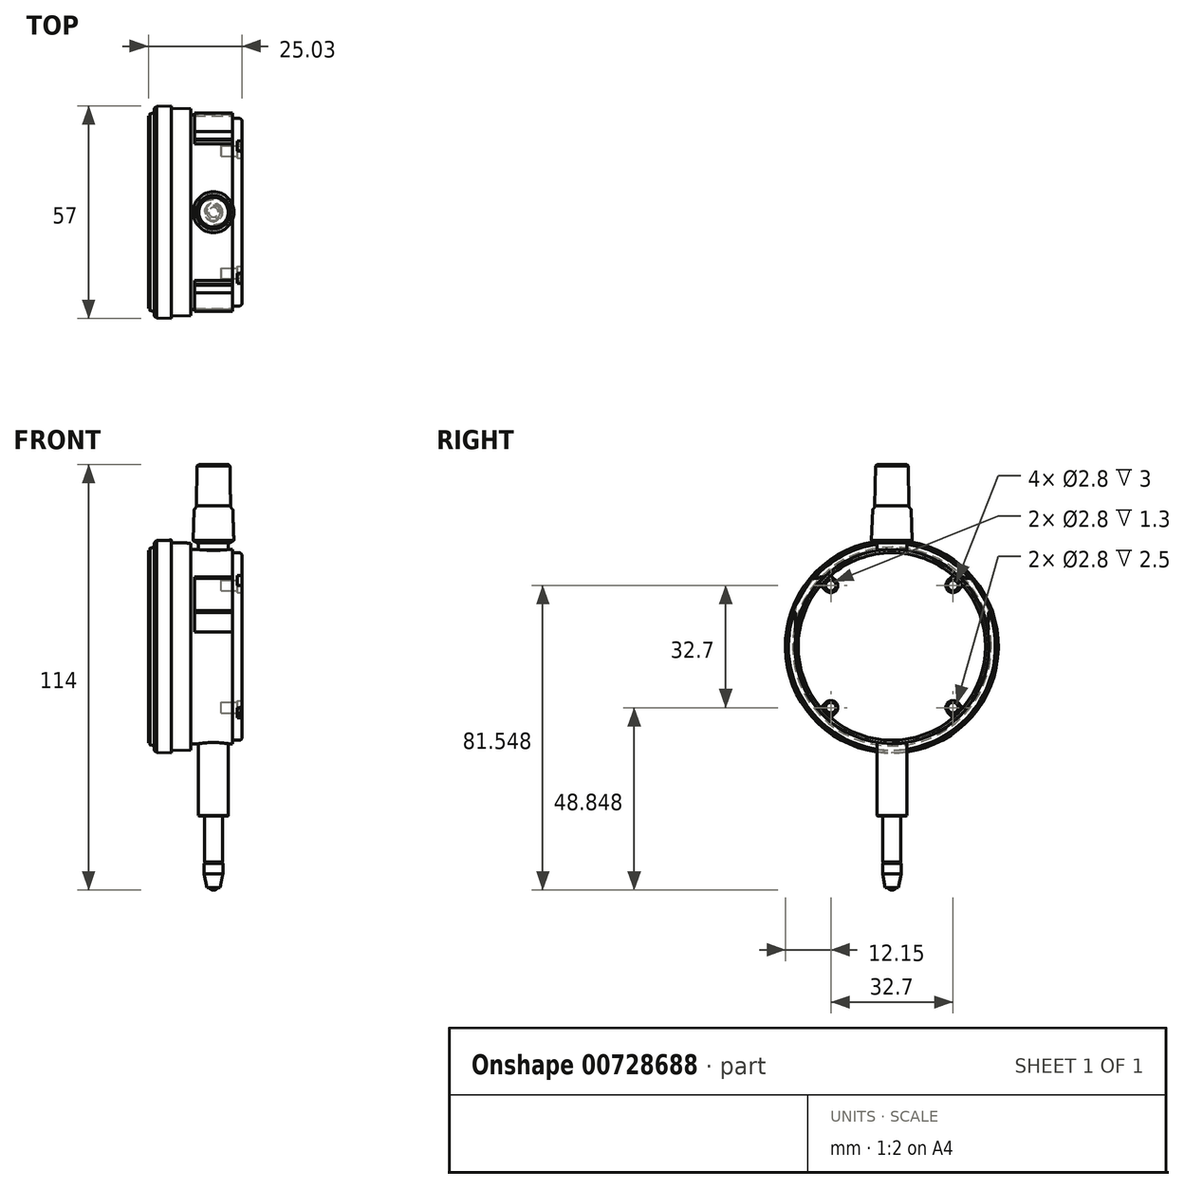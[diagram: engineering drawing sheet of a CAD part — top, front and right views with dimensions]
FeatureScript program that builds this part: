
annotation { "Feature Type Name" : "Feature", "Feature Type Description" : "" }
export const myFeature = defineFeature(function(context is Context, id is Id, definition is map)
    precondition{}
    {
        {
            var Q0;
            Q0=qCreatedBy(makeId("Front.planeOp"),FACE);
            var sketch = newSketch(context, id + "F0", { "sketchPlane" : qUnion([Q0])});
            skLineSegment(sketch, "E0", {"start": v(12.6, 32.51) * mm, "end": v(12.6, 34.58) * mm});
            skLineSegment(sketch, "E1", {"start": v(13, 34.58) * mm, "end": v(12.6, 34.58) * mm});
            skLineSegment(sketch, "E2", {"start": v(12.65, 38.95) * mm, "end": v(12.6, 38.5) * mm});
            skLineSegment(sketch, "E3", {"start": v(12.6, 38.5) * mm, "end": v(12.6, 37.7) * mm});
            skLineSegment(sketch, "E4", {"start": v(12.6, 35.36) * mm, "end": v(12.6, 35.33) * mm});
            skLineSegment(sketch, "E5", {"start": v(12.6, 35.38) * mm, "end": v(12.6, 35.36) * mm});
            skLineSegment(sketch, "E6", {"start": v(12.6, 35.33) * mm, "end": v(12.6, 34.58) * mm});
            skLineSegment(sketch, "E7", {"start": v(12.6, 37.2) * mm, "end": v(12.6, 35.4) * mm});
            skLineSegment(sketch, "E8", {"start": v(12.6, 37.7) * mm, "end": v(12.6, 37.2) * mm});
            skLineSegment(sketch, "E9", {"start": v(12.6, 35.4) * mm, "end": v(12.6, 35.38) * mm});
            skLineSegment(sketch, "E10", {"start": v(12.6, 32.43) * mm, "end": v(12.6, 32.49) * mm});
            skLineSegment(sketch, "E11", {"start": v(12.65, 38.95) * mm, "end": v(12.65, 35.83) * mm});
            skLineSegment(sketch, "E12", {"start": v(13.25, 34.58) * mm, "end": v(13, 34.58) * mm});
            skLineSegment(sketch, "E13", {"start": v(13.3, 32.31) * mm, "end": v(13.22, 32.31) * mm});
            skLineSegment(sketch, "E14", {"start": v(13.3, 34.58) * mm, "end": v(13.25, 34.58) * mm});
            skLineSegment(sketch, "E15", {"start": v(13.3, 33.25) * mm, "end": v(13.3, 34.58) * mm});
            skLineSegment(sketch, "E16", {"start": v(13.3, 34.58) * mm, "end": v(13.3, 34.91) * mm});
            skLineSegment(sketch, "E17", {"start": v(13.3, 33.25) * mm, "end": v(13.3, 32.83) * mm});
            skLineSegment(sketch, "E18", {"start": v(13.3, 32.49) * mm, "end": v(13.3, 32.43) * mm});
            skLineSegment(sketch, "E19", {"start": v(13.3, 32.31) * mm, "end": v(13.3, 32.43) * mm});
            skLineSegment(sketch, "E20", {"start": v(13.3, 32.83) * mm, "end": v(13.3, 32.49) * mm});
            skLineSegment(sketch, "E21", {"start": v(12.65, 35.83) * mm, "end": v(12.6, 35.38) * mm});
            skLineSegment(sketch, "E22", {"start": v(13.22, 32.31) * mm, "end": v(12.6, 32.31) * mm});
            skLineSegment(sketch, "E23", {"start": v(13.3, 32.43) * mm, "end": v(12.6, 32.43) * mm});
            skLineSegment(sketch, "E24", {"start": v(12.6, 32.49) * mm, "end": v(12.6, 32.51) * mm});
            skLineSegment(sketch, "E25", {"start": v(12.6, 32.31) * mm, "end": v(12.6, 32.43) * mm});
            skLineSegment(sketch, "E26", {"start": v(14.23, 36.45) * mm, "end": v(14.25, 36.61) * mm});
            skLineSegment(sketch, "E27", {"start": v(14.62, 36.19) * mm, "end": v(14.5, 36.2) * mm});
            skLineSegment(sketch, "E28", {"start": v(14.6, 35.25) * mm, "end": v(15, 35.22) * mm});
            skLineSegment(sketch, "E29", {"start": v(13.88, 35.3) * mm, "end": v(14.6, 35.25) * mm});
            skLineSegment(sketch, "E30", {"start": v(13.85, 35.3) * mm, "end": v(13.88, 35.3) * mm});
            skLineSegment(sketch, "E31", {"start": v(14.62, 36.97) * mm, "end": v(14.62, 36.19) * mm});
            skLineSegment(sketch, "E32", {"start": v(14.5, 36.92) * mm, "end": v(14.5, 36.2) * mm});
            skLineSegment(sketch, "E33", {"start": v(20.49, 35.87) * mm, "end": v(20.56, 36.52) * mm});
            skLineSegment(sketch, "E34", {"start": v(20.57, 39.75) * mm, "end": v(20.57, 36.63) * mm});
            skArc(sketch, "E35", {"start": v(13.35, 40.26) * mm, "mid": v(13.24, 40.15) * mm, "end": v(13.13, 40.03) * mm});
            skArc(sketch, "E36", {"start": v(13.13, 40.03) * mm, "mid": v(13.04, 39.9) * mm, "end": v(12.95, 39.78) * mm});
            skArc(sketch, "E37", {"start": v(12.95, 39.78) * mm, "mid": v(12.87, 39.65) * mm, "end": v(12.8, 39.51) * mm});
            skArc(sketch, "E38", {"start": v(12.8, 39.51) * mm, "mid": v(12.75, 39.37) * mm, "end": v(12.7, 39.23) * mm});
            skArc(sketch, "E39", {"start": v(12.7, 39.23) * mm, "mid": v(12.67, 39.1) * mm, "end": v(12.65, 38.95) * mm});
            skArc(sketch, "E40", {"start": v(13.3, 34.91) * mm, "mid": v(13.3, 34.94) * mm, "end": v(13.3, 34.96) * mm});
            skArc(sketch, "E41", {"start": v(13.3, 34.96) * mm, "mid": v(13.31, 34.99) * mm, "end": v(13.32, 35.01) * mm});
            skArc(sketch, "E42", {"start": v(13.32, 35.01) * mm, "mid": v(13.33, 35.03) * mm, "end": v(13.34, 35.06) * mm});
            skArc(sketch, "E43", {"start": v(13.34, 35.06) * mm, "mid": v(13.35, 35.08) * mm, "end": v(13.37, 35.1) * mm});
            skArc(sketch, "E44", {"start": v(13.37, 35.1) * mm, "mid": v(13.39, 35.13) * mm, "end": v(13.4, 35.15) * mm});
            skLineSegment(sketch, "E45", {"start": v(13.4, 35.15) * mm, "end": v(13.42, 35.17) * mm});
            skArc(sketch, "E46", {"start": v(13.42, 40.32) * mm, "mid": v(13.5, 40.38) * mm, "end": v(13.57, 40.44) * mm});
            skArc(sketch, "E47", {"start": v(13.57, 40.44) * mm, "mid": v(13.64, 40.5) * mm, "end": v(13.72, 40.54) * mm});
            skLineSegment(sketch, "E48", {"start": v(13.72, 40.54) * mm, "end": v(13.8, 40.6) * mm});
            skArc(sketch, "E49", {"start": v(13.8, 35.3) * mm, "mid": v(13.76, 35.3) * mm, "end": v(13.72, 35.3) * mm});
            skArc(sketch, "E50", {"start": v(13.72, 35.3) * mm, "mid": v(13.68, 35.29) * mm, "end": v(13.63, 35.28) * mm});
            skArc(sketch, "E51", {"start": v(13.63, 35.28) * mm, "mid": v(13.6, 35.27) * mm, "end": v(13.56, 35.25) * mm});
            skArc(sketch, "E52", {"start": v(13.56, 35.25) * mm, "mid": v(13.52, 35.23) * mm, "end": v(13.49, 35.21) * mm});
            skArc(sketch, "E53", {"start": v(13.49, 35.21) * mm, "mid": v(13.45, 35.2) * mm, "end": v(13.42, 35.17) * mm});
            skArc(sketch, "E54", {"start": v(12.65, 35.83) * mm, "mid": v(12.68, 36) * mm, "end": v(12.72, 36.17) * mm});
            skArc(sketch, "E55", {"start": v(12.72, 36.17) * mm, "mid": v(12.78, 36.33) * mm, "end": v(12.86, 36.5) * mm});
            skArc(sketch, "E56", {"start": v(12.86, 36.5) * mm, "mid": v(12.95, 36.65) * mm, "end": v(13.05, 36.8) * mm});
            skArc(sketch, "E57", {"start": v(13.05, 36.8) * mm, "mid": v(13.18, 36.96) * mm, "end": v(13.32, 37.11) * mm});
            skArc(sketch, "E58", {"start": v(13.32, 37.11) * mm, "mid": v(13.5, 37.26) * mm, "end": v(13.68, 37.4) * mm});
            skArc(sketch, "E59", {"start": v(13.68, 37.4) * mm, "mid": v(13.88, 37.52) * mm, "end": v(14.1, 37.63) * mm});
            skLineSegment(sketch, "E60", {"start": v(14.1, 37.63) * mm, "end": v(14.32, 37.73) * mm});
            skArc(sketch, "E61", {"start": v(14.25, 36.61) * mm, "mid": v(14.25, 36.64) * mm, "end": v(14.26, 36.67) * mm});
            skArc(sketch, "E62", {"start": v(14.26, 36.67) * mm, "mid": v(14.27, 36.7) * mm, "end": v(14.28, 36.72) * mm});
            skArc(sketch, "E63", {"start": v(14.28, 36.72) * mm, "mid": v(14.3, 36.74) * mm, "end": v(14.3, 36.77) * mm});
            skArc(sketch, "E64", {"start": v(14.3, 36.77) * mm, "mid": v(14.33, 36.8) * mm, "end": v(14.35, 36.82) * mm});
            skArc(sketch, "E65", {"start": v(14.35, 36.82) * mm, "mid": v(14.37, 36.84) * mm, "end": v(14.4, 36.86) * mm});
            skArc(sketch, "E66", {"start": v(14.4, 36.86) * mm, "mid": v(14.43, 36.88) * mm, "end": v(14.46, 36.9) * mm});
            skLineSegment(sketch, "E67", {"start": v(14.46, 36.9) * mm, "end": v(14.5, 36.92) * mm});
            skArc(sketch, "E68", {"start": v(15, 37.11) * mm, "mid": v(14.87, 37.07) * mm, "end": v(14.73, 37.02) * mm});
            skLineSegment(sketch, "E69", {"start": v(14.73, 37.02) * mm, "end": v(14.6, 36.96) * mm});
            skArc(sketch, "E70", {"start": v(14.6, 36.96) * mm, "mid": v(14.55, 36.94) * mm, "end": v(14.5, 36.92) * mm});
            skArc(sketch, "E71", {"start": v(15.15, 37.16) * mm, "mid": v(15.07, 37.14) * mm, "end": v(15, 37.11) * mm});
            skArc(sketch, "E72", {"start": v(15.03, 35.96) * mm, "mid": v(15, 36) * mm, "end": v(14.98, 36.02) * mm});
            skArc(sketch, "E73", {"start": v(14.98, 36.02) * mm, "mid": v(14.96, 36.05) * mm, "end": v(14.93, 36.08) * mm});
            skArc(sketch, "E74", {"start": v(14.93, 36.08) * mm, "mid": v(14.9, 36.1) * mm, "end": v(14.86, 36.12) * mm});
            skArc(sketch, "E75", {"start": v(14.86, 36.12) * mm, "mid": v(14.83, 36.14) * mm, "end": v(14.79, 36.15) * mm});
            skArc(sketch, "E76", {"start": v(14.79, 36.15) * mm, "mid": v(14.75, 36.17) * mm, "end": v(14.7, 36.18) * mm});
            skArc(sketch, "E77", {"start": v(14.7, 36.18) * mm, "mid": v(14.66, 36.18) * mm, "end": v(14.62, 36.19) * mm});
            skArc(sketch, "E78", {"start": v(14.5, 36.2) * mm, "mid": v(14.47, 36.2) * mm, "end": v(14.44, 36.2) * mm});
            skArc(sketch, "E79", {"start": v(14.44, 36.2) * mm, "mid": v(14.4, 36.21) * mm, "end": v(14.38, 36.23) * mm});
            skArc(sketch, "E80", {"start": v(14.38, 36.23) * mm, "mid": v(14.35, 36.24) * mm, "end": v(14.33, 36.25) * mm});
            skArc(sketch, "E81", {"start": v(14.33, 36.25) * mm, "mid": v(14.3, 36.27) * mm, "end": v(14.29, 36.29) * mm});
            skArc(sketch, "E82", {"start": v(14.29, 36.29) * mm, "mid": v(14.27, 36.3) * mm, "end": v(14.26, 36.33) * mm});
            skArc(sketch, "E83", {"start": v(14.26, 36.33) * mm, "mid": v(14.25, 36.34) * mm, "end": v(14.24, 36.37) * mm});
            skArc(sketch, "E84", {"start": v(14.24, 36.37) * mm, "mid": v(14.23, 36.39) * mm, "end": v(14.23, 36.4) * mm});
            skLineSegment(sketch, "E85", {"start": v(14.23, 36.4) * mm, "end": v(14.23, 36.43) * mm});
            skArc(sketch, "E86", {"start": v(14.32, 40.85) * mm, "mid": v(14.2, 40.8) * mm, "end": v(14.1, 40.75) * mm});
            skArc(sketch, "E87", {"start": v(14.1, 40.75) * mm, "mid": v(13.98, 40.7) * mm, "end": v(13.88, 40.64) * mm});
            skArc(sketch, "E88", {"start": v(15.15, 41.1) * mm, "mid": v(15.08, 41.09) * mm, "end": v(15, 41.07) * mm});
            skArc(sketch, "E89", {"start": v(15.4, 41.17) * mm, "mid": v(15.32, 41.15) * mm, "end": v(15.23, 41.13) * mm});
            skLineSegment(sketch, "E90", {"start": v(15.23, 41.13) * mm, "end": v(15.15, 41.1) * mm});
            skArc(sketch, "E91", {"start": v(15, 41.07) * mm, "mid": v(14.87, 41.03) * mm, "end": v(14.73, 41) * mm});
            skLineSegment(sketch, "E92", {"start": v(14.73, 41) * mm, "end": v(14.6, 40.95) * mm});
            skArc(sketch, "E93", {"start": v(14.6, 40.95) * mm, "mid": v(14.5, 40.92) * mm, "end": v(14.41, 40.88) * mm});
            skLineSegment(sketch, "E94", {"start": v(14.41, 40.88) * mm, "end": v(14.32, 40.85) * mm});
            skArc(sketch, "E95", {"start": v(17.17, 37.42) * mm, "mid": v(16.94, 37.43) * mm, "end": v(16.7, 37.42) * mm});
            skArc(sketch, "E96", {"start": v(16.7, 37.42) * mm, "mid": v(16.48, 37.4) * mm, "end": v(16.25, 37.39) * mm});
            skLineSegment(sketch, "E97", {"start": v(16.25, 37.39) * mm, "end": v(16.02, 37.36) * mm});
            skArc(sketch, "E98", {"start": v(16.02, 37.36) * mm, "mid": v(15.87, 37.33) * mm, "end": v(15.7, 37.3) * mm});
            skArc(sketch, "E99", {"start": v(15.7, 37.3) * mm, "mid": v(15.56, 37.27) * mm, "end": v(15.4, 37.23) * mm});
            skArc(sketch, "E100", {"start": v(16.02, 41.27) * mm, "mid": v(15.87, 41.25) * mm, "end": v(15.71, 41.22) * mm});
            skArc(sketch, "E101", {"start": v(15.71, 41.22) * mm, "mid": v(15.56, 41.2) * mm, "end": v(15.4, 41.17) * mm});
            skArc(sketch, "E102", {"start": v(17.17, 41.32) * mm, "mid": v(16.94, 41.33) * mm, "end": v(16.71, 41.32) * mm});
            skArc(sketch, "E103", {"start": v(16.71, 41.32) * mm, "mid": v(16.48, 41.31) * mm, "end": v(16.25, 41.3) * mm});
            skLineSegment(sketch, "E104", {"start": v(16.25, 41.3) * mm, "end": v(16.02, 41.27) * mm});
            skArc(sketch, "E105", {"start": v(15.36, 37.22) * mm, "mid": v(15.3, 37.2) * mm, "end": v(15.22, 37.18) * mm});
            skLineSegment(sketch, "E106", {"start": v(15.22, 37.18) * mm, "end": v(15.15, 37.16) * mm});
            skArc(sketch, "E107", {"start": v(19.77, 37.66) * mm, "mid": v(19.25, 37.85) * mm, "end": v(18.72, 38) * mm});
            skArc(sketch, "E108", {"start": v(18.72, 38) * mm, "mid": v(18.18, 38.1) * mm, "end": v(17.62, 38.18) * mm});
            skArc(sketch, "E109", {"start": v(17.62, 38.18) * mm, "mid": v(17.05, 38.2) * mm, "end": v(16.49, 38.2) * mm});
            skArc(sketch, "E110", {"start": v(16.49, 38.2) * mm, "mid": v(15.93, 38.14) * mm, "end": v(15.38, 38.04) * mm});
            skArc(sketch, "E111", {"start": v(15.38, 38.04) * mm, "mid": v(14.84, 37.9) * mm, "end": v(14.32, 37.73) * mm});
            skArc(sketch, "E112", {"start": v(20.56, 36.52) * mm, "mid": v(20.56, 36.55) * mm, "end": v(20.56, 36.58) * mm});
            skArc(sketch, "E113", {"start": v(20.56, 36.58) * mm, "mid": v(20.57, 36.6) * mm, "end": v(20.57, 36.63) * mm});
            skArc(sketch, "E114", {"start": v(19.77, 37.66) * mm, "mid": v(19.88, 37.6) * mm, "end": v(20, 37.55) * mm});
            skArc(sketch, "E115", {"start": v(20, 37.55) * mm, "mid": v(20.1, 37.48) * mm, "end": v(20.2, 37.4) * mm});
            skArc(sketch, "E116", {"start": v(20.2, 37.4) * mm, "mid": v(20.28, 37.32) * mm, "end": v(20.35, 37.23) * mm});
            skArc(sketch, "E117", {"start": v(20.35, 37.23) * mm, "mid": v(20.4, 37.15) * mm, "end": v(20.46, 37.07) * mm});
            skArc(sketch, "E118", {"start": v(20.46, 37.07) * mm, "mid": v(20.5, 36.98) * mm, "end": v(20.53, 36.9) * mm});
            skArc(sketch, "E119", {"start": v(20.53, 36.9) * mm, "mid": v(20.55, 36.8) * mm, "end": v(20.56, 36.72) * mm});
            skLineSegment(sketch, "E120", {"start": v(20.56, 36.72) * mm, "end": v(20.57, 36.63) * mm});
            skArc(sketch, "E121", {"start": v(19.77, 40.78) * mm, "mid": v(19.88, 40.73) * mm, "end": v(20, 40.67) * mm});
            skArc(sketch, "E122", {"start": v(20, 40.67) * mm, "mid": v(20.1, 40.6) * mm, "end": v(20.2, 40.52) * mm});
            skArc(sketch, "E123", {"start": v(20.2, 40.52) * mm, "mid": v(20.28, 40.44) * mm, "end": v(20.35, 40.35) * mm});
            skArc(sketch, "E124", {"start": v(20.35, 40.35) * mm, "mid": v(20.4, 40.27) * mm, "end": v(20.46, 40.19) * mm});
            skArc(sketch, "E125", {"start": v(20.46, 40.19) * mm, "mid": v(20.5, 40.1) * mm, "end": v(20.53, 40.02) * mm});
            skArc(sketch, "E126", {"start": v(20.53, 40.02) * mm, "mid": v(20.55, 39.93) * mm, "end": v(20.56, 39.84) * mm});
            skLineSegment(sketch, "E127", {"start": v(20.56, 39.84) * mm, "end": v(20.57, 39.75) * mm});
            skArc(sketch, "E128", {"start": v(19.77, 40.78) * mm, "mid": v(19.68, 40.82) * mm, "end": v(19.6, 40.85) * mm});
            skArc(sketch, "E129", {"start": v(19.17, 37.03) * mm, "mid": v(19.06, 37.07) * mm, "end": v(18.95, 37.1) * mm});
            skArc(sketch, "E130", {"start": v(18.95, 37.1) * mm, "mid": v(18.83, 37.14) * mm, "end": v(18.72, 37.18) * mm});
            skArc(sketch, "E131", {"start": v(18.72, 37.18) * mm, "mid": v(18.59, 37.21) * mm, "end": v(18.46, 37.25) * mm});
            skLineSegment(sketch, "E132", {"start": v(18.46, 37.25) * mm, "end": v(18.32, 37.28) * mm});
            skArc(sketch, "E133", {"start": v(18.32, 37.28) * mm, "mid": v(18.27, 37.29) * mm, "end": v(18.22, 37.3) * mm});
            skArc(sketch, "E134", {"start": v(17.4, 41.31) * mm, "mid": v(17.29, 41.32) * mm, "end": v(17.17, 41.32) * mm});
            skArc(sketch, "E135", {"start": v(17.4, 37.41) * mm, "mid": v(17.33, 37.41) * mm, "end": v(17.25, 37.42) * mm});
            skLineSegment(sketch, "E136", {"start": v(17.25, 37.42) * mm, "end": v(17.17, 37.42) * mm});
            skArc(sketch, "E137", {"start": v(17.5, 37.4) * mm, "mid": v(17.45, 37.4) * mm, "end": v(17.4, 37.41) * mm});
            skArc(sketch, "E138", {"start": v(17.5, 41.3) * mm, "mid": v(17.45, 41.31) * mm, "end": v(17.4, 41.31) * mm});
            skArc(sketch, "E139", {"start": v(18.22, 37.3) * mm, "mid": v(18.15, 37.31) * mm, "end": v(18.08, 37.33) * mm});
            skLineSegment(sketch, "E140", {"start": v(18.08, 37.33) * mm, "end": v(18, 37.34) * mm});
            skArc(sketch, "E141", {"start": v(18.22, 41.22) * mm, "mid": v(18.11, 41.24) * mm, "end": v(18, 41.26) * mm});
            skArc(sketch, "E142", {"start": v(18, 41.26) * mm, "mid": v(17.88, 41.27) * mm, "end": v(17.75, 41.29) * mm});
            skLineSegment(sketch, "E143", {"start": v(17.75, 41.29) * mm, "end": v(17.62, 41.3) * mm});
            skArc(sketch, "E144", {"start": v(17.62, 41.3) * mm, "mid": v(17.56, 41.3) * mm, "end": v(17.5, 41.3) * mm});
            skArc(sketch, "E145", {"start": v(17.62, 37.4) * mm, "mid": v(17.56, 37.4) * mm, "end": v(17.5, 37.4) * mm});
            skArc(sketch, "E146", {"start": v(18, 37.34) * mm, "mid": v(17.88, 37.36) * mm, "end": v(17.75, 37.38) * mm});
            skLineSegment(sketch, "E147", {"start": v(17.75, 37.38) * mm, "end": v(17.62, 37.4) * mm});
            skArc(sketch, "E148", {"start": v(18.98, 41.05) * mm, "mid": v(18.82, 41.1) * mm, "end": v(18.66, 41.14) * mm});
            skArc(sketch, "E149", {"start": v(18.66, 41.14) * mm, "mid": v(18.49, 41.17) * mm, "end": v(18.32, 41.2) * mm});
            skArc(sketch, "E150", {"start": v(19.27, 36.99) * mm, "mid": v(19.22, 37) * mm, "end": v(19.17, 37.03) * mm});
            skArc(sketch, "E151", {"start": v(19.3, 36.97) * mm, "mid": v(19.33, 36.96) * mm, "end": v(19.36, 36.94) * mm});
            skArc(sketch, "E152", {"start": v(19.36, 36.94) * mm, "mid": v(19.38, 36.93) * mm, "end": v(19.41, 36.9) * mm});
            skArc(sketch, "E153", {"start": v(19.41, 36.9) * mm, "mid": v(19.43, 36.9) * mm, "end": v(19.46, 36.87) * mm});
            skArc(sketch, "E154", {"start": v(19.46, 36.87) * mm, "mid": v(19.48, 36.85) * mm, "end": v(19.5, 36.83) * mm});
            skLineSegment(sketch, "E155", {"start": v(19.5, 36.83) * mm, "end": v(19.51, 36.8) * mm});
            skArc(sketch, "E156", {"start": v(19.51, 40.88) * mm, "mid": v(19.34, 40.94) * mm, "end": v(19.16, 41) * mm});
            skLineSegment(sketch, "E157", {"start": v(19.16, 41) * mm, "end": v(18.98, 41.05) * mm});
            skArc(sketch, "E158", {"start": v(19.51, 36.8) * mm, "mid": v(19.52, 36.79) * mm, "end": v(19.53, 36.77) * mm});
            skArc(sketch, "E159", {"start": v(19.53, 36.77) * mm, "mid": v(19.54, 36.76) * mm, "end": v(19.55, 36.74) * mm});
            skArc(sketch, "E160", {"start": v(19.55, 36.74) * mm, "mid": v(19.55, 36.72) * mm, "end": v(19.56, 36.7) * mm});
            skArc(sketch, "E161", {"start": v(19.56, 36.7) * mm, "mid": v(19.57, 36.68) * mm, "end": v(19.57, 36.66) * mm});
            skArc(sketch, "E162", {"start": v(19.57, 36.66) * mm, "mid": v(19.58, 36.64) * mm, "end": v(19.6, 36.62) * mm});
            skLineSegment(sketch, "E163", {"start": v(19.6, 36.62) * mm, "end": v(19.6, 36.6) * mm});
            skArc(sketch, "E164", {"start": v(20.49, 35.87) * mm, "mid": v(20.41, 35.77) * mm, "end": v(20.33, 35.67) * mm});
            skArc(sketch, "E165", {"start": v(20.33, 35.67) * mm, "mid": v(20.24, 35.59) * mm, "end": v(20.15, 35.51) * mm});
            skArc(sketch, "E166", {"start": v(20.15, 35.51) * mm, "mid": v(20.05, 35.45) * mm, "end": v(19.95, 35.39) * mm});
            skArc(sketch, "E167", {"start": v(19.95, 35.39) * mm, "mid": v(19.84, 35.34) * mm, "end": v(19.72, 35.3) * mm});
            skLineSegment(sketch, "E168", {"start": v(19.72, 35.3) * mm, "end": v(19.6, 35.26) * mm});
            skLineSegment(sketch, "E169", {"start": v(13.42, 43.49) * mm, "end": v(13.42, 40.32) * mm});
            skLineSegment(sketch, "E170", {"start": v(13.42, 43.49) * mm, "end": v(13.8, 43.49) * mm});
            skLineSegment(sketch, "E171", {"start": v(13.42, -8.11) * mm, "end": v(13.8, -8.11) * mm});
            skLineSegment(sketch, "E172", {"start": v(13.42, 17.69) * mm, "end": v(13.42, -8.11) * mm});
            skLineSegment(sketch, "E173", {"start": v(13.42, 35.17) * mm, "end": v(13.42, 17.69) * mm});
            skArc(sketch, "E174", {"start": v(13.42, 43.49) * mm, "mid": v(13.39, 41.87) * mm, "end": v(13.35, 40.26) * mm});
            skArc(sketch, "E175", {"start": v(13.22, 32.31) * mm, "mid": v(13.15, 25) * mm, "end": v(13.12, 17.69) * mm});
            skArc(sketch, "E176", {"start": v(13.12, 17.69) * mm, "mid": v(13.2, 4.79) * mm, "end": v(13.42, -8.11) * mm});
            skLineSegment(sketch, "E177", {"start": v(19.6, 35.26) * mm, "end": v(19.6, -10.71) * mm});
            skLineSegment(sketch, "E178", {"start": v(19.6, 35.26) * mm, "end": v(19.6, 36.6) * mm});
            skLineSegment(sketch, "E179", {"start": v(19.6, 46.09) * mm, "end": v(19.6, 40.85) * mm});
            skLineSegment(sketch, "E180", {"start": v(19.6, -10.71) * mm, "end": v(19.5, -10.81) * mm});
            skLineSegment(sketch, "E181", {"start": v(15.56, -10.67) * mm, "end": v(19.5, -10.81) * mm});
            skLineSegment(sketch, "E182", {"start": v(15.45, -10.56) * mm, "end": v(15.56, -10.67) * mm});
            skLineSegment(sketch, "E183", {"start": v(15.15, -10.26) * mm, "end": v(15.45, -10.56) * mm});
            skLineSegment(sketch, "E184", {"start": v(13.8, -8.11) * mm, "end": v(13.8, -8.54) * mm});
            skLineSegment(sketch, "E185", {"start": v(15.15, 45.63) * mm, "end": v(15.45, 45.94) * mm});
            skLineSegment(sketch, "E186", {"start": v(15.45, 45.94) * mm, "end": v(15.56, 46.05) * mm});
            skLineSegment(sketch, "E187", {"start": v(13.88, 44) * mm, "end": v(13.88, 40.64) * mm});
            skLineSegment(sketch, "E188", {"start": v(13.8, 17.69) * mm, "end": v(13.8, -8.11) * mm});
            skLineSegment(sketch, "E189", {"start": v(13.88, 44) * mm, "end": v(15, 44.3) * mm});
            skLineSegment(sketch, "E190", {"start": v(13.88, 35.3) * mm, "end": v(13.88, 17.69) * mm});
            skLineSegment(sketch, "E191", {"start": v(13.8, 43.49) * mm, "end": v(13.8, 40.6) * mm});
            skLineSegment(sketch, "E192", {"start": v(13.8, 35.3) * mm, "end": v(13.8, 17.69) * mm});
            skLineSegment(sketch, "E193", {"start": v(13.8, 43.9) * mm, "end": v(13.8, 43.49) * mm});
            skLineSegment(sketch, "E194", {"start": v(15, 45.19) * mm, "end": v(15, 41.07) * mm});
            skLineSegment(sketch, "E195", {"start": v(15, 37.11) * mm, "end": v(15, 17.69) * mm});
            skLineSegment(sketch, "E196", {"start": v(15, 45.28) * mm, "end": v(15, 45.19) * mm});
            skLineSegment(sketch, "E197", {"start": v(15.15, 45.63) * mm, "end": v(15.15, 41.1) * mm});
            skLineSegment(sketch, "E198", {"start": v(15.15, 37.16) * mm, "end": v(15.15, 17.69) * mm});
            skLineSegment(sketch, "E199", {"start": v(15.56, 46.05) * mm, "end": v(19.5, 46.19) * mm});
            skLineSegment(sketch, "E200", {"start": v(24.8, 45.39) * mm, "end": v(19.6, 45.48) * mm});
            skLineSegment(sketch, "E201", {"start": v(19.6, 46.09) * mm, "end": v(19.5, 46.19) * mm});
            skLineSegment(sketch, "E202", {"start": v(13.88, 17.69) * mm, "end": v(13.88, -8.63) * mm});
            skLineSegment(sketch, "E203", {"start": v(13.88, -8.63) * mm, "end": v(15, -8.93) * mm});
            skLineSegment(sketch, "E204", {"start": v(15, 17.69) * mm, "end": v(15, -9.81) * mm});
            skLineSegment(sketch, "E205", {"start": v(24.8, -10.02) * mm, "end": v(19.6, -10.1) * mm});
            skLineSegment(sketch, "E206", {"start": v(15, -9.81) * mm, "end": v(15, -9.9) * mm});
            skLineSegment(sketch, "E207", {"start": v(15.15, 17.69) * mm, "end": v(15.15, -10.26) * mm});
            skLineSegment(sketch, "E208", {"start": v(24.8, 44.33) * mm, "end": v(24.8, 37.43) * mm});
            skLineSegment(sketch, "E209", {"start": v(24.8, 45.39) * mm, "end": v(24.8, 44.33) * mm});
            skLineSegment(sketch, "E210", {"start": v(24.8, 27.7) * mm, "end": v(24.8, 17.69) * mm});
            skLineSegment(sketch, "E211", {"start": v(24.8, 17.69) * mm, "end": v(24.8, -8.96) * mm});
            skLineSegment(sketch, "E212", {"start": v(24.8, -8.96) * mm, "end": v(24.8, -10.02) * mm});
            skArc(sketch, "E213", {"start": v(13.8, -8.54) * mm, "mid": v(13.82, -8.6) * mm, "end": v(13.88, -8.63) * mm});
            skArc(sketch, "E214", {"start": v(13.88, 44) * mm, "mid": v(13.82, 43.97) * mm, "end": v(13.8, 43.9) * mm});
            skArc(sketch, "E215", {"start": v(15.15, 45.63) * mm, "mid": v(15.04, 45.47) * mm, "end": v(15, 45.28) * mm});
            skArc(sketch, "E216", {"start": v(15, -9.9) * mm, "mid": v(15.04, -10.1) * mm, "end": v(15.15, -10.26) * mm});
            skLineSegment(sketch, "E217", {"start": v(-16.72, 15.9) * mm, "end": v(-16.62, 15.9) * mm});
            skLineSegment(sketch, "E218", {"start": v(-16.79, 15.02) * mm, "end": v(-16.7, 15) * mm});
            skLineSegment(sketch, "E219", {"start": v(-16.89, 14.13) * mm, "end": v(-16.8, 14.12) * mm});
            skLineSegment(sketch, "E220", {"start": v(-17.01, 13.25) * mm, "end": v(-16.92, 13.23) * mm});
            skLineSegment(sketch, "E221", {"start": v(-73.11, 13.25) * mm, "end": v(-73.2, 13.23) * mm});
            skLineSegment(sketch, "E222", {"start": v(-73.45, 18.58) * mm, "end": v(-73.55, 18.58) * mm});
            skLineSegment(sketch, "E223", {"start": v(-73.4, 19.47) * mm, "end": v(-73.5, 19.48) * mm});
            skLineSegment(sketch, "E224", {"start": v(-16.68, 18.58) * mm, "end": v(-16.58, 18.58) * mm});
            skLineSegment(sketch, "E225", {"start": v(-16.68, 16.8) * mm, "end": v(-16.58, 16.8) * mm});
            skLineSegment(sketch, "E226", {"start": v(-16.72, 19.47) * mm, "end": v(-16.62, 19.48) * mm});
            skLineSegment(sketch, "E227", {"start": v(-16.66, 17.69) * mm, "end": v(-16.57, 17.69) * mm});
            skLineSegment(sketch, "E228", {"start": v(-73.45, 16.8) * mm, "end": v(-73.55, 16.8) * mm});
            skLineSegment(sketch, "E229", {"start": v(-62.47, 40.13) * mm, "end": v(-62.53, 40.2) * mm});
            skLineSegment(sketch, "E230", {"start": v(-61.76, 40.66) * mm, "end": v(-61.81, 40.74) * mm});
            skLineSegment(sketch, "E231", {"start": v(-61.03, 41.18) * mm, "end": v(-61.08, 41.26) * mm});
            skLineSegment(sketch, "E232", {"start": v(-60.28, 41.67) * mm, "end": v(-60.33, 41.75) * mm});
            skLineSegment(sketch, "E233", {"start": v(-59.52, 42.13) * mm, "end": v(-59.57, 42.22) * mm});
            skLineSegment(sketch, "E234", {"start": v(-58.75, 42.58) * mm, "end": v(-58.8, 42.66) * mm});
            skLineSegment(sketch, "E235", {"start": v(-57.96, 43) * mm, "end": v(-58, 43.08) * mm});
            skLineSegment(sketch, "E236", {"start": v(-57.16, 43.39) * mm, "end": v(-57.2, 43.47) * mm});
            skLineSegment(sketch, "E237", {"start": v(-56.34, 43.75) * mm, "end": v(-56.38, 43.84) * mm});
            skLineSegment(sketch, "E238", {"start": v(-55.52, 44.1) * mm, "end": v(-55.55, 44.18) * mm});
            skLineSegment(sketch, "E239", {"start": v(-54.68, 44.4) * mm, "end": v(-54.72, 44.5) * mm});
            skLineSegment(sketch, "E240", {"start": v(-53.84, 44.7) * mm, "end": v(-53.87, 44.8) * mm});
            skLineSegment(sketch, "E241", {"start": v(-61.76, -5.29) * mm, "end": v(-61.81, -5.37) * mm});
            skLineSegment(sketch, "E242", {"start": v(-60.28, -6.3) * mm, "end": v(-60.33, -6.37) * mm});
            skLineSegment(sketch, "E243", {"start": v(-59.52, -6.76) * mm, "end": v(-59.57, -6.84) * mm});
            skLineSegment(sketch, "E244", {"start": v(-52.99, 44.96) * mm, "end": v(-53.01, 45.05) * mm});
            skLineSegment(sketch, "E245", {"start": v(-61.03, -5.8) * mm, "end": v(-61.08, -5.88) * mm});
            skLineSegment(sketch, "E246", {"start": v(-55.52, -8.72) * mm, "end": v(-55.55, -8.8) * mm});
            skLineSegment(sketch, "E247", {"start": v(-54.68, -9.03) * mm, "end": v(-54.72, -9.12) * mm});
            skLineSegment(sketch, "E248", {"start": v(-52.99, -9.58) * mm, "end": v(-53.01, -9.68) * mm});
            skLineSegment(sketch, "E249", {"start": v(-53.84, -9.32) * mm, "end": v(-53.87, -9.41) * mm});
            skLineSegment(sketch, "E250", {"start": v(-50.39, -10.2) * mm, "end": v(-50.4, -10.3) * mm});
            skLineSegment(sketch, "E251", {"start": v(-57.96, -7.62) * mm, "end": v(-58, -7.7) * mm});
            skLineSegment(sketch, "E252", {"start": v(-58.75, -7.2) * mm, "end": v(-58.8, -7.28) * mm});
            skLineSegment(sketch, "E253", {"start": v(-41.5, -10.49) * mm, "end": v(-41.5, -10.58) * mm});
            skLineSegment(sketch, "E254", {"start": v(-41.52, -10.34) * mm, "end": v(-41.5, -10.45) * mm});
            skLineSegment(sketch, "E255", {"start": v(-42.4, -10.59) * mm, "end": v(-42.38, -10.68) * mm});
            skLineSegment(sketch, "E256", {"start": v(-42.4, -10.54) * mm, "end": v(-42.4, -10.59) * mm});
            skLineSegment(sketch, "E257", {"start": v(-42.4, -10.44) * mm, "end": v(-42.4, -10.54) * mm});
            skLineSegment(sketch, "E258", {"start": v(-47.74, -10.59) * mm, "end": v(-47.75, -10.68) * mm});
            skLineSegment(sketch, "E259", {"start": v(-45.95, -10.66) * mm, "end": v(-45.96, -10.7) * mm});
            skLineSegment(sketch, "E260", {"start": v(-45.06, -10.67) * mm, "end": v(-45.06, -10.71) * mm});
            skLineSegment(sketch, "E261", {"start": v(-45.06, -10.71) * mm, "end": v(-45.06, -10.8) * mm});
            skLineSegment(sketch, "E262", {"start": v(-45.96, -10.7) * mm, "end": v(-45.96, -10.8) * mm});
            skLineSegment(sketch, "E263", {"start": v(-44.17, -10.7) * mm, "end": v(-44.17, -10.8) * mm});
            skLineSegment(sketch, "E264", {"start": v(-44.17, -10.66) * mm, "end": v(-44.17, -10.7) * mm});
            skLineSegment(sketch, "E265", {"start": v(-46.85, -10.66) * mm, "end": v(-46.85, -10.75) * mm});
            skLineSegment(sketch, "E266", {"start": v(-43.28, -10.66) * mm, "end": v(-43.27, -10.75) * mm});
            skLineSegment(sketch, "E267", {"start": v(-46.84, -10.61) * mm, "end": v(-46.85, -10.66) * mm});
            skLineSegment(sketch, "E268", {"start": v(-43.28, -10.61) * mm, "end": v(-43.28, -10.66) * mm});
            skLineSegment(sketch, "E269", {"start": v(-45.95, -10.55) * mm, "end": v(-45.95, -10.66) * mm});
            skLineSegment(sketch, "E270", {"start": v(-47.73, -10.54) * mm, "end": v(-47.74, -10.59) * mm});
            skLineSegment(sketch, "E271", {"start": v(-44.18, -10.55) * mm, "end": v(-44.17, -10.66) * mm});
            skLineSegment(sketch, "E272", {"start": v(-45.06, -10.56) * mm, "end": v(-45.06, -10.67) * mm});
            skLineSegment(sketch, "E273", {"start": v(-46.84, -10.5) * mm, "end": v(-46.84, -10.61) * mm});
            skLineSegment(sketch, "E274", {"start": v(-43.29, -10.5) * mm, "end": v(-43.28, -10.61) * mm});
            skLineSegment(sketch, "E275", {"start": v(-47.72, -10.44) * mm, "end": v(-47.73, -10.54) * mm});
            skLineSegment(sketch, "E276", {"start": v(-48.6, -10.34) * mm, "end": v(-48.62, -10.45) * mm});
            skLineSegment(sketch, "E277", {"start": v(-48.62, -10.45) * mm, "end": v(-48.62, -10.49) * mm});
            skLineSegment(sketch, "E278", {"start": v(-41.5, -10.45) * mm, "end": v(-41.5, -10.49) * mm});
            skLineSegment(sketch, "E279", {"start": v(-48.62, -10.49) * mm, "end": v(-48.64, -10.58) * mm});
            skLineSegment(sketch, "E280", {"start": v(-48.62, 45.86) * mm, "end": v(-48.64, 45.96) * mm});
            skLineSegment(sketch, "E281", {"start": v(-41.5, 45.82) * mm, "end": v(-41.5, 45.86) * mm});
            skLineSegment(sketch, "E282", {"start": v(-47.72, 45.81) * mm, "end": v(-47.73, 45.92) * mm});
            skLineSegment(sketch, "E283", {"start": v(-42.4, 45.96) * mm, "end": v(-42.38, 46.06) * mm});
            skLineSegment(sketch, "E284", {"start": v(-42.4, 45.92) * mm, "end": v(-42.4, 45.96) * mm});
            skLineSegment(sketch, "E285", {"start": v(-45.06, 46.09) * mm, "end": v(-45.06, 46.18) * mm});
            skLineSegment(sketch, "E286", {"start": v(-45.96, 46.07) * mm, "end": v(-45.96, 46.17) * mm});
            skLineSegment(sketch, "E287", {"start": v(-44.17, 46.07) * mm, "end": v(-44.17, 46.17) * mm});
            skLineSegment(sketch, "E288", {"start": v(-45.06, 46.05) * mm, "end": v(-45.06, 46.09) * mm});
            skLineSegment(sketch, "E289", {"start": v(-44.17, 46.03) * mm, "end": v(-44.17, 46.07) * mm});
            skLineSegment(sketch, "E290", {"start": v(-45.95, 46.03) * mm, "end": v(-45.96, 46.07) * mm});
            skLineSegment(sketch, "E291", {"start": v(-43.28, 46.03) * mm, "end": v(-43.27, 46.13) * mm});
            skLineSegment(sketch, "E292", {"start": v(-46.85, 46.03) * mm, "end": v(-46.85, 46.13) * mm});
            skLineSegment(sketch, "E293", {"start": v(-43.28, 46) * mm, "end": v(-43.28, 46.03) * mm});
            skLineSegment(sketch, "E294", {"start": v(-46.84, 46) * mm, "end": v(-46.85, 46.03) * mm});
            skLineSegment(sketch, "E295", {"start": v(-44.18, 45.92) * mm, "end": v(-44.17, 46.03) * mm});
            skLineSegment(sketch, "E296", {"start": v(-45.95, 45.92) * mm, "end": v(-45.95, 46.03) * mm});
            skLineSegment(sketch, "E297", {"start": v(-45.06, 45.94) * mm, "end": v(-45.06, 46.05) * mm});
            skLineSegment(sketch, "E298", {"start": v(-43.29, 45.88) * mm, "end": v(-43.28, 46) * mm});
            skLineSegment(sketch, "E299", {"start": v(-46.84, 45.88) * mm, "end": v(-46.84, 46) * mm});
            skLineSegment(sketch, "E300", {"start": v(-42.4, 45.81) * mm, "end": v(-42.4, 45.92) * mm});
            skLineSegment(sketch, "E301", {"start": v(-41.52, 45.72) * mm, "end": v(-41.5, 45.82) * mm});
            skLineSegment(sketch, "E302", {"start": v(-47.74, 45.96) * mm, "end": v(-47.75, 46.06) * mm});
            skLineSegment(sketch, "E303", {"start": v(-41.5, 45.86) * mm, "end": v(-41.5, 45.96) * mm});
            skLineSegment(sketch, "E304", {"start": v(-48.62, 45.82) * mm, "end": v(-48.62, 45.86) * mm});
            skLineSegment(sketch, "E305", {"start": v(-48.6, 45.72) * mm, "end": v(-48.62, 45.82) * mm});
            skLineSegment(sketch, "E306", {"start": v(-47.73, 45.92) * mm, "end": v(-47.74, 45.96) * mm});
            skLineSegment(sketch, "E307", {"start": v(-49.5, 45.74) * mm, "end": v(-49.52, 45.83) * mm});
            skLineSegment(sketch, "E308", {"start": v(-49.48, 45.6) * mm, "end": v(-49.5, 45.7) * mm});
            skLineSegment(sketch, "E309", {"start": v(-49.5, -10.36) * mm, "end": v(-49.52, -10.46) * mm});
            skLineSegment(sketch, "E310", {"start": v(-49.5, -10.32) * mm, "end": v(-49.5, -10.36) * mm});
            skLineSegment(sketch, "E311", {"start": v(-49.48, -10.21) * mm, "end": v(-49.5, -10.32) * mm});
            skLineSegment(sketch, "E312", {"start": v(-49.5, 45.7) * mm, "end": v(-49.5, 45.74) * mm});
            skLineSegment(sketch, "E313", {"start": v(-40.62, 45.74) * mm, "end": v(-40.6, 45.83) * mm});
            skLineSegment(sketch, "E314", {"start": v(-40.63, 45.7) * mm, "end": v(-40.62, 45.74) * mm});
            skLineSegment(sketch, "E315", {"start": v(-40.64, 45.6) * mm, "end": v(-40.63, 45.7) * mm});
            skLineSegment(sketch, "E316", {"start": v(-40.63, -10.32) * mm, "end": v(-40.62, -10.36) * mm});
            skLineSegment(sketch, "E317", {"start": v(-40.64, -10.21) * mm, "end": v(-40.63, -10.32) * mm});
            skLineSegment(sketch, "E318", {"start": v(-40.62, -10.36) * mm, "end": v(-40.6, -10.46) * mm});
            skLineSegment(sketch, "E319", {"start": v(-73.46, 17.69) * mm, "end": v(-73.56, 17.69) * mm});
            skLineSegment(sketch, "E320", {"start": v(-73.4, 15.9) * mm, "end": v(-73.5, 15.9) * mm});
            skLineSegment(sketch, "E321", {"start": v(-73.4, 18.58) * mm, "end": v(-73.45, 18.58) * mm});
            skLineSegment(sketch, "E322", {"start": v(-73.42, 17.69) * mm, "end": v(-73.46, 17.69) * mm});
            skLineSegment(sketch, "E323", {"start": v(-73.4, 16.8) * mm, "end": v(-73.45, 16.8) * mm});
            skLineSegment(sketch, "E324", {"start": v(-73.11, 22.13) * mm, "end": v(-73.2, 22.15) * mm});
            skLineSegment(sketch, "E325", {"start": v(-17.05, 13.25) * mm, "end": v(-17.01, 13.25) * mm});
            skLineSegment(sketch, "E326", {"start": v(-73.24, 21.25) * mm, "end": v(-73.34, 21.26) * mm});
            skLineSegment(sketch, "E327", {"start": v(-73.07, 22.12) * mm, "end": v(-73.11, 22.13) * mm});
            skLineSegment(sketch, "E328", {"start": v(-16.76, 19.47) * mm, "end": v(-16.72, 19.47) * mm});
            skLineSegment(sketch, "E329", {"start": v(-17.01, 22.13) * mm, "end": v(-16.92, 22.15) * mm});
            skLineSegment(sketch, "E330", {"start": v(-16.89, 21.25) * mm, "end": v(-16.8, 21.26) * mm});
            skLineSegment(sketch, "E331", {"start": v(-17.05, 22.12) * mm, "end": v(-17.01, 22.13) * mm});
            skLineSegment(sketch, "E332", {"start": v(-16.93, 21.24) * mm, "end": v(-16.89, 21.25) * mm});
            skLineSegment(sketch, "E333", {"start": v(-16.83, 20.36) * mm, "end": v(-16.79, 20.36) * mm});
            skLineSegment(sketch, "E334", {"start": v(-17.04, 21.23) * mm, "end": v(-16.93, 21.24) * mm});
            skLineSegment(sketch, "E335", {"start": v(-16.87, 19.46) * mm, "end": v(-16.76, 19.47) * mm});
            skLineSegment(sketch, "E336", {"start": v(-16.94, 20.35) * mm, "end": v(-16.83, 20.36) * mm});
            skLineSegment(sketch, "E337", {"start": v(-16.83, 18.58) * mm, "end": v(-16.72, 18.58) * mm});
            skLineSegment(sketch, "E338", {"start": v(-16.76, 15.9) * mm, "end": v(-16.72, 15.9) * mm});
            skLineSegment(sketch, "E339", {"start": v(-16.83, 16.8) * mm, "end": v(-16.72, 16.8) * mm});
            skLineSegment(sketch, "E340", {"start": v(-16.81, 17.69) * mm, "end": v(-16.7, 17.69) * mm});
            skLineSegment(sketch, "E341", {"start": v(-17.04, 14.15) * mm, "end": v(-16.93, 14.13) * mm});
            skLineSegment(sketch, "E342", {"start": v(-16.83, 15.02) * mm, "end": v(-16.79, 15.02) * mm});
            skLineSegment(sketch, "E343", {"start": v(-16.94, 15.03) * mm, "end": v(-16.83, 15.02) * mm});
            skLineSegment(sketch, "E344", {"start": v(-16.87, 15.91) * mm, "end": v(-16.76, 15.9) * mm});
            skLineSegment(sketch, "E345", {"start": v(-72.97, 22.1) * mm, "end": v(-73.07, 22.12) * mm});
            skLineSegment(sketch, "E346", {"start": v(-16.93, 14.13) * mm, "end": v(-16.89, 14.13) * mm});
            skLineSegment(sketch, "E347", {"start": v(-73.07, 13.25) * mm, "end": v(-73.11, 13.25) * mm});
            skLineSegment(sketch, "E348", {"start": v(-73.2, 21.24) * mm, "end": v(-73.24, 21.25) * mm});
            skLineSegment(sketch, "E349", {"start": v(-73.2, 14.13) * mm, "end": v(-73.24, 14.13) * mm});
            skLineSegment(sketch, "E350", {"start": v(-73.1, 14.15) * mm, "end": v(-73.2, 14.13) * mm});
            skLineSegment(sketch, "E351", {"start": v(-73.24, 14.13) * mm, "end": v(-73.34, 14.12) * mm});
            skLineSegment(sketch, "E352", {"start": v(-73.26, 15.91) * mm, "end": v(-73.37, 15.9) * mm});
            skLineSegment(sketch, "E353", {"start": v(-73.3, 15.02) * mm, "end": v(-73.34, 15.02) * mm});
            skLineSegment(sketch, "E354", {"start": v(-73.19, 15.03) * mm, "end": v(-73.3, 15.02) * mm});
            skLineSegment(sketch, "E355", {"start": v(-73.37, 15.9) * mm, "end": v(-73.4, 15.9) * mm});
            skLineSegment(sketch, "E356", {"start": v(-73.3, 16.8) * mm, "end": v(-73.4, 16.8) * mm});
            skLineSegment(sketch, "E357", {"start": v(-73.37, 19.47) * mm, "end": v(-73.4, 19.47) * mm});
            skLineSegment(sketch, "E358", {"start": v(-73.3, 18.58) * mm, "end": v(-73.4, 18.58) * mm});
            skLineSegment(sketch, "E359", {"start": v(-73.31, 17.69) * mm, "end": v(-73.42, 17.69) * mm});
            skLineSegment(sketch, "E360", {"start": v(-73.1, 21.23) * mm, "end": v(-73.2, 21.24) * mm});
            skLineSegment(sketch, "E361", {"start": v(-73.3, 20.36) * mm, "end": v(-73.34, 20.36) * mm});
            skLineSegment(sketch, "E362", {"start": v(-73.19, 20.35) * mm, "end": v(-73.3, 20.36) * mm});
            skLineSegment(sketch, "E363", {"start": v(-73.26, 19.46) * mm, "end": v(-73.37, 19.47) * mm});
            skLineSegment(sketch, "E364", {"start": v(-72.97, 13.27) * mm, "end": v(-73.07, 13.25) * mm});
            skLineSegment(sketch, "E365", {"start": v(-73.34, 20.36) * mm, "end": v(-73.43, 20.37) * mm});
            skLineSegment(sketch, "E366", {"start": v(-73.34, 15.02) * mm, "end": v(-73.43, 15) * mm});
            skLineSegment(sketch, "E367", {"start": v(-72.96, 23) * mm, "end": v(-73.06, 23.03) * mm});
            skLineSegment(sketch, "E368", {"start": v(-50.39, 45.59) * mm, "end": v(-50.4, 45.68) * mm});
            skLineSegment(sketch, "E369", {"start": v(-39.74, 45.59) * mm, "end": v(-39.72, 45.68) * mm});
            skLineSegment(sketch, "E370", {"start": v(-17.17, 23) * mm, "end": v(-17.07, 23.03) * mm});
            skLineSegment(sketch, "E371", {"start": v(-17.16, 22.1) * mm, "end": v(-17.05, 22.12) * mm});
            skLineSegment(sketch, "E372", {"start": v(-17.16, 13.27) * mm, "end": v(-17.05, 13.25) * mm});
            skLineSegment(sketch, "E373", {"start": v(-16.7, 17.69) * mm, "end": v(-16.66, 17.69) * mm});
            skLineSegment(sketch, "E374", {"start": v(-16.72, 16.8) * mm, "end": v(-16.68, 16.8) * mm});
            skLineSegment(sketch, "E375", {"start": v(-16.72, 18.58) * mm, "end": v(-16.68, 18.58) * mm});
            skLineSegment(sketch, "E376", {"start": v(-16.79, 20.36) * mm, "end": v(-16.7, 20.37) * mm});
            skLineSegment(sketch, "E377", {"start": v(-17.17, 12.37) * mm, "end": v(-17.07, 12.35) * mm});
            skLineSegment(sketch, "E378", {"start": v(-72.96, 12.37) * mm, "end": v(-73.06, 12.35) * mm});
            skLineSegment(sketch, "E379", {"start": v(-50.36, -10.06) * mm, "end": v(-50.38, -10.17) * mm});
            skLineSegment(sketch, "E380", {"start": v(-39.77, -10.06) * mm, "end": v(-39.75, -10.17) * mm});
            skLineSegment(sketch, "E381", {"start": v(-39.75, -10.17) * mm, "end": v(-39.74, -10.2) * mm});
            skLineSegment(sketch, "E382", {"start": v(-50.38, -10.17) * mm, "end": v(-50.39, -10.2) * mm});
            skLineSegment(sketch, "E383", {"start": v(-38.9, 45.26) * mm, "end": v(-38.88, 45.36) * mm});
            skLineSegment(sketch, "E384", {"start": v(-38.87, 45.4) * mm, "end": v(-38.85, 45.5) * mm});
            skLineSegment(sketch, "E385", {"start": v(-38.88, 45.36) * mm, "end": v(-38.87, 45.4) * mm});
            skLineSegment(sketch, "E386", {"start": v(-17.2, 12.37) * mm, "end": v(-17.17, 12.37) * mm});
            skLineSegment(sketch, "E387", {"start": v(-17.35, 23.88) * mm, "end": v(-17.25, 23.9) * mm});
            skLineSegment(sketch, "E388", {"start": v(-17.56, 24.75) * mm, "end": v(-17.46, 24.78) * mm});
            skLineSegment(sketch, "E389", {"start": v(-17.39, 23.87) * mm, "end": v(-17.35, 23.88) * mm});
            skLineSegment(sketch, "E390", {"start": v(-17.2, 23) * mm, "end": v(-17.17, 23) * mm});
            skLineSegment(sketch, "E391", {"start": v(-17.31, 22.98) * mm, "end": v(-17.2, 23) * mm});
            skLineSegment(sketch, "E392", {"start": v(-17.5, 23.85) * mm, "end": v(-17.39, 23.87) * mm});
            skLineSegment(sketch, "E393", {"start": v(-17.39, 11.5) * mm, "end": v(-17.35, 11.5) * mm});
            skLineSegment(sketch, "E394", {"start": v(-17.5, 11.53) * mm, "end": v(-17.39, 11.5) * mm});
            skLineSegment(sketch, "E395", {"start": v(-17.35, 11.5) * mm, "end": v(-17.25, 11.47) * mm});
            skLineSegment(sketch, "E396", {"start": v(-17.31, 12.4) * mm, "end": v(-17.2, 12.37) * mm});
            skLineSegment(sketch, "E397", {"start": v(-17.8, 25.61) * mm, "end": v(-17.7, 25.64) * mm});
            skLineSegment(sketch, "E398", {"start": v(-18.05, 26.46) * mm, "end": v(-17.96, 26.5) * mm});
            skLineSegment(sketch, "E399", {"start": v(-18.34, 27.3) * mm, "end": v(-18.25, 27.34) * mm});
            skLineSegment(sketch, "E400", {"start": v(-23.18, 35.8) * mm, "end": v(-23.1, 35.85) * mm});
            skLineSegment(sketch, "E401", {"start": v(-31.38, 42.58) * mm, "end": v(-31.34, 42.66) * mm});
            skLineSegment(sketch, "E402", {"start": v(-32.17, 43) * mm, "end": v(-32.13, 43.08) * mm});
            skLineSegment(sketch, "E403", {"start": v(-38, 45.2) * mm, "end": v(-37.98, 45.29) * mm});
            skLineSegment(sketch, "E404", {"start": v(-39.77, 45.44) * mm, "end": v(-39.75, 45.54) * mm});
            skLineSegment(sketch, "E405", {"start": v(-72.92, 23) * mm, "end": v(-72.96, 23) * mm});
            skLineSegment(sketch, "E406", {"start": v(-72.78, 11.5) * mm, "end": v(-72.87, 11.47) * mm});
            skLineSegment(sketch, "E407", {"start": v(-72.57, 10.63) * mm, "end": v(-72.66, 10.6) * mm});
            skLineSegment(sketch, "E408", {"start": v(-72.74, 11.5) * mm, "end": v(-72.78, 11.5) * mm});
            skLineSegment(sketch, "E409", {"start": v(-72.92, 12.37) * mm, "end": v(-72.96, 12.37) * mm});
            skLineSegment(sketch, "E410", {"start": v(-72.81, 12.4) * mm, "end": v(-72.92, 12.37) * mm});
            skLineSegment(sketch, "E411", {"start": v(-72.63, 11.53) * mm, "end": v(-72.74, 11.5) * mm});
            skLineSegment(sketch, "E412", {"start": v(-69.95, 4) * mm, "end": v(-70.04, 3.96) * mm});
            skLineSegment(sketch, "E413", {"start": v(-69.5, 3.23) * mm, "end": v(-69.6, 3.18) * mm});
            skLineSegment(sketch, "E414", {"start": v(-66.95, -0.41) * mm, "end": v(-67.02, -0.48) * mm});
            skLineSegment(sketch, "E415", {"start": v(-66.37, -1.1) * mm, "end": v(-66.44, -1.16) * mm});
            skLineSegment(sketch, "E416", {"start": v(-65.77, -1.75) * mm, "end": v(-65.84, -1.82) * mm});
            skLineSegment(sketch, "E417", {"start": v(-65.15, -2.4) * mm, "end": v(-65.21, -2.46) * mm});
            skLineSegment(sketch, "E418", {"start": v(-63.17, -4.2) * mm, "end": v(-63.23, -4.27) * mm});
            skLineSegment(sketch, "E419", {"start": v(-62.47, -4.75) * mm, "end": v(-62.53, -4.83) * mm});
            skLineSegment(sketch, "E420", {"start": v(-52.13, -9.82) * mm, "end": v(-52.15, -9.91) * mm});
            skLineSegment(sketch, "E421", {"start": v(-38.9, -9.88) * mm, "end": v(-38.88, -9.99) * mm});
            skLineSegment(sketch, "E422", {"start": v(-36.3, -9.28) * mm, "end": v(-36.29, -9.32) * mm});
            skLineSegment(sketch, "E423", {"start": v(-37.14, -9.58) * mm, "end": v(-37.11, -9.68) * mm});
            skLineSegment(sketch, "E424", {"start": v(-37.15, -9.54) * mm, "end": v(-37.14, -9.58) * mm});
            skLineSegment(sketch, "E425", {"start": v(-38.04, -9.67) * mm, "end": v(-38.01, -9.78) * mm});
            skLineSegment(sketch, "E426", {"start": v(-37.18, -9.44) * mm, "end": v(-37.15, -9.54) * mm});
            skLineSegment(sketch, "E427", {"start": v(-36.33, -9.18) * mm, "end": v(-36.3, -9.28) * mm});
            skLineSegment(sketch, "E428", {"start": v(-52.98, -9.54) * mm, "end": v(-52.99, -9.58) * mm});
            skLineSegment(sketch, "E429", {"start": v(-53.8, -9.18) * mm, "end": v(-53.83, -9.28) * mm});
            skLineSegment(sketch, "E430", {"start": v(-52.94, -9.44) * mm, "end": v(-52.98, -9.54) * mm});
            skLineSegment(sketch, "E431", {"start": v(-52.09, -9.67) * mm, "end": v(-52.12, -9.78) * mm});
            skLineSegment(sketch, "E432", {"start": v(-53.83, -9.28) * mm, "end": v(-53.84, -9.32) * mm});
            skLineSegment(sketch, "E433", {"start": v(-36.29, -9.32) * mm, "end": v(-36.26, -9.41) * mm});
            skLineSegment(sketch, "E434", {"start": v(-72.07, 8.91) * mm, "end": v(-72.17, 8.88) * mm});
            skLineSegment(sketch, "E435", {"start": v(-71.93, 26.42) * mm, "end": v(-72.03, 26.45) * mm});
            skLineSegment(sketch, "E436", {"start": v(-72.2, 25.57) * mm, "end": v(-72.3, 25.6) * mm});
            skLineSegment(sketch, "E437", {"start": v(-72.43, 24.71) * mm, "end": v(-72.53, 24.74) * mm});
            skLineSegment(sketch, "E438", {"start": v(-72.34, 9.76) * mm, "end": v(-72.43, 9.74) * mm});
            skLineSegment(sketch, "E439", {"start": v(-72.3, 9.78) * mm, "end": v(-72.34, 9.76) * mm});
            skLineSegment(sketch, "E440", {"start": v(-72.43, 10.66) * mm, "end": v(-72.53, 10.64) * mm});
            skLineSegment(sketch, "E441", {"start": v(-72.2, 9.8) * mm, "end": v(-72.3, 9.78) * mm});
            skLineSegment(sketch, "E442", {"start": v(-71.93, 8.96) * mm, "end": v(-72.03, 8.92) * mm});
            skLineSegment(sketch, "E443", {"start": v(-72.03, 8.92) * mm, "end": v(-72.07, 8.91) * mm});
            skLineSegment(sketch, "E444", {"start": v(-52.09, 45.05) * mm, "end": v(-52.12, 45.16) * mm});
            skLineSegment(sketch, "E445", {"start": v(-52.94, 44.82) * mm, "end": v(-52.98, 44.92) * mm});
            skLineSegment(sketch, "E446", {"start": v(-53.8, 44.56) * mm, "end": v(-53.83, 44.66) * mm});
            skLineSegment(sketch, "E447", {"start": v(-36.33, 44.56) * mm, "end": v(-36.3, 44.66) * mm});
            skLineSegment(sketch, "E448", {"start": v(-37.18, 44.82) * mm, "end": v(-37.15, 44.92) * mm});
            skLineSegment(sketch, "E449", {"start": v(-38.04, 45.05) * mm, "end": v(-38.01, 45.16) * mm});
            skLineSegment(sketch, "E450", {"start": v(-17.7, 24.71) * mm, "end": v(-17.6, 24.74) * mm});
            skLineSegment(sketch, "E451", {"start": v(-17.94, 25.57) * mm, "end": v(-17.83, 25.6) * mm});
            skLineSegment(sketch, "E452", {"start": v(-18.2, 26.42) * mm, "end": v(-18.1, 26.45) * mm});
            skLineSegment(sketch, "E453", {"start": v(-17.8, 9.76) * mm, "end": v(-17.7, 9.74) * mm});
            skLineSegment(sketch, "E454", {"start": v(-17.83, 9.78) * mm, "end": v(-17.8, 9.76) * mm});
            skLineSegment(sketch, "E455", {"start": v(-18.2, 8.96) * mm, "end": v(-18.1, 8.92) * mm});
            skLineSegment(sketch, "E456", {"start": v(-17.94, 9.8) * mm, "end": v(-17.83, 9.78) * mm});
            skLineSegment(sketch, "E457", {"start": v(-17.7, 10.66) * mm, "end": v(-17.6, 10.64) * mm});
            skLineSegment(sketch, "E458", {"start": v(-18.1, 8.92) * mm, "end": v(-18.05, 8.91) * mm});
            skLineSegment(sketch, "E459", {"start": v(-18.05, 8.91) * mm, "end": v(-17.96, 8.88) * mm});
            skLineSegment(sketch, "E460", {"start": v(-18.66, 7.23) * mm, "end": v(-18.57, 7.2) * mm});
            skLineSegment(sketch, "E461", {"start": v(-18.7, 7.25) * mm, "end": v(-18.66, 7.23) * mm});
            skLineSegment(sketch, "E462", {"start": v(-33.78, -8.38) * mm, "end": v(-33.75, -8.46) * mm});
            skLineSegment(sketch, "E463", {"start": v(-33.8, -8.34) * mm, "end": v(-33.78, -8.38) * mm});
            skLineSegment(sketch, "E464", {"start": v(-19.04, 6.43) * mm, "end": v(-19, 6.4) * mm});
            skLineSegment(sketch, "E465", {"start": v(-19.37, 5.6) * mm, "end": v(-19.28, 5.56) * mm});
            skLineSegment(sketch, "E466", {"start": v(-33.04, -7.87) * mm, "end": v(-32.99, -7.97) * mm});
            skLineSegment(sketch, "E467", {"start": v(-19.4, 5.61) * mm, "end": v(-19.37, 5.6) * mm});
            skLineSegment(sketch, "E468", {"start": v(-23.3, 35.7) * mm, "end": v(-23.21, 35.76) * mm});
            skLineSegment(sketch, "E469", {"start": v(-19.5, 29.72) * mm, "end": v(-19.4, 29.76) * mm});
            skLineSegment(sketch, "E470", {"start": v(-19.9, 30.51) * mm, "end": v(-19.8, 30.56) * mm});
            skLineSegment(sketch, "E471", {"start": v(-20.3, 31.3) * mm, "end": v(-20.21, 31.35) * mm});
            skLineSegment(sketch, "E472", {"start": v(-20.75, 32.07) * mm, "end": v(-20.65, 32.12) * mm});
            skLineSegment(sketch, "E473", {"start": v(-21.21, 32.83) * mm, "end": v(-21.12, 32.88) * mm});
            skLineSegment(sketch, "E474", {"start": v(-21.7, 33.57) * mm, "end": v(-21.6, 33.63) * mm});
            skLineSegment(sketch, "E475", {"start": v(-22.2, 34.3) * mm, "end": v(-22.12, 34.36) * mm});
            skLineSegment(sketch, "E476", {"start": v(-22.74, 35) * mm, "end": v(-22.66, 35.07) * mm});
            skLineSegment(sketch, "E477", {"start": v(-27.75, 40.01) * mm, "end": v(-27.68, 40.1) * mm});
            skLineSegment(sketch, "E478", {"start": v(-28.46, 40.54) * mm, "end": v(-28.4, 40.63) * mm});
            skLineSegment(sketch, "E479", {"start": v(-29.18, 41.05) * mm, "end": v(-29.12, 41.14) * mm});
            skLineSegment(sketch, "E480", {"start": v(-29.93, 41.54) * mm, "end": v(-29.87, 41.63) * mm});
            skLineSegment(sketch, "E481", {"start": v(-30.68, 42) * mm, "end": v(-30.63, 42.1) * mm});
            skLineSegment(sketch, "E482", {"start": v(-31.45, 42.44) * mm, "end": v(-31.4, 42.54) * mm});
            skLineSegment(sketch, "E483", {"start": v(-32.24, 42.86) * mm, "end": v(-32.19, 42.96) * mm});
            skLineSegment(sketch, "E484", {"start": v(-57.1, -7.87) * mm, "end": v(-57.14, -7.97) * mm});
            skLineSegment(sketch, "E485", {"start": v(-57.89, -7.48) * mm, "end": v(-57.94, -7.58) * mm});
            skLineSegment(sketch, "E486", {"start": v(-70.23, 4.86) * mm, "end": v(-70.33, 4.81) * mm});
            skLineSegment(sketch, "E487", {"start": v(-70.23, 30.51) * mm, "end": v(-70.33, 30.56) * mm});
            skLineSegment(sketch, "E488", {"start": v(-57.89, 42.86) * mm, "end": v(-57.94, 42.96) * mm});
            skLineSegment(sketch, "E489", {"start": v(-32.17, -7.62) * mm, "end": v(-32.13, -7.7) * mm});
            skLineSegment(sketch, "E490", {"start": v(-32.19, -7.58) * mm, "end": v(-32.17, -7.62) * mm});
            skLineSegment(sketch, "E491", {"start": v(-31.38, -7.2) * mm, "end": v(-31.34, -7.28) * mm});
            skLineSegment(sketch, "E492", {"start": v(-32.24, -7.48) * mm, "end": v(-32.19, -7.58) * mm});
            skLineSegment(sketch, "E493", {"start": v(-19.9, 4.86) * mm, "end": v(-19.8, 4.81) * mm});
            skLineSegment(sketch, "E494", {"start": v(-69.82, 31.3) * mm, "end": v(-69.91, 31.35) * mm});
            skLineSegment(sketch, "E495", {"start": v(-69.82, 4.08) * mm, "end": v(-69.91, 4.03) * mm});
            skLineSegment(sketch, "E496", {"start": v(-58.67, -7.07) * mm, "end": v(-58.73, -7.16) * mm});
            skLineSegment(sketch, "E497", {"start": v(-27.75, -4.63) * mm, "end": v(-27.68, -4.72) * mm});
            skLineSegment(sketch, "E498", {"start": v(-69.38, 3.3) * mm, "end": v(-69.47, 3.25) * mm});
            skLineSegment(sketch, "E499", {"start": v(-68.92, 2.55) * mm, "end": v(-69, 2.5) * mm});
            skLineSegment(sketch, "E500", {"start": v(-68.92, 32.83) * mm, "end": v(-69, 32.88) * mm});
            skLineSegment(sketch, "E501", {"start": v(-69.38, 32.07) * mm, "end": v(-69.47, 32.12) * mm});
            skLineSegment(sketch, "E502", {"start": v(-62.38, -4.63) * mm, "end": v(-62.44, -4.72) * mm});
            skLineSegment(sketch, "E503", {"start": v(-67.92, 1.08) * mm, "end": v(-68, 1.02) * mm});
            skLineSegment(sketch, "E504", {"start": v(-67.92, 34.3) * mm, "end": v(-68, 34.36) * mm});
            skLineSegment(sketch, "E505", {"start": v(-63.07, -4.08) * mm, "end": v(-63.14, -4.16) * mm});
            skLineSegment(sketch, "E506", {"start": v(-60.2, 41.54) * mm, "end": v(-60.26, 41.63) * mm});
            skLineSegment(sketch, "E507", {"start": v(-59.44, 42) * mm, "end": v(-59.5, 42.1) * mm});
            skLineSegment(sketch, "E508", {"start": v(-30.63, -6.72) * mm, "end": v(-30.6, -6.76) * mm});
            skLineSegment(sketch, "E509", {"start": v(-20.62, 3.23) * mm, "end": v(-20.54, 3.18) * mm});
            skLineSegment(sketch, "E510", {"start": v(-20.75, 3.3) * mm, "end": v(-20.65, 3.25) * mm});
            skLineSegment(sketch, "E511", {"start": v(-68.43, 1.8) * mm, "end": v(-68.52, 1.75) * mm});
            skLineSegment(sketch, "E512", {"start": v(-27.06, -4.08) * mm, "end": v(-26.99, -4.16) * mm});
            skLineSegment(sketch, "E513", {"start": v(-21.08, 2.47) * mm, "end": v(-21, 2.42) * mm});
            skLineSegment(sketch, "E514", {"start": v(-68.43, 33.57) * mm, "end": v(-68.52, 33.63) * mm});
            skLineSegment(sketch, "E515", {"start": v(-26.96, -4.2) * mm, "end": v(-26.9, -4.27) * mm});
            skLineSegment(sketch, "E516", {"start": v(-27.66, -4.75) * mm, "end": v(-27.6, -4.83) * mm});
            skLineSegment(sketch, "E517", {"start": v(-28.37, -5.29) * mm, "end": v(-28.31, -5.37) * mm});
            skLineSegment(sketch, "E518", {"start": v(-28.4, -5.25) * mm, "end": v(-28.37, -5.29) * mm});
            skLineSegment(sketch, "E519", {"start": v(-29.1, -5.8) * mm, "end": v(-29.05, -5.88) * mm});
            skLineSegment(sketch, "E520", {"start": v(-29.85, -6.3) * mm, "end": v(-29.8, -6.37) * mm});
            skLineSegment(sketch, "E521", {"start": v(-29.87, -6.26) * mm, "end": v(-29.85, -6.3) * mm});
            skLineSegment(sketch, "E522", {"start": v(-30.68, -6.63) * mm, "end": v(-30.63, -6.72) * mm});
            skLineSegment(sketch, "E523", {"start": v(-29.93, -6.16) * mm, "end": v(-29.87, -6.26) * mm});
            skLineSegment(sketch, "E524", {"start": v(-29.18, -5.68) * mm, "end": v(-29.12, -5.77) * mm});
            skLineSegment(sketch, "E525", {"start": v(-29.12, -5.77) * mm, "end": v(-29.1, -5.8) * mm});
            skLineSegment(sketch, "E526", {"start": v(-28.46, -5.17) * mm, "end": v(-28.4, -5.25) * mm});
            skLineSegment(sketch, "E527", {"start": v(-27.68, -4.72) * mm, "end": v(-27.66, -4.75) * mm});
            skLineSegment(sketch, "E528", {"start": v(-61.67, -5.17) * mm, "end": v(-61.73, -5.25) * mm});
            skLineSegment(sketch, "E529", {"start": v(-60.94, -5.68) * mm, "end": v(-61, -5.77) * mm});
            skLineSegment(sketch, "E530", {"start": v(-60.2, -6.16) * mm, "end": v(-60.26, -6.26) * mm});
            skLineSegment(sketch, "E531", {"start": v(-59.44, -6.63) * mm, "end": v(-59.5, -6.72) * mm});
            skLineSegment(sketch, "E532", {"start": v(-26.99, -4.16) * mm, "end": v(-26.96, -4.2) * mm});
            skLineSegment(sketch, "E533", {"start": v(-20.65, 3.25) * mm, "end": v(-20.62, 3.23) * mm});
            skLineSegment(sketch, "E534", {"start": v(-26.3, -3.58) * mm, "end": v(-26.28, -3.61) * mm});
            skLineSegment(sketch, "E535", {"start": v(-26.38, -3.5) * mm, "end": v(-26.3, -3.58) * mm});
            skLineSegment(sketch, "E536", {"start": v(-63.75, -3.5) * mm, "end": v(-63.82, -3.58) * mm});
            skLineSegment(sketch, "E537", {"start": v(-26.28, -3.61) * mm, "end": v(-26.22, -3.69) * mm});
            skLineSegment(sketch, "E538", {"start": v(-66.83, -0.32) * mm, "end": v(-66.91, -0.39) * mm});
            skLineSegment(sketch, "E539", {"start": v(-66.25, -1) * mm, "end": v(-66.34, -1.07) * mm});
            skLineSegment(sketch, "E540", {"start": v(-65.66, -1.65) * mm, "end": v(-65.74, -1.72) * mm});
            skLineSegment(sketch, "E541", {"start": v(-65.04, -2.29) * mm, "end": v(-65.12, -2.36) * mm});
            skLineSegment(sketch, "E542", {"start": v(-64.4, -2.9) * mm, "end": v(-64.48, -2.98) * mm});
            skLineSegment(sketch, "E543", {"start": v(-21.12, 2.5) * mm, "end": v(-21.08, 2.47) * mm});
            skLineSegment(sketch, "E544", {"start": v(-21.6, 1.75) * mm, "end": v(-21.57, 1.73) * mm});
            skLineSegment(sketch, "E545", {"start": v(-21.7, 1.8) * mm, "end": v(-21.6, 1.75) * mm});
            skLineSegment(sketch, "E546", {"start": v(-21.57, 1.73) * mm, "end": v(-21.5, 1.67) * mm});
            skLineSegment(sketch, "E547", {"start": v(-21.21, 2.55) * mm, "end": v(-21.12, 2.5) * mm});
            skLineSegment(sketch, "E548", {"start": v(-22.12, 1.02) * mm, "end": v(-22.09, 1) * mm});
            skLineSegment(sketch, "E549", {"start": v(-22.09, 1) * mm, "end": v(-22, 0.94) * mm});
            skLineSegment(sketch, "E550", {"start": v(-67.39, 0.37) * mm, "end": v(-67.47, 0.3) * mm});
            skLineSegment(sketch, "E551", {"start": v(-25.73, -2.9) * mm, "end": v(-25.65, -2.98) * mm});
            skLineSegment(sketch, "E552", {"start": v(-25.62, -3.01) * mm, "end": v(-25.56, -3.08) * mm});
            skLineSegment(sketch, "E553", {"start": v(-22.62, 0.28) * mm, "end": v(-22.55, 0.22) * mm});
            skLineSegment(sketch, "E554", {"start": v(-23.18, -0.41) * mm, "end": v(-23.1, -0.48) * mm});
            skLineSegment(sketch, "E555", {"start": v(-23.21, -0.39) * mm, "end": v(-23.18, -0.41) * mm});
            skLineSegment(sketch, "E556", {"start": v(-23.76, -1.1) * mm, "end": v(-23.69, -1.16) * mm});
            skLineSegment(sketch, "E557", {"start": v(-24.36, -1.75) * mm, "end": v(-24.3, -1.82) * mm});
            skLineSegment(sketch, "E558", {"start": v(-24.4, -1.72) * mm, "end": v(-24.36, -1.75) * mm});
            skLineSegment(sketch, "E559", {"start": v(-25.01, -2.36) * mm, "end": v(-24.98, -2.4) * mm});
            skLineSegment(sketch, "E560", {"start": v(-25.09, -2.29) * mm, "end": v(-25.01, -2.36) * mm});
            skLineSegment(sketch, "E561", {"start": v(-24.98, -2.4) * mm, "end": v(-24.91, -2.46) * mm});
            skLineSegment(sketch, "E562", {"start": v(-24.47, -1.65) * mm, "end": v(-24.4, -1.72) * mm});
            skLineSegment(sketch, "E563", {"start": v(-23.87, -1) * mm, "end": v(-23.8, -1.07) * mm});
            skLineSegment(sketch, "E564", {"start": v(-23.8, -1.07) * mm, "end": v(-23.76, -1.1) * mm});
            skLineSegment(sketch, "E565", {"start": v(-23.3, -0.32) * mm, "end": v(-23.21, -0.39) * mm});
            skLineSegment(sketch, "E566", {"start": v(-22.74, 0.37) * mm, "end": v(-22.66, 0.3) * mm});
            skLineSegment(sketch, "E567", {"start": v(-22.66, 0.3) * mm, "end": v(-22.62, 0.28) * mm});
            skLineSegment(sketch, "E568", {"start": v(-25.65, -2.98) * mm, "end": v(-25.62, -3.01) * mm});
            skLineSegment(sketch, "E569", {"start": v(-22.2, 1.08) * mm, "end": v(-22.12, 1.02) * mm});
            skLineSegment(sketch, "E570", {"start": v(-66.83, 35.7) * mm, "end": v(-66.91, 35.76) * mm});
            skLineSegment(sketch, "E571", {"start": v(-67.39, 35) * mm, "end": v(-67.47, 35.07) * mm});
            skLineSegment(sketch, "E572", {"start": v(-60.94, 41.05) * mm, "end": v(-61, 41.14) * mm});
            skLineSegment(sketch, "E573", {"start": v(-61.67, 40.54) * mm, "end": v(-61.73, 40.63) * mm});
            skLineSegment(sketch, "E574", {"start": v(-62.38, 40.01) * mm, "end": v(-62.44, 40.1) * mm});
            skLineSegment(sketch, "E575", {"start": v(-30.6, -6.76) * mm, "end": v(-30.56, -6.84) * mm});
            skLineSegment(sketch, "E576", {"start": v(-31.45, -7.07) * mm, "end": v(-31.4, -7.16) * mm});
            skLineSegment(sketch, "E577", {"start": v(-31.4, -7.16) * mm, "end": v(-31.38, -7.2) * mm});
            skLineSegment(sketch, "E578", {"start": v(-20.3, 4.08) * mm, "end": v(-20.21, 4.03) * mm});
            skLineSegment(sketch, "E579", {"start": v(-58.67, 42.44) * mm, "end": v(-58.73, 42.54) * mm});
            skLineSegment(sketch, "E580", {"start": v(-32.99, -7.97) * mm, "end": v(-32.97, -8) * mm});
            skLineSegment(sketch, "E581", {"start": v(-20.21, 4.03) * mm, "end": v(-20.18, 4) * mm});
            skLineSegment(sketch, "E582", {"start": v(-20.18, 4) * mm, "end": v(-20.1, 3.96) * mm});
            skLineSegment(sketch, "E583", {"start": v(-19.8, 4.81) * mm, "end": v(-19.76, 4.8) * mm});
            skLineSegment(sketch, "E584", {"start": v(-19.76, 4.8) * mm, "end": v(-19.67, 4.75) * mm});
            skLineSegment(sketch, "E585", {"start": v(-19.5, 5.66) * mm, "end": v(-19.4, 5.61) * mm});
            skLineSegment(sketch, "E586", {"start": v(-57.1, 43.25) * mm, "end": v(-57.14, 43.35) * mm});
            skLineSegment(sketch, "E587", {"start": v(-70.62, 29.72) * mm, "end": v(-70.72, 29.76) * mm});
            skLineSegment(sketch, "E588", {"start": v(-33.04, 43.25) * mm, "end": v(-32.99, 43.35) * mm});
            skLineSegment(sketch, "E589", {"start": v(-32.97, -8) * mm, "end": v(-32.93, -8.1) * mm});
            skLineSegment(sketch, "E590", {"start": v(-19.14, 28.9) * mm, "end": v(-19.04, 28.95) * mm});
            skLineSegment(sketch, "E591", {"start": v(-19.14, 6.47) * mm, "end": v(-19.04, 6.43) * mm});
            skLineSegment(sketch, "E592", {"start": v(-56.28, 43.61) * mm, "end": v(-56.33, 43.71) * mm});
            skLineSegment(sketch, "E593", {"start": v(-33.84, 43.61) * mm, "end": v(-33.8, 43.71) * mm});
            skLineSegment(sketch, "E594", {"start": v(-71, 6.47) * mm, "end": v(-71.1, 6.43) * mm});
            skLineSegment(sketch, "E595", {"start": v(-71, 28.9) * mm, "end": v(-71.1, 28.95) * mm});
            skLineSegment(sketch, "E596", {"start": v(-33.84, -8.24) * mm, "end": v(-33.8, -8.34) * mm});
            skLineSegment(sketch, "E597", {"start": v(-56.28, -8.24) * mm, "end": v(-56.33, -8.34) * mm});
            skLineSegment(sketch, "E598", {"start": v(-19, 6.4) * mm, "end": v(-18.91, 6.37) * mm});
            skLineSegment(sketch, "E599", {"start": v(-71.43, 7.25) * mm, "end": v(-71.47, 7.23) * mm});
            skLineSegment(sketch, "E600", {"start": v(-71.64, 8.12) * mm, "end": v(-71.75, 8.08) * mm});
            skLineSegment(sketch, "E601", {"start": v(-71.33, 7.29) * mm, "end": v(-71.43, 7.25) * mm});
            skLineSegment(sketch, "E602", {"start": v(-71.1, 6.43) * mm, "end": v(-71.13, 6.4) * mm});
            skLineSegment(sketch, "E603", {"start": v(-70.33, 4.81) * mm, "end": v(-70.37, 4.8) * mm});
            skLineSegment(sketch, "E604", {"start": v(-69.91, 4.03) * mm, "end": v(-69.95, 4) * mm});
            skLineSegment(sketch, "E605", {"start": v(-69.47, 3.25) * mm, "end": v(-69.5, 3.23) * mm});
            skLineSegment(sketch, "E606", {"start": v(-69, 2.5) * mm, "end": v(-69.04, 2.47) * mm});
            skLineSegment(sketch, "E607", {"start": v(-68.52, 1.75) * mm, "end": v(-68.55, 1.73) * mm});
            skLineSegment(sketch, "E608", {"start": v(-68, 1.02) * mm, "end": v(-68.04, 1) * mm});
            skLineSegment(sketch, "E609", {"start": v(-67.47, 0.3) * mm, "end": v(-67.5, 0.28) * mm});
            skLineSegment(sketch, "E610", {"start": v(-66.91, -0.39) * mm, "end": v(-66.95, -0.41) * mm});
            skLineSegment(sketch, "E611", {"start": v(-66.34, -1.07) * mm, "end": v(-66.37, -1.1) * mm});
            skLineSegment(sketch, "E612", {"start": v(-65.74, -1.72) * mm, "end": v(-65.77, -1.75) * mm});
            skLineSegment(sketch, "E613", {"start": v(-65.12, -2.36) * mm, "end": v(-65.15, -2.4) * mm});
            skLineSegment(sketch, "E614", {"start": v(-64.48, -2.98) * mm, "end": v(-64.5, -3.01) * mm});
            skLineSegment(sketch, "E615", {"start": v(-63.82, -3.58) * mm, "end": v(-63.84, -3.61) * mm});
            skLineSegment(sketch, "E616", {"start": v(-63.14, -4.16) * mm, "end": v(-63.17, -4.2) * mm});
            skLineSegment(sketch, "E617", {"start": v(-62.44, -4.72) * mm, "end": v(-62.47, -4.75) * mm});
            skLineSegment(sketch, "E618", {"start": v(-61.73, -5.25) * mm, "end": v(-61.76, -5.29) * mm});
            skLineSegment(sketch, "E619", {"start": v(-61, -5.77) * mm, "end": v(-61.03, -5.8) * mm});
            skLineSegment(sketch, "E620", {"start": v(-60.26, -6.26) * mm, "end": v(-60.28, -6.3) * mm});
            skLineSegment(sketch, "E621", {"start": v(-59.5, -6.72) * mm, "end": v(-59.52, -6.76) * mm});
            skLineSegment(sketch, "E622", {"start": v(-58.73, -7.16) * mm, "end": v(-58.75, -7.2) * mm});
            skLineSegment(sketch, "E623", {"start": v(-57.94, -7.58) * mm, "end": v(-57.96, -7.62) * mm});
            skLineSegment(sketch, "E624", {"start": v(-57.14, -7.97) * mm, "end": v(-57.16, -8) * mm});
            skLineSegment(sketch, "E625", {"start": v(-57.16, -8) * mm, "end": v(-57.2, -8.1) * mm});
            skLineSegment(sketch, "E626", {"start": v(-56.33, -8.34) * mm, "end": v(-56.34, -8.38) * mm});
            skLineSegment(sketch, "E627", {"start": v(-56.34, -8.38) * mm, "end": v(-56.38, -8.46) * mm});
            skLineSegment(sketch, "E628", {"start": v(-34.66, -8.58) * mm, "end": v(-34.62, -8.68) * mm});
            skLineSegment(sketch, "E629", {"start": v(-18.48, 27.26) * mm, "end": v(-18.38, 27.3) * mm});
            skLineSegment(sketch, "E630", {"start": v(-18.8, 28.09) * mm, "end": v(-18.7, 28.13) * mm});
            skLineSegment(sketch, "E631", {"start": v(-18.8, 7.29) * mm, "end": v(-18.7, 7.25) * mm});
            skLineSegment(sketch, "E632", {"start": v(-18.48, 8.12) * mm, "end": v(-18.38, 8.08) * mm});
            skLineSegment(sketch, "E633", {"start": v(-34.66, 43.95) * mm, "end": v(-34.62, 44.06) * mm});
            skLineSegment(sketch, "E634", {"start": v(-35.5, 44.27) * mm, "end": v(-35.46, 44.37) * mm});
            skLineSegment(sketch, "E635", {"start": v(-55.46, -8.58) * mm, "end": v(-55.5, -8.68) * mm});
            skLineSegment(sketch, "E636", {"start": v(-55.5, -8.68) * mm, "end": v(-55.52, -8.72) * mm});
            skLineSegment(sketch, "E637", {"start": v(-34.62, -8.68) * mm, "end": v(-34.6, -8.72) * mm});
            skLineSegment(sketch, "E638", {"start": v(-34.6, -8.72) * mm, "end": v(-34.57, -8.8) * mm});
            skLineSegment(sketch, "E639", {"start": v(-35.46, -9) * mm, "end": v(-35.44, -9.03) * mm});
            skLineSegment(sketch, "E640", {"start": v(-54.67, -9) * mm, "end": v(-54.68, -9.03) * mm});
            skLineSegment(sketch, "E641", {"start": v(-35.5, -8.9) * mm, "end": v(-35.46, -9) * mm});
            skLineSegment(sketch, "E642", {"start": v(-54.63, -8.9) * mm, "end": v(-54.67, -9) * mm});
            skLineSegment(sketch, "E643", {"start": v(-63.84, -3.61) * mm, "end": v(-63.9, -3.69) * mm});
            skLineSegment(sketch, "E644", {"start": v(-64.5, -3.01) * mm, "end": v(-64.57, -3.08) * mm});
            skLineSegment(sketch, "E645", {"start": v(-67.5, 0.28) * mm, "end": v(-67.58, 0.22) * mm});
            skLineSegment(sketch, "E646", {"start": v(-68.04, 1) * mm, "end": v(-68.12, 0.94) * mm});
            skLineSegment(sketch, "E647", {"start": v(-68.55, 1.73) * mm, "end": v(-68.63, 1.67) * mm});
            skLineSegment(sketch, "E648", {"start": v(-69.04, 2.47) * mm, "end": v(-69.12, 2.42) * mm});
            skLineSegment(sketch, "E649", {"start": v(-70.37, 4.8) * mm, "end": v(-70.45, 4.75) * mm});
            skLineSegment(sketch, "E650", {"start": v(-70.76, 5.6) * mm, "end": v(-70.85, 5.56) * mm});
            skLineSegment(sketch, "E651", {"start": v(-71.13, 6.4) * mm, "end": v(-71.22, 6.37) * mm});
            skLineSegment(sketch, "E652", {"start": v(-71.47, 7.23) * mm, "end": v(-71.56, 7.2) * mm});
            skLineSegment(sketch, "E653", {"start": v(-71.75, 8.08) * mm, "end": v(-71.78, 8.07) * mm});
            skLineSegment(sketch, "E654", {"start": v(-54.63, 44.27) * mm, "end": v(-54.67, 44.37) * mm});
            skLineSegment(sketch, "E655", {"start": v(-55.46, 43.95) * mm, "end": v(-55.5, 44.06) * mm});
            skLineSegment(sketch, "E656", {"start": v(-71.33, 28.09) * mm, "end": v(-71.43, 28.13) * mm});
            skLineSegment(sketch, "E657", {"start": v(-71.64, 27.26) * mm, "end": v(-71.75, 27.3) * mm});
            skLineSegment(sketch, "E658", {"start": v(-18.38, 8.08) * mm, "end": v(-18.34, 8.07) * mm});
            skLineSegment(sketch, "E659", {"start": v(-18.34, 8.07) * mm, "end": v(-18.25, 8.04) * mm});
            skLineSegment(sketch, "E660", {"start": v(-71.78, 8.07) * mm, "end": v(-71.88, 8.04) * mm});
            skLineSegment(sketch, "E661", {"start": v(-35.44, -9.03) * mm, "end": v(-35.41, -9.12) * mm});
            skLineSegment(sketch, "E662", {"start": v(-38.01, -9.78) * mm, "end": v(-38, -9.82) * mm});
            skLineSegment(sketch, "E663", {"start": v(-52.12, -9.78) * mm, "end": v(-52.13, -9.82) * mm});
            skLineSegment(sketch, "E664", {"start": v(-72.53, 10.64) * mm, "end": v(-72.57, 10.63) * mm});
            skLineSegment(sketch, "E665", {"start": v(-17.6, 10.64) * mm, "end": v(-17.56, 10.63) * mm});
            skLineSegment(sketch, "E666", {"start": v(-37.14, 44.96) * mm, "end": v(-37.11, 45.05) * mm});
            skLineSegment(sketch, "E667", {"start": v(-36.29, 44.7) * mm, "end": v(-36.26, 44.8) * mm});
            skLineSegment(sketch, "E668", {"start": v(-35.44, 44.4) * mm, "end": v(-35.41, 44.5) * mm});
            skLineSegment(sketch, "E669", {"start": v(-34.6, 44.1) * mm, "end": v(-34.57, 44.18) * mm});
            skLineSegment(sketch, "E670", {"start": v(-32.97, 43.39) * mm, "end": v(-32.93, 43.47) * mm});
            skLineSegment(sketch, "E671", {"start": v(-22.62, 35.1) * mm, "end": v(-22.55, 35.15) * mm});
            skLineSegment(sketch, "E672", {"start": v(-21.57, 33.65) * mm, "end": v(-21.5, 33.7) * mm});
            skLineSegment(sketch, "E673", {"start": v(-20.18, 31.37) * mm, "end": v(-20.1, 31.42) * mm});
            skLineSegment(sketch, "E674", {"start": v(-19.76, 30.58) * mm, "end": v(-19.67, 30.63) * mm});
            skLineSegment(sketch, "E675", {"start": v(-19.37, 29.78) * mm, "end": v(-19.28, 29.82) * mm});
            skLineSegment(sketch, "E676", {"start": v(-17.6, 24.74) * mm, "end": v(-17.56, 24.75) * mm});
            skLineSegment(sketch, "E677", {"start": v(-17.83, 25.6) * mm, "end": v(-17.8, 25.61) * mm});
            skLineSegment(sketch, "E678", {"start": v(-18.1, 26.45) * mm, "end": v(-18.05, 26.46) * mm});
            skLineSegment(sketch, "E679", {"start": v(-18.38, 27.3) * mm, "end": v(-18.34, 27.3) * mm});
            skLineSegment(sketch, "E680", {"start": v(-18.7, 28.13) * mm, "end": v(-18.66, 28.14) * mm});
            skLineSegment(sketch, "E681", {"start": v(-18.66, 28.14) * mm, "end": v(-18.57, 28.18) * mm});
            skLineSegment(sketch, "E682", {"start": v(-19.04, 28.95) * mm, "end": v(-19, 28.97) * mm});
            skLineSegment(sketch, "E683", {"start": v(-19, 28.97) * mm, "end": v(-18.91, 29) * mm});
            skLineSegment(sketch, "E684", {"start": v(-19.4, 29.76) * mm, "end": v(-19.37, 29.78) * mm});
            skLineSegment(sketch, "E685", {"start": v(-19.8, 30.56) * mm, "end": v(-19.76, 30.58) * mm});
            skLineSegment(sketch, "E686", {"start": v(-20.21, 31.35) * mm, "end": v(-20.18, 31.37) * mm});
            skLineSegment(sketch, "E687", {"start": v(-20.65, 32.12) * mm, "end": v(-20.62, 32.15) * mm});
            skLineSegment(sketch, "E688", {"start": v(-20.62, 32.15) * mm, "end": v(-20.54, 32.2) * mm});
            skLineSegment(sketch, "E689", {"start": v(-21.12, 32.88) * mm, "end": v(-21.08, 32.9) * mm});
            skLineSegment(sketch, "E690", {"start": v(-21.08, 32.9) * mm, "end": v(-21, 32.96) * mm});
            skLineSegment(sketch, "E691", {"start": v(-21.6, 33.63) * mm, "end": v(-21.57, 33.65) * mm});
            skLineSegment(sketch, "E692", {"start": v(-22.12, 34.36) * mm, "end": v(-22.09, 34.38) * mm});
            skLineSegment(sketch, "E693", {"start": v(-22.09, 34.38) * mm, "end": v(-22, 34.44) * mm});
            skLineSegment(sketch, "E694", {"start": v(-22.66, 35.07) * mm, "end": v(-22.62, 35.1) * mm});
            skLineSegment(sketch, "E695", {"start": v(-23.21, 35.76) * mm, "end": v(-23.18, 35.8) * mm});
            skLineSegment(sketch, "E696", {"start": v(-27.68, 40.1) * mm, "end": v(-27.66, 40.13) * mm});
            skLineSegment(sketch, "E697", {"start": v(-27.66, 40.13) * mm, "end": v(-27.6, 40.2) * mm});
            skLineSegment(sketch, "E698", {"start": v(-28.4, 40.63) * mm, "end": v(-28.37, 40.66) * mm});
            skLineSegment(sketch, "E699", {"start": v(-28.37, 40.66) * mm, "end": v(-28.31, 40.74) * mm});
            skLineSegment(sketch, "E700", {"start": v(-29.12, 41.14) * mm, "end": v(-29.1, 41.18) * mm});
            skLineSegment(sketch, "E701", {"start": v(-29.1, 41.18) * mm, "end": v(-29.05, 41.26) * mm});
            skLineSegment(sketch, "E702", {"start": v(-29.87, 41.63) * mm, "end": v(-29.85, 41.67) * mm});
            skLineSegment(sketch, "E703", {"start": v(-29.85, 41.67) * mm, "end": v(-29.8, 41.75) * mm});
            skLineSegment(sketch, "E704", {"start": v(-30.63, 42.1) * mm, "end": v(-30.6, 42.13) * mm});
            skLineSegment(sketch, "E705", {"start": v(-30.6, 42.13) * mm, "end": v(-30.56, 42.22) * mm});
            skLineSegment(sketch, "E706", {"start": v(-31.4, 42.54) * mm, "end": v(-31.38, 42.58) * mm});
            skLineSegment(sketch, "E707", {"start": v(-32.19, 42.96) * mm, "end": v(-32.17, 43) * mm});
            skLineSegment(sketch, "E708", {"start": v(-32.99, 43.35) * mm, "end": v(-32.97, 43.39) * mm});
            skLineSegment(sketch, "E709", {"start": v(-33.8, 43.71) * mm, "end": v(-33.78, 43.75) * mm});
            skLineSegment(sketch, "E710", {"start": v(-33.78, 43.75) * mm, "end": v(-33.75, 43.84) * mm});
            skLineSegment(sketch, "E711", {"start": v(-34.62, 44.06) * mm, "end": v(-34.6, 44.1) * mm});
            skLineSegment(sketch, "E712", {"start": v(-35.46, 44.37) * mm, "end": v(-35.44, 44.4) * mm});
            skLineSegment(sketch, "E713", {"start": v(-36.3, 44.66) * mm, "end": v(-36.29, 44.7) * mm});
            skLineSegment(sketch, "E714", {"start": v(-37.15, 44.92) * mm, "end": v(-37.14, 44.96) * mm});
            skLineSegment(sketch, "E715", {"start": v(-38.01, 45.16) * mm, "end": v(-38, 45.2) * mm});
            skLineSegment(sketch, "E716", {"start": v(-38, -9.82) * mm, "end": v(-37.98, -9.91) * mm});
            skLineSegment(sketch, "E717", {"start": v(-17.56, 10.63) * mm, "end": v(-17.46, 10.6) * mm});
            skLineSegment(sketch, "E718", {"start": v(-51.23, -9.88) * mm, "end": v(-51.25, -9.99) * mm});
            skLineSegment(sketch, "E719", {"start": v(-51.25, -9.99) * mm, "end": v(-51.26, -10.03) * mm});
            skLineSegment(sketch, "E720", {"start": v(-38.88, -9.99) * mm, "end": v(-38.87, -10.03) * mm});
            skLineSegment(sketch, "E721", {"start": v(-38.87, -10.03) * mm, "end": v(-38.85, -10.12) * mm});
            skLineSegment(sketch, "E722", {"start": v(-51.26, -10.03) * mm, "end": v(-51.28, -10.12) * mm});
            skLineSegment(sketch, "E723", {"start": v(-72.63, 23.85) * mm, "end": v(-72.74, 23.87) * mm});
            skLineSegment(sketch, "E724", {"start": v(-72.74, 23.87) * mm, "end": v(-72.78, 23.88) * mm});
            skLineSegment(sketch, "E725", {"start": v(-72.78, 23.88) * mm, "end": v(-72.87, 23.9) * mm});
            skLineSegment(sketch, "E726", {"start": v(-72.34, 25.61) * mm, "end": v(-72.43, 25.64) * mm});
            skLineSegment(sketch, "E727", {"start": v(-70.76, 29.78) * mm, "end": v(-70.85, 29.82) * mm});
            skLineSegment(sketch, "E728", {"start": v(-70.37, 30.58) * mm, "end": v(-70.45, 30.63) * mm});
            skLineSegment(sketch, "E729", {"start": v(-69.5, 32.15) * mm, "end": v(-69.6, 32.2) * mm});
            skLineSegment(sketch, "E730", {"start": v(-68.55, 33.65) * mm, "end": v(-68.63, 33.7) * mm});
            skLineSegment(sketch, "E731", {"start": v(-67.5, 35.1) * mm, "end": v(-67.58, 35.15) * mm});
            skLineSegment(sketch, "E732", {"start": v(-52.13, 45.2) * mm, "end": v(-52.15, 45.29) * mm});
            skLineSegment(sketch, "E733", {"start": v(-51.26, 45.4) * mm, "end": v(-51.28, 45.5) * mm});
            skLineSegment(sketch, "E734", {"start": v(-51.25, 45.36) * mm, "end": v(-51.26, 45.4) * mm});
            skLineSegment(sketch, "E735", {"start": v(-39.75, 45.54) * mm, "end": v(-39.74, 45.59) * mm});
            skLineSegment(sketch, "E736", {"start": v(-50.38, 45.54) * mm, "end": v(-50.39, 45.59) * mm});
            skLineSegment(sketch, "E737", {"start": v(-50.36, 45.44) * mm, "end": v(-50.38, 45.54) * mm});
            skLineSegment(sketch, "E738", {"start": v(-51.23, 45.26) * mm, "end": v(-51.25, 45.36) * mm});
            skLineSegment(sketch, "E739", {"start": v(-52.12, 45.16) * mm, "end": v(-52.13, 45.2) * mm});
            skLineSegment(sketch, "E740", {"start": v(-52.98, 44.92) * mm, "end": v(-52.99, 44.96) * mm});
            skLineSegment(sketch, "E741", {"start": v(-53.83, 44.66) * mm, "end": v(-53.84, 44.7) * mm});
            skLineSegment(sketch, "E742", {"start": v(-54.67, 44.37) * mm, "end": v(-54.68, 44.4) * mm});
            skLineSegment(sketch, "E743", {"start": v(-55.5, 44.06) * mm, "end": v(-55.52, 44.1) * mm});
            skLineSegment(sketch, "E744", {"start": v(-56.33, 43.71) * mm, "end": v(-56.34, 43.75) * mm});
            skLineSegment(sketch, "E745", {"start": v(-57.14, 43.35) * mm, "end": v(-57.16, 43.39) * mm});
            skLineSegment(sketch, "E746", {"start": v(-57.94, 42.96) * mm, "end": v(-57.96, 43) * mm});
            skLineSegment(sketch, "E747", {"start": v(-58.73, 42.54) * mm, "end": v(-58.75, 42.58) * mm});
            skLineSegment(sketch, "E748", {"start": v(-59.5, 42.1) * mm, "end": v(-59.52, 42.13) * mm});
            skLineSegment(sketch, "E749", {"start": v(-60.26, 41.63) * mm, "end": v(-60.28, 41.67) * mm});
            skLineSegment(sketch, "E750", {"start": v(-61, 41.14) * mm, "end": v(-61.03, 41.18) * mm});
            skLineSegment(sketch, "E751", {"start": v(-61.73, 40.63) * mm, "end": v(-61.76, 40.66) * mm});
            skLineSegment(sketch, "E752", {"start": v(-62.44, 40.1) * mm, "end": v(-62.47, 40.13) * mm});
            skLineSegment(sketch, "E753", {"start": v(-66.91, 35.76) * mm, "end": v(-66.95, 35.8) * mm});
            skLineSegment(sketch, "E754", {"start": v(-66.95, 35.8) * mm, "end": v(-67.02, 35.85) * mm});
            skLineSegment(sketch, "E755", {"start": v(-67.47, 35.07) * mm, "end": v(-67.5, 35.1) * mm});
            skLineSegment(sketch, "E756", {"start": v(-68, 34.36) * mm, "end": v(-68.04, 34.38) * mm});
            skLineSegment(sketch, "E757", {"start": v(-68.04, 34.38) * mm, "end": v(-68.12, 34.44) * mm});
            skLineSegment(sketch, "E758", {"start": v(-68.52, 33.63) * mm, "end": v(-68.55, 33.65) * mm});
            skLineSegment(sketch, "E759", {"start": v(-69, 32.88) * mm, "end": v(-69.04, 32.9) * mm});
            skLineSegment(sketch, "E760", {"start": v(-69.04, 32.9) * mm, "end": v(-69.12, 32.96) * mm});
            skLineSegment(sketch, "E761", {"start": v(-69.47, 32.12) * mm, "end": v(-69.5, 32.15) * mm});
            skLineSegment(sketch, "E762", {"start": v(-69.91, 31.35) * mm, "end": v(-69.95, 31.37) * mm});
            skLineSegment(sketch, "E763", {"start": v(-69.95, 31.37) * mm, "end": v(-70.04, 31.42) * mm});
            skLineSegment(sketch, "E764", {"start": v(-70.33, 30.56) * mm, "end": v(-70.37, 30.58) * mm});
            skLineSegment(sketch, "E765", {"start": v(-70.72, 29.76) * mm, "end": v(-70.76, 29.78) * mm});
            skLineSegment(sketch, "E766", {"start": v(-71.1, 28.95) * mm, "end": v(-71.13, 28.97) * mm});
            skLineSegment(sketch, "E767", {"start": v(-71.13, 28.97) * mm, "end": v(-71.22, 29) * mm});
            skLineSegment(sketch, "E768", {"start": v(-71.43, 28.13) * mm, "end": v(-71.47, 28.14) * mm});
            skLineSegment(sketch, "E769", {"start": v(-71.47, 28.14) * mm, "end": v(-71.56, 28.18) * mm});
            skLineSegment(sketch, "E770", {"start": v(-71.75, 27.3) * mm, "end": v(-71.78, 27.3) * mm});
            skLineSegment(sketch, "E771", {"start": v(-71.78, 27.3) * mm, "end": v(-71.88, 27.34) * mm});
            skLineSegment(sketch, "E772", {"start": v(-72.03, 26.45) * mm, "end": v(-72.07, 26.46) * mm});
            skLineSegment(sketch, "E773", {"start": v(-72.07, 26.46) * mm, "end": v(-72.17, 26.5) * mm});
            skLineSegment(sketch, "E774", {"start": v(-72.3, 25.6) * mm, "end": v(-72.34, 25.61) * mm});
            skLineSegment(sketch, "E775", {"start": v(-72.53, 24.74) * mm, "end": v(-72.57, 24.75) * mm});
            skLineSegment(sketch, "E776", {"start": v(-72.57, 24.75) * mm, "end": v(-72.66, 24.78) * mm});
            skLineSegment(sketch, "E777", {"start": v(-72.81, 22.98) * mm, "end": v(-72.92, 23) * mm});
            skLineSegment(sketch, "E778", {"start": v(-39.74, -10.2) * mm, "end": v(-39.72, -10.3) * mm});
            skArc(sketch, "E779", {"start": v(-16.62, 15.9) * mm, "mid": v(-16.6, 16.35) * mm, "end": v(-16.58, 16.8) * mm});
            skArc(sketch, "E780", {"start": v(-16.8, 14.12) * mm, "mid": v(-16.74, 14.56) * mm, "end": v(-16.7, 15) * mm});
            skArc(sketch, "E781", {"start": v(-16.57, 17.69) * mm, "mid": v(-16.57, 18.14) * mm, "end": v(-16.58, 18.58) * mm});
            skArc(sketch, "E782", {"start": v(-73.5, 19.48) * mm, "mid": v(-73.53, 19.03) * mm, "end": v(-73.55, 18.58) * mm});
            skArc(sketch, "E783", {"start": v(-55.55, 44.18) * mm, "mid": v(-55.97, 44.02) * mm, "end": v(-56.38, 43.84) * mm});
            skArc(sketch, "E784", {"start": v(-61.81, 40.74) * mm, "mid": v(-62.17, 40.48) * mm, "end": v(-62.53, 40.2) * mm});
            skArc(sketch, "E785", {"start": v(-60.33, 41.75) * mm, "mid": v(-60.7, 41.5) * mm, "end": v(-61.08, 41.26) * mm});
            skArc(sketch, "E786", {"start": v(-58.8, 42.66) * mm, "mid": v(-59.18, 42.44) * mm, "end": v(-59.57, 42.22) * mm});
            skArc(sketch, "E787", {"start": v(-57.2, 43.47) * mm, "mid": v(-57.6, 43.28) * mm, "end": v(-58, 43.08) * mm});
            skArc(sketch, "E788", {"start": v(-53.87, 44.8) * mm, "mid": v(-54.3, 44.65) * mm, "end": v(-54.72, 44.5) * mm});
            skArc(sketch, "E789", {"start": v(-61.81, -5.37) * mm, "mid": v(-61.45, -5.63) * mm, "end": v(-61.08, -5.88) * mm});
            skArc(sketch, "E790", {"start": v(-60.33, -6.37) * mm, "mid": v(-59.95, -6.6) * mm, "end": v(-59.57, -6.84) * mm});
            skArc(sketch, "E791", {"start": v(-55.55, -8.8) * mm, "mid": v(-55.14, -8.97) * mm, "end": v(-54.72, -9.12) * mm});
            skArc(sketch, "E792", {"start": v(-53.87, -9.41) * mm, "mid": v(-53.44, -9.55) * mm, "end": v(-53.01, -9.68) * mm});
            skArc(sketch, "E793", {"start": v(-50.4, -10.3) * mm, "mid": v(-49.96, -10.38) * mm, "end": v(-49.52, -10.46) * mm});
            skArc(sketch, "E794", {"start": v(-58.8, -7.28) * mm, "mid": v(-58.4, -7.5) * mm, "end": v(-58, -7.7) * mm});
            skArc(sketch, "E795", {"start": v(-45.95, -10.55) * mm, "mid": v(-45.5, -10.56) * mm, "end": v(-45.06, -10.56) * mm});
            skArc(sketch, "E796", {"start": v(-46.85, -10.75) * mm, "mid": v(-46.4, -10.78) * mm, "end": v(-45.96, -10.8) * mm});
            skArc(sketch, "E797", {"start": v(-45.06, -10.8) * mm, "mid": v(-44.62, -10.8) * mm, "end": v(-44.17, -10.8) * mm});
            skArc(sketch, "E798", {"start": v(-44.18, -10.55) * mm, "mid": v(-43.73, -10.53) * mm, "end": v(-43.29, -10.5) * mm});
            skArc(sketch, "E799", {"start": v(-47.72, -10.44) * mm, "mid": v(-47.28, -10.47) * mm, "end": v(-46.84, -10.5) * mm});
            skArc(sketch, "E800", {"start": v(-43.27, -10.75) * mm, "mid": v(-42.83, -10.72) * mm, "end": v(-42.38, -10.68) * mm});
            skArc(sketch, "E801", {"start": v(-42.4, -10.44) * mm, "mid": v(-41.96, -10.4) * mm, "end": v(-41.52, -10.34) * mm});
            skArc(sketch, "E802", {"start": v(-48.64, -10.58) * mm, "mid": v(-48.2, -10.64) * mm, "end": v(-47.75, -10.68) * mm});
            skArc(sketch, "E803", {"start": v(-44.18, 45.92) * mm, "mid": v(-44.62, 45.93) * mm, "end": v(-45.06, 45.94) * mm});
            skArc(sketch, "E804", {"start": v(-45.06, 46.18) * mm, "mid": v(-45.51, 46.18) * mm, "end": v(-45.96, 46.17) * mm});
            skArc(sketch, "E805", {"start": v(-43.27, 46.13) * mm, "mid": v(-43.72, 46.15) * mm, "end": v(-44.17, 46.17) * mm});
            skArc(sketch, "E806", {"start": v(-45.95, 45.92) * mm, "mid": v(-46.4, 45.9) * mm, "end": v(-46.84, 45.88) * mm});
            skArc(sketch, "E807", {"start": v(-42.4, 45.81) * mm, "mid": v(-42.85, 45.85) * mm, "end": v(-43.29, 45.88) * mm});
            skArc(sketch, "E808", {"start": v(-46.85, 46.13) * mm, "mid": v(-47.3, 46.1) * mm, "end": v(-47.75, 46.06) * mm});
            skArc(sketch, "E809", {"start": v(-47.72, 45.81) * mm, "mid": v(-48.16, 45.77) * mm, "end": v(-48.6, 45.72) * mm});
            skArc(sketch, "E810", {"start": v(-41.5, 45.96) * mm, "mid": v(-41.94, 46.01) * mm, "end": v(-42.38, 46.06) * mm});
            skArc(sketch, "E811", {"start": v(-48.64, 45.96) * mm, "mid": v(-49.08, 45.9) * mm, "end": v(-49.52, 45.83) * mm});
            skArc(sketch, "E812", {"start": v(-49.48, -10.21) * mm, "mid": v(-49.04, -10.28) * mm, "end": v(-48.6, -10.34) * mm});
            skArc(sketch, "E813", {"start": v(-40.64, 45.6) * mm, "mid": v(-41.08, 45.66) * mm, "end": v(-41.52, 45.72) * mm});
            skArc(sketch, "E814", {"start": v(-41.5, -10.58) * mm, "mid": v(-41.05, -10.52) * mm, "end": v(-40.6, -10.46) * mm});
            skArc(sketch, "E815", {"start": v(-73.5, 15.9) * mm, "mid": v(-73.47, 15.45) * mm, "end": v(-73.43, 15) * mm});
            skArc(sketch, "E816", {"start": v(-73.56, 17.69) * mm, "mid": v(-73.56, 17.24) * mm, "end": v(-73.55, 16.8) * mm});
            skArc(sketch, "E817", {"start": v(-16.8, 21.26) * mm, "mid": v(-16.85, 21.7) * mm, "end": v(-16.92, 22.15) * mm});
            skArc(sketch, "E818", {"start": v(-16.83, 18.58) * mm, "mid": v(-16.84, 19.02) * mm, "end": v(-16.87, 19.46) * mm});
            skArc(sketch, "E819", {"start": v(-16.94, 20.35) * mm, "mid": v(-16.98, 20.79) * mm, "end": v(-17.04, 21.23) * mm});
            skArc(sketch, "E820", {"start": v(-16.94, 15.03) * mm, "mid": v(-16.9, 15.47) * mm, "end": v(-16.87, 15.91) * mm});
            skArc(sketch, "E821", {"start": v(-16.83, 16.8) * mm, "mid": v(-16.82, 17.24) * mm, "end": v(-16.81, 17.69) * mm});
            skArc(sketch, "E822", {"start": v(-72.97, 22.1) * mm, "mid": v(-73.03, 21.67) * mm, "end": v(-73.1, 21.23) * mm});
            skArc(sketch, "E823", {"start": v(-73.3, 16.8) * mm, "mid": v(-73.28, 16.36) * mm, "end": v(-73.26, 15.91) * mm});
            skArc(sketch, "E824", {"start": v(-73.19, 15.03) * mm, "mid": v(-73.14, 14.59) * mm, "end": v(-73.1, 14.15) * mm});
            skArc(sketch, "E825", {"start": v(-73.19, 20.35) * mm, "mid": v(-73.23, 19.9) * mm, "end": v(-73.26, 19.46) * mm});
            skArc(sketch, "E826", {"start": v(-73.3, 18.58) * mm, "mid": v(-73.31, 18.13) * mm, "end": v(-73.31, 17.69) * mm});
            skArc(sketch, "E827", {"start": v(-73.34, 21.26) * mm, "mid": v(-73.39, 20.82) * mm, "end": v(-73.43, 20.37) * mm});
            skArc(sketch, "E828", {"start": v(-73.34, 14.12) * mm, "mid": v(-73.28, 13.67) * mm, "end": v(-73.2, 13.23) * mm});
            skArc(sketch, "E829", {"start": v(-73.06, 23.03) * mm, "mid": v(-73.14, 22.59) * mm, "end": v(-73.2, 22.15) * mm});
            skArc(sketch, "E830", {"start": v(-50.4, 45.68) * mm, "mid": v(-50.84, 45.6) * mm, "end": v(-51.28, 45.5) * mm});
            skArc(sketch, "E831", {"start": v(-39.72, 45.68) * mm, "mid": v(-40.16, 45.76) * mm, "end": v(-40.6, 45.83) * mm});
            skArc(sketch, "E832", {"start": v(-17.07, 23.03) * mm, "mid": v(-17.16, 23.47) * mm, "end": v(-17.25, 23.9) * mm});
            skArc(sketch, "E833", {"start": v(-17.16, 13.27) * mm, "mid": v(-17.1, 13.7) * mm, "end": v(-17.04, 14.15) * mm});
            skArc(sketch, "E834", {"start": v(-16.62, 19.48) * mm, "mid": v(-16.65, 19.92) * mm, "end": v(-16.7, 20.37) * mm});
            skArc(sketch, "E835", {"start": v(-17.07, 12.35) * mm, "mid": v(-17, 12.79) * mm, "end": v(-16.92, 13.23) * mm});
            skArc(sketch, "E836", {"start": v(-40.64, -10.21) * mm, "mid": v(-40.2, -10.14) * mm, "end": v(-39.77, -10.06) * mm});
            skArc(sketch, "E837", {"start": v(-37.98, 45.29) * mm, "mid": v(-38.41, 45.4) * mm, "end": v(-38.85, 45.5) * mm});
            skArc(sketch, "E838", {"start": v(-31.34, 42.66) * mm, "mid": v(-31.73, 42.87) * mm, "end": v(-32.13, 43.08) * mm});
            skArc(sketch, "E839", {"start": v(-17.16, 22.1) * mm, "mid": v(-17.23, 22.55) * mm, "end": v(-17.31, 22.98) * mm});
            skArc(sketch, "E840", {"start": v(-17.5, 11.53) * mm, "mid": v(-17.4, 11.96) * mm, "end": v(-17.31, 12.4) * mm});
            skArc(sketch, "E841", {"start": v(-17.46, 24.78) * mm, "mid": v(-17.58, 25.2) * mm, "end": v(-17.7, 25.64) * mm});
            skArc(sketch, "E842", {"start": v(-17.96, 26.5) * mm, "mid": v(-18.1, 26.92) * mm, "end": v(-18.25, 27.34) * mm});
            skArc(sketch, "E843", {"start": v(-17.46, 10.6) * mm, "mid": v(-17.35, 11.04) * mm, "end": v(-17.25, 11.47) * mm});
            skArc(sketch, "E844", {"start": v(-65.84, -1.82) * mm, "mid": v(-65.53, -2.14) * mm, "end": v(-65.21, -2.46) * mm});
            skArc(sketch, "E845", {"start": v(-72.66, 10.6) * mm, "mid": v(-72.55, 10.17) * mm, "end": v(-72.43, 9.74) * mm});
            skArc(sketch, "E846", {"start": v(-72.97, 13.27) * mm, "mid": v(-72.9, 12.83) * mm, "end": v(-72.81, 12.4) * mm});
            skArc(sketch, "E847", {"start": v(-72.63, 23.85) * mm, "mid": v(-72.73, 23.42) * mm, "end": v(-72.81, 22.98) * mm});
            skArc(sketch, "E848", {"start": v(-70.04, 3.96) * mm, "mid": v(-69.82, 3.57) * mm, "end": v(-69.6, 3.18) * mm});
            skArc(sketch, "E849", {"start": v(-67.02, -0.48) * mm, "mid": v(-66.73, -0.82) * mm, "end": v(-66.44, -1.16) * mm});
            skArc(sketch, "E850", {"start": v(-63.23, -4.27) * mm, "mid": v(-62.88, -4.55) * mm, "end": v(-62.53, -4.83) * mm});
            skArc(sketch, "E851", {"start": v(-37.18, -9.44) * mm, "mid": v(-36.76, -9.31) * mm, "end": v(-36.33, -9.18) * mm});
            skArc(sketch, "E852", {"start": v(-52.94, -9.44) * mm, "mid": v(-52.52, -9.56) * mm, "end": v(-52.09, -9.67) * mm});
            skArc(sketch, "E853", {"start": v(-36.26, -9.41) * mm, "mid": v(-35.83, -9.27) * mm, "end": v(-35.41, -9.12) * mm});
            skArc(sketch, "E854", {"start": v(-72.17, 8.88) * mm, "mid": v(-72.02, 8.46) * mm, "end": v(-71.88, 8.04) * mm});
            skArc(sketch, "E855", {"start": v(-72.2, 9.8) * mm, "mid": v(-72.06, 9.38) * mm, "end": v(-71.93, 8.96) * mm});
            skArc(sketch, "E856", {"start": v(-72.2, 25.57) * mm, "mid": v(-72.31, 25.14) * mm, "end": v(-72.43, 24.71) * mm});
            skArc(sketch, "E857", {"start": v(-52.94, 44.82) * mm, "mid": v(-53.37, 44.69) * mm, "end": v(-53.8, 44.56) * mm});
            skArc(sketch, "E858", {"start": v(-37.18, 44.82) * mm, "mid": v(-37.6, 44.94) * mm, "end": v(-38.04, 45.05) * mm});
            skArc(sketch, "E859", {"start": v(-17.94, 25.57) * mm, "mid": v(-18.06, 26) * mm, "end": v(-18.2, 26.42) * mm});
            skArc(sketch, "E860", {"start": v(-17.94, 9.8) * mm, "mid": v(-17.81, 10.23) * mm, "end": v(-17.7, 10.66) * mm});
            skArc(sketch, "E861", {"start": v(-17.96, 8.88) * mm, "mid": v(-17.83, 9.3) * mm, "end": v(-17.7, 9.74) * mm});
            skArc(sketch, "E862", {"start": v(-71, 6.47) * mm, "mid": v(-70.81, 6.06) * mm, "end": v(-70.62, 5.66) * mm});
            skArc(sketch, "E863", {"start": v(-19.14, 28.9) * mm, "mid": v(-19.32, 29.31) * mm, "end": v(-19.5, 29.72) * mm});
            skArc(sketch, "E864", {"start": v(-56.28, 43.61) * mm, "mid": v(-56.69, 43.44) * mm, "end": v(-57.1, 43.25) * mm});
            skArc(sketch, "E865", {"start": v(-19.9, 30.51) * mm, "mid": v(-20.1, 30.9) * mm, "end": v(-20.3, 31.3) * mm});
            skArc(sketch, "E866", {"start": v(-20.75, 32.07) * mm, "mid": v(-20.98, 32.45) * mm, "end": v(-21.21, 32.83) * mm});
            skArc(sketch, "E867", {"start": v(-21.7, 33.57) * mm, "mid": v(-21.95, 33.93) * mm, "end": v(-22.2, 34.3) * mm});
            skArc(sketch, "E868", {"start": v(-22.74, 35) * mm, "mid": v(-23.02, 35.35) * mm, "end": v(-23.3, 35.7) * mm});
            skArc(sketch, "E869", {"start": v(-27.75, 40.01) * mm, "mid": v(-28.1, 40.28) * mm, "end": v(-28.46, 40.54) * mm});
            skArc(sketch, "E870", {"start": v(-29.18, 41.05) * mm, "mid": v(-29.55, 41.3) * mm, "end": v(-29.93, 41.54) * mm});
            skArc(sketch, "E871", {"start": v(-30.68, 42) * mm, "mid": v(-31.07, 42.23) * mm, "end": v(-31.45, 42.44) * mm});
            skArc(sketch, "E872", {"start": v(-57.89, -7.48) * mm, "mid": v(-57.5, -7.68) * mm, "end": v(-57.1, -7.87) * mm});
            skArc(sketch, "E873", {"start": v(-70.23, 30.51) * mm, "mid": v(-70.43, 30.12) * mm, "end": v(-70.62, 29.72) * mm});
            skArc(sketch, "E874", {"start": v(-70.23, 4.86) * mm, "mid": v(-70.03, 4.47) * mm, "end": v(-69.82, 4.08) * mm});
            skArc(sketch, "E875", {"start": v(-57.89, 42.86) * mm, "mid": v(-58.28, 42.65) * mm, "end": v(-58.67, 42.44) * mm});
            skArc(sketch, "E876", {"start": v(-19.9, 4.86) * mm, "mid": v(-19.7, 5.26) * mm, "end": v(-19.5, 5.66) * mm});
            skArc(sketch, "E877", {"start": v(-31.34, -7.28) * mm, "mid": v(-30.94, -7.06) * mm, "end": v(-30.56, -6.84) * mm});
            skArc(sketch, "E878", {"start": v(-32.24, -7.48) * mm, "mid": v(-31.84, -7.28) * mm, "end": v(-31.45, -7.07) * mm});
            skArc(sketch, "E879", {"start": v(-32.24, 42.86) * mm, "mid": v(-32.64, 43.06) * mm, "end": v(-33.04, 43.25) * mm});
            skArc(sketch, "E880", {"start": v(-69.38, 3.3) * mm, "mid": v(-69.15, 2.93) * mm, "end": v(-68.92, 2.55) * mm});
            skArc(sketch, "E881", {"start": v(-68.43, 33.57) * mm, "mid": v(-68.68, 33.2) * mm, "end": v(-68.92, 32.83) * mm});
            skArc(sketch, "E882", {"start": v(-63.75, -3.5) * mm, "mid": v(-63.41, -3.8) * mm, "end": v(-63.07, -4.08) * mm});
            skArc(sketch, "E883", {"start": v(-59.44, 42) * mm, "mid": v(-59.82, 41.78) * mm, "end": v(-60.2, 41.54) * mm});
            skArc(sketch, "E884", {"start": v(-67.39, 35) * mm, "mid": v(-67.65, 34.65) * mm, "end": v(-67.92, 34.3) * mm});
            skArc(sketch, "E885", {"start": v(-27.75, -4.63) * mm, "mid": v(-27.4, -4.36) * mm, "end": v(-27.06, -4.08) * mm});
            skArc(sketch, "E886", {"start": v(-68.43, 1.8) * mm, "mid": v(-68.18, 1.44) * mm, "end": v(-67.92, 1.08) * mm});
            skArc(sketch, "E887", {"start": v(-30.68, -6.63) * mm, "mid": v(-30.3, -6.4) * mm, "end": v(-29.93, -6.16) * mm});
            skArc(sketch, "E888", {"start": v(-29.8, -6.37) * mm, "mid": v(-29.42, -6.13) * mm, "end": v(-29.05, -5.88) * mm});
            skArc(sketch, "E889", {"start": v(-29.18, -5.68) * mm, "mid": v(-28.82, -5.42) * mm, "end": v(-28.46, -5.17) * mm});
            skArc(sketch, "E890", {"start": v(-28.31, -5.37) * mm, "mid": v(-27.95, -5.1) * mm, "end": v(-27.6, -4.83) * mm});
            skArc(sketch, "E891", {"start": v(-62.38, -4.63) * mm, "mid": v(-62.03, -4.9) * mm, "end": v(-61.67, -5.17) * mm});
            skArc(sketch, "E892", {"start": v(-60.94, -5.68) * mm, "mid": v(-60.57, -5.92) * mm, "end": v(-60.2, -6.16) * mm});
            skArc(sketch, "E893", {"start": v(-26.9, -4.27) * mm, "mid": v(-26.56, -3.98) * mm, "end": v(-26.22, -3.69) * mm});
            skArc(sketch, "E894", {"start": v(-21, 2.42) * mm, "mid": v(-20.77, 2.8) * mm, "end": v(-20.54, 3.18) * mm});
            skArc(sketch, "E895", {"start": v(-26.38, -3.5) * mm, "mid": v(-26.05, -3.2) * mm, "end": v(-25.73, -2.9) * mm});
            skArc(sketch, "E896", {"start": v(-65.04, -2.29) * mm, "mid": v(-64.72, -2.6) * mm, "end": v(-64.4, -2.9) * mm});
            skArc(sketch, "E897", {"start": v(-67.39, 0.37) * mm, "mid": v(-67.11, 0.03) * mm, "end": v(-66.83, -0.32) * mm});
            skArc(sketch, "E898", {"start": v(-66.25, -1) * mm, "mid": v(-65.96, -1.32) * mm, "end": v(-65.66, -1.65) * mm});
            skArc(sketch, "E899", {"start": v(-21.7, 1.8) * mm, "mid": v(-21.45, 2.18) * mm, "end": v(-21.21, 2.55) * mm});
            skArc(sketch, "E900", {"start": v(-22, 0.94) * mm, "mid": v(-21.75, 1.3) * mm, "end": v(-21.5, 1.67) * mm});
            skArc(sketch, "E901", {"start": v(-25.09, -2.29) * mm, "mid": v(-24.78, -1.97) * mm, "end": v(-24.47, -1.65) * mm});
            skArc(sketch, "E902", {"start": v(-24.3, -1.82) * mm, "mid": v(-23.99, -1.5) * mm, "end": v(-23.69, -1.16) * mm});
            skArc(sketch, "E903", {"start": v(-23.87, -1) * mm, "mid": v(-23.58, -0.66) * mm, "end": v(-23.3, -0.32) * mm});
            skArc(sketch, "E904", {"start": v(-23.1, -0.48) * mm, "mid": v(-22.82, -0.13) * mm, "end": v(-22.55, 0.22) * mm});
            skArc(sketch, "E905", {"start": v(-22.74, 0.37) * mm, "mid": v(-22.47, 0.73) * mm, "end": v(-22.2, 1.08) * mm});
            skArc(sketch, "E906", {"start": v(-25.56, -3.08) * mm, "mid": v(-25.23, -2.78) * mm, "end": v(-24.91, -2.46) * mm});
            skArc(sketch, "E907", {"start": v(-62.38, 40.01) * mm, "mid": v(-62.53, 39.89) * mm, "end": v(-62.69, 39.77) * mm});
            skArc(sketch, "E908", {"start": v(-60.94, 41.05) * mm, "mid": v(-61.3, 40.8) * mm, "end": v(-61.67, 40.54) * mm});
            skArc(sketch, "E909", {"start": v(-20.75, 3.3) * mm, "mid": v(-20.52, 3.7) * mm, "end": v(-20.3, 4.08) * mm});
            skArc(sketch, "E910", {"start": v(-69.38, 32.07) * mm, "mid": v(-69.6, 31.69) * mm, "end": v(-69.82, 31.3) * mm});
            skArc(sketch, "E911", {"start": v(-59.44, -6.63) * mm, "mid": v(-59.06, -6.85) * mm, "end": v(-58.67, -7.07) * mm});
            skArc(sketch, "E912", {"start": v(-20.1, 3.96) * mm, "mid": v(-19.88, 4.35) * mm, "end": v(-19.67, 4.75) * mm});
            skArc(sketch, "E913", {"start": v(-32.93, -8.1) * mm, "mid": v(-32.53, -7.9) * mm, "end": v(-32.13, -7.7) * mm});
            skArc(sketch, "E914", {"start": v(-33.84, -8.24) * mm, "mid": v(-33.44, -8.06) * mm, "end": v(-33.04, -7.87) * mm});
            skArc(sketch, "E915", {"start": v(-19.28, 5.56) * mm, "mid": v(-19.1, 5.96) * mm, "end": v(-18.91, 6.37) * mm});
            skArc(sketch, "E916", {"start": v(-71.29, 17.69) * mm, "mid": v(-36, -6.92) * mm, "end": v(-25.1, 34.69) * mm});
            skArc(sketch, "E917", {"start": v(-28.7, 38.18) * mm, "mid": v(-45.06, 43.91) * mm, "end": v(-61.42, 38.18) * mm});
            skArc(sketch, "E918", {"start": v(-65.03, 34.69) * mm, "mid": v(-69.67, 26.74) * mm, "end": v(-71.29, 17.69) * mm});
            skArc(sketch, "E919", {"start": v(-19.14, 6.47) * mm, "mid": v(-18.96, 6.88) * mm, "end": v(-18.8, 7.29) * mm});
            skArc(sketch, "E920", {"start": v(-33.84, 43.61) * mm, "mid": v(-34.25, 43.79) * mm, "end": v(-34.66, 43.95) * mm});
            skArc(sketch, "E921", {"start": v(-71, 28.9) * mm, "mid": v(-71.16, 28.5) * mm, "end": v(-71.33, 28.09) * mm});
            skArc(sketch, "E922", {"start": v(-56.28, -8.24) * mm, "mid": v(-55.87, -8.41) * mm, "end": v(-55.46, -8.58) * mm});
            skArc(sketch, "E923", {"start": v(-71.64, 8.12) * mm, "mid": v(-71.49, 7.7) * mm, "end": v(-71.33, 7.29) * mm});
            skArc(sketch, "E924", {"start": v(-57.2, -8.1) * mm, "mid": v(-56.8, -8.28) * mm, "end": v(-56.38, -8.46) * mm});
            skArc(sketch, "E925", {"start": v(-18.48, 27.26) * mm, "mid": v(-18.64, 27.67) * mm, "end": v(-18.8, 28.09) * mm});
            skArc(sketch, "E926", {"start": v(-34.57, -8.8) * mm, "mid": v(-34.16, -8.64) * mm, "end": v(-33.75, -8.46) * mm});
            skArc(sketch, "E927", {"start": v(-71.56, 7.2) * mm, "mid": v(-71.4, 6.78) * mm, "end": v(-71.22, 6.37) * mm});
            skArc(sketch, "E928", {"start": v(-69.12, 2.42) * mm, "mid": v(-68.88, 2.04) * mm, "end": v(-68.63, 1.67) * mm});
            skArc(sketch, "E929", {"start": v(-68.12, 0.94) * mm, "mid": v(-67.85, 0.58) * mm, "end": v(-67.58, 0.22) * mm});
            skArc(sketch, "E930", {"start": v(-35.5, -8.9) * mm, "mid": v(-35.08, -8.74) * mm, "end": v(-34.66, -8.58) * mm});
            skArc(sketch, "E931", {"start": v(-64.57, -3.08) * mm, "mid": v(-64.24, -3.39) * mm, "end": v(-63.9, -3.69) * mm});
            skArc(sketch, "E932", {"start": v(-70.85, 5.56) * mm, "mid": v(-70.65, 5.15) * mm, "end": v(-70.45, 4.75) * mm});
            skArc(sketch, "E933", {"start": v(-54.63, 44.27) * mm, "mid": v(-55.05, 44.11) * mm, "end": v(-55.46, 43.95) * mm});
            skArc(sketch, "E934", {"start": v(-71.87, 17.69) * mm, "mid": v(-35.75, -7.45) * mm, "end": v(-24.72, 35.15) * mm});
            skArc(sketch, "E935", {"start": v(-28.34, 38.64) * mm, "mid": v(-45.06, 44.5) * mm, "end": v(-61.79, 38.64) * mm});
            skArc(sketch, "E936", {"start": v(-65.4, 35.15) * mm, "mid": v(-70.2, 27) * mm, "end": v(-71.87, 17.69) * mm});
            skArc(sketch, "E937", {"start": v(-18.57, 7.2) * mm, "mid": v(-18.4, 7.62) * mm, "end": v(-18.25, 8.04) * mm});
            skArc(sketch, "E938", {"start": v(-18.48, 8.12) * mm, "mid": v(-18.34, 8.54) * mm, "end": v(-18.2, 8.96) * mm});
            skArc(sketch, "E939", {"start": v(-35.5, 44.27) * mm, "mid": v(-35.91, 44.42) * mm, "end": v(-36.33, 44.56) * mm});
            skArc(sketch, "E940", {"start": v(-71.64, 27.26) * mm, "mid": v(-71.8, 26.84) * mm, "end": v(-71.93, 26.42) * mm});
            skArc(sketch, "E941", {"start": v(-54.63, -8.9) * mm, "mid": v(-54.21, -9.04) * mm, "end": v(-53.8, -9.18) * mm});
            skArc(sketch, "E942", {"start": v(-72.56, 17.69) * mm, "mid": v(-35.45, -8.08) * mm, "end": v(-24.29, 35.7) * mm});
            skArc(sketch, "E943", {"start": v(-27.9, 39.18) * mm, "mid": v(-45.06, 45.19) * mm, "end": v(-62.22, 39.18) * mm});
            skArc(sketch, "E944", {"start": v(-65.84, 35.7) * mm, "mid": v(-70.83, 27.3) * mm, "end": v(-72.56, 17.69) * mm});
            skArc(sketch, "E945", {"start": v(-38.9, -9.88) * mm, "mid": v(-38.47, -9.78) * mm, "end": v(-38.04, -9.67) * mm});
            skArc(sketch, "E946", {"start": v(-36.26, 44.8) * mm, "mid": v(-36.68, 44.93) * mm, "end": v(-37.11, 45.05) * mm});
            skArc(sketch, "E947", {"start": v(-34.57, 44.18) * mm, "mid": v(-35, 44.35) * mm, "end": v(-35.41, 44.5) * mm});
            skArc(sketch, "E948", {"start": v(-17.5, 23.85) * mm, "mid": v(-17.6, 24.28) * mm, "end": v(-17.7, 24.71) * mm});
            skArc(sketch, "E949", {"start": v(-18.57, 28.18) * mm, "mid": v(-18.74, 28.6) * mm, "end": v(-18.91, 29) * mm});
            skArc(sketch, "E950", {"start": v(-19.28, 29.82) * mm, "mid": v(-19.47, 30.23) * mm, "end": v(-19.67, 30.63) * mm});
            skArc(sketch, "E951", {"start": v(-20.1, 31.42) * mm, "mid": v(-20.31, 31.8) * mm, "end": v(-20.54, 32.2) * mm});
            skArc(sketch, "E952", {"start": v(-21, 32.96) * mm, "mid": v(-21.25, 33.33) * mm, "end": v(-21.5, 33.7) * mm});
            skArc(sketch, "E953", {"start": v(-22, 34.44) * mm, "mid": v(-22.28, 34.8) * mm, "end": v(-22.55, 35.15) * mm});
            skArc(sketch, "E954", {"start": v(-23.1, 35.85) * mm, "mid": v(-23.38, 36.18) * mm, "end": v(-23.65, 36.5) * mm});
            skArc(sketch, "E955", {"start": v(-27.29, 39.96) * mm, "mid": v(-27.44, 40.08) * mm, "end": v(-27.6, 40.2) * mm});
            skArc(sketch, "E956", {"start": v(-28.31, 40.74) * mm, "mid": v(-28.68, 41) * mm, "end": v(-29.05, 41.26) * mm});
            skArc(sketch, "E957", {"start": v(-29.8, 41.75) * mm, "mid": v(-30.17, 41.99) * mm, "end": v(-30.56, 42.22) * mm});
            skArc(sketch, "E958", {"start": v(-32.93, 43.47) * mm, "mid": v(-33.34, 43.66) * mm, "end": v(-33.75, 43.84) * mm});
            skArc(sketch, "E959", {"start": v(-51.23, 45.26) * mm, "mid": v(-51.66, 45.16) * mm, "end": v(-52.09, 45.05) * mm});
            skArc(sketch, "E960", {"start": v(-72.63, 11.53) * mm, "mid": v(-72.53, 11.1) * mm, "end": v(-72.43, 10.66) * mm});
            skArc(sketch, "E961", {"start": v(-37.98, -9.91) * mm, "mid": v(-37.54, -9.8) * mm, "end": v(-37.11, -9.68) * mm});
            skArc(sketch, "E962", {"start": v(-51.23, -9.88) * mm, "mid": v(-50.8, -9.97) * mm, "end": v(-50.36, -10.06) * mm});
            skArc(sketch, "E963", {"start": v(-52.15, -9.91) * mm, "mid": v(-51.72, -10.02) * mm, "end": v(-51.28, -10.12) * mm});
            skArc(sketch, "E964", {"start": v(-73, 17.69) * mm, "mid": v(-35.26, -8.48) * mm, "end": v(-24, 36.06) * mm});
            skArc(sketch, "E965", {"start": v(-72.66, 24.78) * mm, "mid": v(-72.77, 24.34) * mm, "end": v(-72.87, 23.9) * mm});
            skArc(sketch, "E966", {"start": v(-72.17, 26.5) * mm, "mid": v(-72.3, 26.07) * mm, "end": v(-72.43, 25.64) * mm});
            skArc(sketch, "E967", {"start": v(-49.48, 45.6) * mm, "mid": v(-49.92, 45.52) * mm, "end": v(-50.36, 45.44) * mm});
            skArc(sketch, "E968", {"start": v(-38.9, 45.26) * mm, "mid": v(-39.33, 45.35) * mm, "end": v(-39.77, 45.44) * mm});
            skArc(sketch, "E969", {"start": v(-52.15, 45.29) * mm, "mid": v(-52.58, 45.17) * mm, "end": v(-53.01, 45.05) * mm});
            skArc(sketch, "E970", {"start": v(-67.02, 35.85) * mm, "mid": v(-67.3, 35.5) * mm, "end": v(-67.58, 35.15) * mm});
            skArc(sketch, "E971", {"start": v(-66.32, 36.3) * mm, "mid": v(-66.58, 36) * mm, "end": v(-66.83, 35.7) * mm});
            skArc(sketch, "E972", {"start": v(-68.12, 34.44) * mm, "mid": v(-68.38, 34.07) * mm, "end": v(-68.63, 33.7) * mm});
            skArc(sketch, "E973", {"start": v(-69.12, 32.96) * mm, "mid": v(-69.36, 32.58) * mm, "end": v(-69.6, 32.2) * mm});
            skArc(sketch, "E974", {"start": v(-70.04, 31.42) * mm, "mid": v(-70.25, 31.02) * mm, "end": v(-70.45, 30.63) * mm});
            skArc(sketch, "E975", {"start": v(-70.85, 29.82) * mm, "mid": v(-71.04, 29.42) * mm, "end": v(-71.22, 29) * mm});
            skArc(sketch, "E976", {"start": v(-71.56, 28.18) * mm, "mid": v(-71.72, 27.76) * mm, "end": v(-71.88, 27.34) * mm});
            skArc(sketch, "E977", {"start": v(-27.63, 39.53) * mm, "mid": v(-45.06, 45.63) * mm, "end": v(-62.5, 39.53) * mm});
            skArc(sketch, "E978", {"start": v(-66.12, 36.06) * mm, "mid": v(-71.23, 27.5) * mm, "end": v(-73, 17.69) * mm});
            skArc(sketch, "E979", {"start": v(-73.06, 12.35) * mm, "mid": v(-72.97, 11.9) * mm, "end": v(-72.87, 11.47) * mm});
            skArc(sketch, "E980", {"start": v(-39.72, -10.3) * mm, "mid": v(-39.28, -10.22) * mm, "end": v(-38.85, -10.12) * mm});
            skLineSegment(sketch, "E981", {"start": v(-62.66, 39.73) * mm, "end": v(-62.69, 39.77) * mm});
            skLineSegment(sketch, "E982", {"start": v(-62.6, 39.65) * mm, "end": v(-62.65, 39.71) * mm});
            skLineSegment(sketch, "E983", {"start": v(-61.72, 38.55) * mm, "end": v(-61.68, 38.5) * mm});
            skLineSegment(sketch, "E984", {"start": v(-61.72, 38.55) * mm, "end": v(-61.9, 38.77) * mm});
            skLineSegment(sketch, "E985", {"start": v(-61.9, 38.77) * mm, "end": v(-61.9, 38.77) * mm});
            skLineSegment(sketch, "E986", {"start": v(-62.14, 39.09) * mm, "end": v(-62.24, 39.21) * mm});
            skLineSegment(sketch, "E987", {"start": v(-62.24, 39.21) * mm, "end": v(-62.32, 39.3) * mm});
            skLineSegment(sketch, "E988", {"start": v(-62.32, 39.3) * mm, "end": v(-62.33, 39.32) * mm});
            skLineSegment(sketch, "E989", {"start": v(-62.04, 38.95) * mm, "end": v(-62.04, 38.95) * mm});
            skLineSegment(sketch, "E990", {"start": v(-62.04, 38.95) * mm, "end": v(-62.07, 38.99) * mm});
            skLineSegment(sketch, "E991", {"start": v(-61.9, 38.77) * mm, "end": v(-61.94, 38.83) * mm});
            skLineSegment(sketch, "E992", {"start": v(-61.94, 38.83) * mm, "end": v(-62.04, 38.95) * mm});
            skLineSegment(sketch, "E993", {"start": v(-62.07, 38.99) * mm, "end": v(-62.14, 39.09) * mm});
            skLineSegment(sketch, "E994", {"start": v(-61.68, 38.5) * mm, "end": v(-61.62, 38.42) * mm});
            skLineSegment(sketch, "E995", {"start": v(-61.62, 38.42) * mm, "end": v(-61.61, 38.42) * mm});
            skLineSegment(sketch, "E996", {"start": v(-61.61, 38.42) * mm, "end": v(-61.54, 38.33) * mm});
            skLineSegment(sketch, "E997", {"start": v(-61.54, 38.33) * mm, "end": v(-61.54, 38.33) * mm});
            skLineSegment(sketch, "E998", {"start": v(-61.54, 38.33) * mm, "end": v(-61.3, 38.03) * mm});
            skLineSegment(sketch, "E999", {"start": v(-62.33, 39.32) * mm, "end": v(-62.53, 39.57) * mm});
            skLineSegment(sketch, "E1000", {"start": v(-61.67, 37.2) * mm, "end": v(-61.04, 37.7) * mm});
            skLineSegment(sketch, "E1001", {"start": v(-62.53, 39.57) * mm, "end": v(-62.6, 39.65) * mm});
            skLineSegment(sketch, "E1002", {"start": v(-62.65, 39.71) * mm, "end": v(-62.66, 39.73) * mm});
            skLineSegment(sketch, "E1003", {"start": v(-61.67, 37.2) * mm, "end": v(-57.92, 32.51) * mm});
            skLineSegment(sketch, "E1004", {"start": v(-61.04, 37.7) * mm, "end": v(-61.3, 38.03) * mm});
            skLineSegment(sketch, "E1005", {"start": v(-57.92, 32.51) * mm, "end": v(-57.95, 32.5) * mm});
            skLineSegment(sketch, "E1006", {"start": v(-57.49, 33.25) * mm, "end": v(-61.04, 37.7) * mm});
            skLineSegment(sketch, "E1007", {"start": v(-57.53, 32.83) * mm, "end": v(-57.92, 32.51) * mm});
            skLineSegment(sketch, "E1008", {"start": v(-62.69, 39.77) * mm, "end": v(-62.9, 40.04) * mm});
            skLineSegment(sketch, "E1009", {"start": v(-63.31, 40.55) * mm, "end": v(-62.95, 40.1) * mm});
            skLineSegment(sketch, "E1010", {"start": v(-62.95, 40.1) * mm, "end": v(-62.9, 40.04) * mm});
            skLineSegment(sketch, "E1011", {"start": v(-66.86, 36.97) * mm, "end": v(-66.81, 36.92) * mm});
            skLineSegment(sketch, "E1012", {"start": v(-63.31, 40.55) * mm, "end": v(-63.5, 40.78) * mm});
            skLineSegment(sketch, "E1013", {"start": v(-63.5, 40.78) * mm, "end": v(-63.55, 40.85) * mm});
            skLineSegment(sketch, "E1014", {"start": v(-63.55, 40.85) * mm, "end": v(-63.93, 41.33) * mm});
            skLineSegment(sketch, "E1015", {"start": v(-66.23, 36.19) * mm, "end": v(-66.24, 36.2) * mm});
            skLineSegment(sketch, "E1016", {"start": v(-62.04, 38.95) * mm, "end": v(-65.94, 35.83) * mm});
            skLineSegment(sketch, "E1017", {"start": v(-66.55, 36.6) * mm, "end": v(-66.57, 36.61) * mm});
            skLineSegment(sketch, "E1018", {"start": v(-65.97, 35.87) * mm, "end": v(-66.05, 35.97) * mm});
            skLineSegment(sketch, "E1019", {"start": v(-61.68, 38.5) * mm, "end": v(-65.59, 35.39) * mm});
            skLineSegment(sketch, "E1020", {"start": v(-63.55, 40.85) * mm, "end": v(-67.46, 37.73) * mm});
            skLineSegment(sketch, "E1021", {"start": v(-65.85, 35.72) * mm, "end": v(-65.94, 35.83) * mm});
            skLineSegment(sketch, "E1022", {"start": v(-65.63, 35.43) * mm, "end": v(-65.59, 35.39) * mm});
            skLineSegment(sketch, "E1023", {"start": v(-65.52, 35.3) * mm, "end": v(-65.52, 35.3) * mm});
            skLineSegment(sketch, "E1024", {"start": v(-65.52, 35.3) * mm, "end": v(-65.45, 35.21) * mm});
            skLineSegment(sketch, "E1025", {"start": v(-65.45, 35.21) * mm, "end": v(-65.21, 34.91) * mm});
            skLineSegment(sketch, "E1026", {"start": v(-67.84, 38.2) * mm, "end": v(-63.93, 41.33) * mm});
            skLineSegment(sketch, "E1027", {"start": v(-66.24, 36.2) * mm, "end": v(-66.32, 36.3) * mm});
            skLineSegment(sketch, "E1028", {"start": v(-64.95, 34.58) * mm, "end": v(-65.21, 34.91) * mm});
            skLineSegment(sketch, "E1029", {"start": v(-65.45, 35.21) * mm, "end": v(-65.45, 35.21) * mm});
            skLineSegment(sketch, "E1030", {"start": v(-65.59, 35.39) * mm, "end": v(-65.52, 35.3) * mm});
            skLineSegment(sketch, "E1031", {"start": v(-64.95, 34.58) * mm, "end": v(-64, 35.34) * mm});
            skLineSegment(sketch, "E1032", {"start": v(-65.63, 35.43) * mm, "end": v(-65.8, 35.65) * mm});
            skLineSegment(sketch, "E1033", {"start": v(-65.8, 35.65) * mm, "end": v(-65.8, 35.65) * mm});
            skLineSegment(sketch, "E1034", {"start": v(-65.8, 35.65) * mm, "end": v(-65.85, 35.72) * mm});
            skLineSegment(sketch, "E1035", {"start": v(-65.94, 35.83) * mm, "end": v(-65.95, 35.83) * mm});
            skLineSegment(sketch, "E1036", {"start": v(-65.95, 35.83) * mm, "end": v(-65.97, 35.87) * mm});
            skLineSegment(sketch, "E1037", {"start": v(-66.05, 35.97) * mm, "end": v(-66.15, 36.1) * mm});
            skLineSegment(sketch, "E1038", {"start": v(-66.15, 36.1) * mm, "end": v(-66.23, 36.19) * mm});
            skLineSegment(sketch, "E1039", {"start": v(-66.32, 36.3) * mm, "end": v(-66.44, 36.45) * mm});
            skLineSegment(sketch, "E1040", {"start": v(-66.5, 36.53) * mm, "end": v(-66.55, 36.6) * mm});
            skLineSegment(sketch, "E1041", {"start": v(-66.57, 36.61) * mm, "end": v(-66.81, 36.92) * mm});
            skLineSegment(sketch, "E1042", {"start": v(-66.44, 36.45) * mm, "end": v(-66.5, 36.53) * mm});
            skLineSegment(sketch, "E1043", {"start": v(-67.22, 37.43) * mm, "end": v(-66.86, 36.97) * mm});
            skLineSegment(sketch, "E1044", {"start": v(-67.22, 37.43) * mm, "end": v(-67.4, 37.66) * mm});
            skLineSegment(sketch, "E1045", {"start": v(-67.4, 37.66) * mm, "end": v(-67.46, 37.73) * mm});
            skLineSegment(sketch, "E1046", {"start": v(-67.46, 37.73) * mm, "end": v(-67.84, 38.2) * mm});
            skLineSegment(sketch, "E1047", {"start": v(-63.66, 35.36) * mm, "end": v(-58.87, 32.43) * mm});
            skArc(sketch, "E1048", {"start": v(-57.53, 32.83) * mm, "mid": v(-57.42, 33.03) * mm, "end": v(-57.49, 33.25) * mm});
            skArc(sketch, "E1049", {"start": v(-58.87, 32.43) * mm, "mid": v(-58.4, 32.32) * mm, "end": v(-57.95, 32.5) * mm});
            skArc(sketch, "E1050", {"start": v(-63.66, 35.36) * mm, "mid": v(-63.84, 35.4) * mm, "end": v(-64, 35.34) * mm});
            skLineSegment(sketch, "E1051", {"start": v(-26.63, 40.78) * mm, "end": v(-26.57, 40.85) * mm});
            skLineSegment(sketch, "E1052", {"start": v(-26.63, 40.78) * mm, "end": v(-26.82, 40.55) * mm});
            skLineSegment(sketch, "E1053", {"start": v(-29.09, 37.7) * mm, "end": v(-28.46, 37.2) * mm});
            skLineSegment(sketch, "E1054", {"start": v(-28.82, 38.03) * mm, "end": v(-29.09, 37.7) * mm});
            skLineSegment(sketch, "E1055", {"start": v(-28.23, 38.77) * mm, "end": v(-28.23, 38.77) * mm});
            skLineSegment(sketch, "E1056", {"start": v(-27.18, 40.1) * mm, "end": v(-26.82, 40.55) * mm});
            skLineSegment(sketch, "E1057", {"start": v(-25.18, 34.58) * mm, "end": v(-26.12, 35.34) * mm});
            skLineSegment(sketch, "E1058", {"start": v(-22.67, 37.73) * mm, "end": v(-22.28, 38.2) * mm});
            skLineSegment(sketch, "E1059", {"start": v(-24.68, 35.21) * mm, "end": v(-24.92, 34.91) * mm});
            skLineSegment(sketch, "E1060", {"start": v(-24.27, 35.72) * mm, "end": v(-24.32, 35.65) * mm});
            skLineSegment(sketch, "E1061", {"start": v(-24.18, 35.83) * mm, "end": v(-24.18, 35.83) * mm});
            skLineSegment(sketch, "E1062", {"start": v(-24.18, 35.83) * mm, "end": v(-24.15, 35.87) * mm});
            skLineSegment(sketch, "E1063", {"start": v(-23.63, 36.53) * mm, "end": v(-23.57, 36.6) * mm});
            skLineSegment(sketch, "E1064", {"start": v(-23.57, 36.6) * mm, "end": v(-23.56, 36.61) * mm});
            skLineSegment(sketch, "E1065", {"start": v(-24.18, 35.83) * mm, "end": v(-24.27, 35.72) * mm});
            skLineSegment(sketch, "E1066", {"start": v(-23.27, 36.97) * mm, "end": v(-23.31, 36.92) * mm});
            skLineSegment(sketch, "E1067", {"start": v(-23.31, 36.92) * mm, "end": v(-23.56, 36.61) * mm});
            skLineSegment(sketch, "E1068", {"start": v(-23.89, 36.2) * mm, "end": v(-23.69, 36.45) * mm});
            skLineSegment(sketch, "E1069", {"start": v(-24.07, 35.97) * mm, "end": v(-23.98, 36.1) * mm});
            skLineSegment(sketch, "E1070", {"start": v(-23.98, 36.1) * mm, "end": v(-23.9, 36.19) * mm});
            skLineSegment(sketch, "E1071", {"start": v(-23.9, 36.19) * mm, "end": v(-23.89, 36.2) * mm});
            skLineSegment(sketch, "E1072", {"start": v(-24.15, 35.87) * mm, "end": v(-24.07, 35.97) * mm});
            skLineSegment(sketch, "E1073", {"start": v(-23.69, 36.45) * mm, "end": v(-23.63, 36.53) * mm});
            skLineSegment(sketch, "E1074", {"start": v(-24.32, 35.65) * mm, "end": v(-24.5, 35.43) * mm});
            skLineSegment(sketch, "E1075", {"start": v(-24.5, 35.43) * mm, "end": v(-24.54, 35.39) * mm});
            skLineSegment(sketch, "E1076", {"start": v(-24.68, 35.21) * mm, "end": v(-24.68, 35.21) * mm});
            skLineSegment(sketch, "E1077", {"start": v(-24.54, 35.39) * mm, "end": v(-24.6, 35.3) * mm});
            skLineSegment(sketch, "E1078", {"start": v(-24.6, 35.3) * mm, "end": v(-24.6, 35.3) * mm});
            skLineSegment(sketch, "E1079", {"start": v(-24.6, 35.3) * mm, "end": v(-24.68, 35.21) * mm});
            skLineSegment(sketch, "E1080", {"start": v(-24.32, 35.65) * mm, "end": v(-24.32, 35.65) * mm});
            skLineSegment(sketch, "E1081", {"start": v(-22.72, 37.66) * mm, "end": v(-22.9, 37.43) * mm});
            skLineSegment(sketch, "E1082", {"start": v(-23.27, 36.97) * mm, "end": v(-22.9, 37.43) * mm});
            skLineSegment(sketch, "E1083", {"start": v(-22.72, 37.66) * mm, "end": v(-22.67, 37.73) * mm});
            skLineSegment(sketch, "E1084", {"start": v(-24.92, 34.91) * mm, "end": v(-25.18, 34.58) * mm});
            skLineSegment(sketch, "E1085", {"start": v(-27.54, 39.65) * mm, "end": v(-27.48, 39.71) * mm});
            skLineSegment(sketch, "E1086", {"start": v(-27.48, 39.71) * mm, "end": v(-27.47, 39.73) * mm});
            skLineSegment(sketch, "E1087", {"start": v(-27.18, 40.1) * mm, "end": v(-27.22, 40.04) * mm});
            skLineSegment(sketch, "E1088", {"start": v(-27.22, 40.04) * mm, "end": v(-27.47, 39.73) * mm});
            skLineSegment(sketch, "E1089", {"start": v(-27.8, 39.32) * mm, "end": v(-27.6, 39.57) * mm});
            skLineSegment(sketch, "E1090", {"start": v(-27.98, 39.09) * mm, "end": v(-27.88, 39.21) * mm});
            skLineSegment(sketch, "E1091", {"start": v(-27.88, 39.21) * mm, "end": v(-27.8, 39.3) * mm});
            skLineSegment(sketch, "E1092", {"start": v(-27.8, 39.3) * mm, "end": v(-27.8, 39.32) * mm});
            skLineSegment(sketch, "E1093", {"start": v(-28.06, 38.99) * mm, "end": v(-27.98, 39.09) * mm});
            skLineSegment(sketch, "E1094", {"start": v(-27.6, 39.57) * mm, "end": v(-27.54, 39.65) * mm});
            skLineSegment(sketch, "E1095", {"start": v(-28.1, 38.95) * mm, "end": v(-28.09, 38.95) * mm});
            skLineSegment(sketch, "E1096", {"start": v(-28.09, 38.95) * mm, "end": v(-28.06, 38.99) * mm});
            skLineSegment(sketch, "E1097", {"start": v(-28.1, 38.95) * mm, "end": v(-24.18, 35.83) * mm});
            skLineSegment(sketch, "E1098", {"start": v(-28.1, 38.95) * mm, "end": v(-28.18, 38.83) * mm});
            skLineSegment(sketch, "E1099", {"start": v(-28.18, 38.83) * mm, "end": v(-28.23, 38.77) * mm});
            skLineSegment(sketch, "E1100", {"start": v(-28.23, 38.77) * mm, "end": v(-28.4, 38.55) * mm});
            skLineSegment(sketch, "E1101", {"start": v(-24.54, 35.39) * mm, "end": v(-28.45, 38.5) * mm});
            skLineSegment(sketch, "E1102", {"start": v(-28.4, 38.55) * mm, "end": v(-28.45, 38.5) * mm});
            skLineSegment(sketch, "E1103", {"start": v(-28.58, 38.33) * mm, "end": v(-28.58, 38.33) * mm});
            skLineSegment(sketch, "E1104", {"start": v(-28.51, 38.42) * mm, "end": v(-28.51, 38.42) * mm});
            skLineSegment(sketch, "E1105", {"start": v(-28.51, 38.42) * mm, "end": v(-28.58, 38.33) * mm});
            skLineSegment(sketch, "E1106", {"start": v(-28.58, 38.33) * mm, "end": v(-28.82, 38.03) * mm});
            skLineSegment(sketch, "E1107", {"start": v(-28.45, 38.5) * mm, "end": v(-28.51, 38.42) * mm});
            skLineSegment(sketch, "E1108", {"start": v(-26.57, 40.85) * mm, "end": v(-22.67, 37.73) * mm});
            skLineSegment(sketch, "E1109", {"start": v(-26.2, 41.33) * mm, "end": v(-22.28, 38.2) * mm});
            skLineSegment(sketch, "E1110", {"start": v(-26.57, 40.85) * mm, "end": v(-26.2, 41.33) * mm});
            skLineSegment(sketch, "E1111", {"start": v(-26.46, 35.36) * mm, "end": v(-31.26, 32.43) * mm});
            skLineSegment(sketch, "E1112", {"start": v(-32.2, 32.51) * mm, "end": v(-28.46, 37.2) * mm});
            skLineSegment(sketch, "E1113", {"start": v(-32.64, 33.25) * mm, "end": v(-29.09, 37.7) * mm});
            skLineSegment(sketch, "E1114", {"start": v(-32.2, 32.51) * mm, "end": v(-32.6, 32.83) * mm});
            skLineSegment(sketch, "E1115", {"start": v(-32.2, 32.51) * mm, "end": v(-32.17, 32.5) * mm});
            skArc(sketch, "E1116", {"start": v(-26.12, 35.34) * mm, "mid": v(-26.29, 35.4) * mm, "end": v(-26.46, 35.36) * mm});
            skArc(sketch, "E1117", {"start": v(-32.17, 32.5) * mm, "mid": v(-31.72, 32.32) * mm, "end": v(-31.26, 32.43) * mm});
            skArc(sketch, "E1118", {"start": v(-32.64, 33.25) * mm, "mid": v(-32.7, 33.03) * mm, "end": v(-32.6, 32.83) * mm});
            skLineSegment(sketch, "E1119", {"start": v(35.85, 28.22) * mm, "end": v(36.45, 28.22) * mm});
            skLineSegment(sketch, "E1120", {"start": v(36.45, 28.22) * mm, "end": v(36.45, 30.92) * mm});
            skLineSegment(sketch, "E1121", {"start": v(24.45, 31.17) * mm, "end": v(34.35, 31.17) * mm});
            skLineSegment(sketch, "E1122", {"start": v(23.95, 30.75) * mm, "end": v(23.95, 30.92) * mm});
            skLineSegment(sketch, "E1123", {"start": v(22.95, 29.19) * mm, "end": v(22.35, 29.19) * mm});
            skLineSegment(sketch, "E1124", {"start": v(22.95, 29.21) * mm, "end": v(22.35, 29.21) * mm});
            skLineSegment(sketch, "E1125", {"start": v(22.35, 30.92) * mm, "end": v(22.35, 29.21) * mm});
            skLineSegment(sketch, "E1126", {"start": v(22.35, 29.19) * mm, "end": v(22.35, 29.21) * mm});
            skLineSegment(sketch, "E1127", {"start": v(22.35, 35.68) * mm, "end": v(22.35, 30.92) * mm});
            skLineSegment(sketch, "E1128", {"start": v(24.45, 36.73) * mm, "end": v(24.45, 31.97) * mm});
            skLineSegment(sketch, "E1129", {"start": v(28.95, 31.97) * mm, "end": v(24.45, 31.97) * mm});
            skLineSegment(sketch, "E1130", {"start": v(26.35, 36.73) * mm, "end": v(24.45, 36.73) * mm});
            skLineSegment(sketch, "E1131", {"start": v(34.35, 33.05) * mm, "end": v(34.35, 31.97) * mm});
            skLineSegment(sketch, "E1132", {"start": v(34.35, 31.97) * mm, "end": v(32.75, 31.97) * mm});
            skLineSegment(sketch, "E1133", {"start": v(36.45, 35.68) * mm, "end": v(36.45, 30.92) * mm});
            skLineSegment(sketch, "E1134", {"start": v(34.85, 30.75) * mm, "end": v(34.85, 30.92) * mm});
            skFitSpline(sketch, "E1135", {"points": [v(34.85, 30.92) * mm, v(34.85, 30.94) * mm, v(34.84, 31) * mm, v(34.78, 31.05) * mm, v(34.7, 31.1) * mm, v(34.6, 31.14) * mm, v(34.48, 31.17) * mm, v(34.4, 31.17) * mm, v(34.35, 31.17) * mm]});
            skFitSpline(sketch, "E1136", {"points": [v(24.45, 31.17) * mm, v(24.4, 31.17) * mm, v(24.32, 31.17) * mm, v(24.2, 31.14) * mm, v(24.1, 31.1) * mm, v(24.02, 31.05) * mm, v(23.96, 31) * mm, v(23.96, 30.94) * mm, v(23.95, 30.92) * mm]});
            skFitSpline(sketch, "E1137", {"points": [v(24.45, 31.97) * mm, v(24.27, 31.96) * mm, v(23.92, 31.95) * mm, v(23.42, 31.85) * mm, v(22.98, 31.69) * mm, v(22.64, 31.47) * mm, v(22.4, 31.22) * mm, v(22.37, 31.01) * mm, v(22.35, 30.92) * mm]});
            skFitSpline(sketch, "E1138", {"points": [v(24.45, 36.73) * mm, v(24.27, 36.73) * mm, v(23.92, 36.71) * mm, v(23.42, 36.6) * mm, v(22.98, 36.45) * mm, v(22.64, 36.24) * mm, v(22.4, 35.98) * mm, v(22.37, 35.78) * mm, v(22.35, 35.68) * mm]});
            skFitSpline(sketch, "E1139", {"points": [v(36.45, 30.92) * mm, v(36.44, 31.01) * mm, v(36.4, 31.22) * mm, v(36.16, 31.47) * mm, v(35.82, 31.69) * mm, v(35.39, 31.85) * mm, v(34.89, 31.95) * mm, v(34.53, 31.96) * mm, v(34.35, 31.97) * mm]});
            skFitSpline(sketch, "E1140", {"points": [v(36.45, 35.68) * mm, v(36.43, 35.78) * mm, v(36.4, 36) * mm, v(36.14, 36.25) * mm, v(35.8, 36.47) * mm, v(35.5, 36.56) * mm, v(35.35, 36.6) * mm]});
            skLineSegment(sketch, "E1141", {"start": v(23.95, 37.46) * mm, "end": v(23.95, 36.7) * mm});
            skLineSegment(sketch, "E1142", {"start": v(23.95, 37.46) * mm, "end": v(26.4, 37.46) * mm});
            skLineSegment(sketch, "E1143", {"start": v(22.95, 36.96) * mm, "end": v(22.95, 36.42) * mm});
            skLineSegment(sketch, "E1144", {"start": v(35.85, 36.96) * mm, "end": v(35.85, 36.42) * mm});
            skLineSegment(sketch, "E1145", {"start": v(35.85, 28.3) * mm, "end": v(35.85, 26.4) * mm});
            skLineSegment(sketch, "E1146", {"start": v(35.65, 26.3) * mm, "end": v(34.25, 26.3) * mm});
            skLineSegment(sketch, "E1147", {"start": v(33.35, 27.8) * mm, "end": v(34.25, 27.8) * mm});
            skLineSegment(sketch, "E1148", {"start": v(22.95, 27.8) * mm, "end": v(22.95, 28.3) * mm});
            skLineSegment(sketch, "E1149", {"start": v(33.35, 27.6) * mm, "end": v(33.35, 27.8) * mm});
            skLineSegment(sketch, "E1150", {"start": v(28.35, 27.8) * mm, "end": v(28.35, 27.6) * mm});
            skLineSegment(sketch, "E1151", {"start": v(27.45, 27.8) * mm, "end": v(28.35, 27.8) * mm});
            skLineSegment(sketch, "E1152", {"start": v(25.35, 27.7) * mm, "end": v(23.15, 27.7) * mm});
            skLineSegment(sketch, "E1153", {"start": v(34.25, 27.8) * mm, "end": v(34.25, 26.3) * mm});
            skLineSegment(sketch, "E1154", {"start": v(27.45, 26.3) * mm, "end": v(27.45, 27.8) * mm});
            skLineSegment(sketch, "E1155", {"start": v(27.45, 26.3) * mm, "end": v(26.05, 26.3) * mm});
            skLineSegment(sketch, "E1156", {"start": v(25.85, 26.4) * mm, "end": v(25.85, 27.45) * mm});
            skLineSegment(sketch, "E1157", {"start": v(28.35, 27.6) * mm, "end": v(33.35, 27.6) * mm});
            skLineSegment(sketch, "E1158", {"start": v(22.95, 30.25) * mm, "end": v(22.95, 28.3) * mm});
            skLineSegment(sketch, "E1159", {"start": v(23.95, 28.8) * mm, "end": v(34.85, 28.8) * mm});
            skLineSegment(sketch, "E1160", {"start": v(24.95, 31.17) * mm, "end": v(24.95, 30.75) * mm});
            skLineSegment(sketch, "E1161", {"start": v(23.95, 30.75) * mm, "end": v(24.95, 30.75) * mm});
            skLineSegment(sketch, "E1162", {"start": v(23.95, 30.75) * mm, "end": v(23.95, 28.8) * mm});
            skLineSegment(sketch, "E1163", {"start": v(35.85, 30.25) * mm, "end": v(35.85, 28.3) * mm});
            skLineSegment(sketch, "E1164", {"start": v(33.85, 30.75) * mm, "end": v(34.85, 30.75) * mm});
            skLineSegment(sketch, "E1165", {"start": v(33.85, 31.17) * mm, "end": v(33.85, 30.75) * mm});
            skLineSegment(sketch, "E1166", {"start": v(34.85, 30.75) * mm, "end": v(34.85, 28.8) * mm});
            skFitSpline(sketch, "E1167", {"points": [v(23.95, 37.46) * mm, v(23.87, 37.46) * mm, v(23.7, 37.45) * mm, v(23.46, 37.4) * mm, v(23.25, 37.33) * mm, v(23.1, 37.23) * mm, v(22.98, 37.1) * mm, v(22.96, 37) * mm, v(22.95, 36.96) * mm]});
            skFitSpline(sketch, "E1168", {"points": [v(35.85, 36.96) * mm, v(35.84, 37.01) * mm, v(35.82, 37.11) * mm, v(35.7, 37.24) * mm, v(35.52, 37.34) * mm, v(35.38, 37.39) * mm, v(35.3, 37.4) * mm]});
            skFitSpline(sketch, "E1169", {"points": [v(35.65, 26.3) * mm, v(35.68, 26.3) * mm, v(35.73, 26.3) * mm, v(35.79, 26.33) * mm, v(35.84, 26.36) * mm, v(35.85, 26.4) * mm, v(35.85, 26.4) * mm]});
            skFitSpline(sketch, "E1170", {"points": [v(22.95, 27.8) * mm, v(22.96, 27.8) * mm, v(22.96, 27.76) * mm, v(23.01, 27.73) * mm, v(23.08, 27.7) * mm, v(23.13, 27.7) * mm, v(23.15, 27.7) * mm]});
            skFitSpline(sketch, "E1171", {"points": [v(25.85, 26.4) * mm, v(25.86, 26.4) * mm, v(25.86, 26.36) * mm, v(25.91, 26.33) * mm, v(25.98, 26.3) * mm, v(26.03, 26.3) * mm, v(26.05, 26.3) * mm]});
            skFitSpline(sketch, "E1172", {"points": [v(25.85, 27.45) * mm, v(25.85, 27.48) * mm, v(25.84, 27.52) * mm, v(25.78, 27.59) * mm, v(25.7, 27.64) * mm, v(25.6, 27.67) * mm, v(25.48, 27.7) * mm, v(25.4, 27.7) * mm, v(25.35, 27.7) * mm]});
            skFitSpline(sketch, "E1173", {"points": [v(23.95, 28.8) * mm, v(23.87, 28.8) * mm, v(23.7, 28.8) * mm, v(23.46, 28.74) * mm, v(23.25, 28.67) * mm, v(23.1, 28.57) * mm, v(22.98, 28.45) * mm, v(22.96, 28.35) * mm, v(22.95, 28.3) * mm]});
            skFitSpline(sketch, "E1174", {"points": [v(23.95, 30.75) * mm, v(23.87, 30.75) * mm, v(23.7, 30.74) * mm, v(23.46, 30.7) * mm, v(23.25, 30.62) * mm, v(23.1, 30.52) * mm, v(22.98, 30.4) * mm, v(22.96, 30.3) * mm, v(22.95, 30.25) * mm]});
            skFitSpline(sketch, "E1175", {"points": [v(35.85, 28.3) * mm, v(35.84, 28.35) * mm, v(35.83, 28.45) * mm, v(35.71, 28.57) * mm, v(35.55, 28.67) * mm, v(35.35, 28.74) * mm, v(35.1, 28.8) * mm, v(34.94, 28.8) * mm, v(34.85, 28.8) * mm]});
            skFitSpline(sketch, "E1176", {"points": [v(35.85, 30.25) * mm, v(35.84, 30.3) * mm, v(35.83, 30.4) * mm, v(35.71, 30.52) * mm, v(35.55, 30.62) * mm, v(35.35, 30.7) * mm, v(35.1, 30.74) * mm, v(34.94, 30.75) * mm, v(34.85, 30.75) * mm]});
            skLineSegment(sketch, "E1177", {"start": v(35.35, 35.5) * mm, "end": v(35.35, 36.85) * mm});
            skLineSegment(sketch, "E1178", {"start": v(26.35, 35.5) * mm, "end": v(26.35, 36.85) * mm});
            skFitSpline(sketch, "E1179", {"points": [v(35.35, 36.85) * mm, v(35.33, 36.56) * mm, v(35.29, 35.97) * mm, v(34.93, 35.14) * mm, v(34.4, 34.4) * mm, v(33.67, 33.77) * mm, v(32.81, 33.3) * mm, v(31.86, 33.02) * mm, v(30.85, 32.92) * mm, v(29.85, 33.02) * mm, v(28.9, 33.3) * mm, v(28.03, 33.77) * mm, v(27.31, 34.4) * mm, v(26.77, 35.14) * mm, v(26.42, 35.97) * mm, v(26.37, 36.56) * mm, v(26.35, 36.85) * mm]});
            skFitSpline(sketch, "E1180", {"points": [v(35.35, 35.5) * mm, v(35.33, 35.2) * mm, v(35.29, 34.62) * mm, v(34.93, 33.79) * mm, v(34.4, 33.04) * mm, v(33.67, 32.42) * mm, v(32.81, 31.96) * mm, v(31.86, 31.67) * mm, v(30.85, 31.57) * mm, v(29.85, 31.67) * mm, v(28.9, 31.96) * mm, v(28.03, 32.42) * mm, v(27.31, 33.04) * mm, v(26.77, 33.79) * mm, v(26.42, 34.62) * mm, v(26.37, 35.2) * mm, v(26.35, 35.5) * mm]});
            skFitSpline(sketch, "E1181", {"points": [v(26.35, 36.85) * mm, v(26.37, 37.14) * mm, v(26.42, 37.73) * mm, v(26.77, 38.57) * mm, v(27.31, 39.31) * mm, v(28.03, 39.93) * mm, v(28.9, 40.4) * mm, v(29.85, 40.68) * mm, v(30.85, 40.78) * mm, v(31.86, 40.68) * mm, v(32.81, 40.4) * mm, v(33.67, 39.93) * mm, v(34.4, 39.31) * mm, v(34.93, 38.57) * mm, v(35.29, 37.73) * mm, v(35.33, 37.14) * mm, v(35.35, 36.85) * mm]});
            skLineSegment(sketch, "E1182", {"start": v(-16.26, 39.4) * mm, "end": v(-11.76, 31.6) * mm});
            skLineSegment(sketch, "E1183", {"start": v(-9.42, 32.95) * mm, "end": v(-13.92, 40.75) * mm});
            skLineSegment(sketch, "E1184", {"start": v(-12.17, 31.71) * mm, "end": v(-11.76, 31.6) * mm});
            skLineSegment(sketch, "E1185", {"start": v(-9.31, 33.36) * mm, "end": v(-9.42, 32.95) * mm});
            skLineSegment(sketch, "E1186", {"start": v(-13.51, 40.64) * mm, "end": v(-13.92, 40.75) * mm});
            skLineSegment(sketch, "E1187", {"start": v(-16.26, 39.4) * mm, "end": v(-16.37, 38.99) * mm});
            skLineSegment(sketch, "E1188", {"start": v(-13.51, 40.64) * mm, "end": v(-9.31, 33.36) * mm});
            skLineSegment(sketch, "E1189", {"start": v(-16.26, 39.4) * mm, "end": v(-13.92, 40.75) * mm});
            skLineSegment(sketch, "E1190", {"start": v(-12.17, 31.71) * mm, "end": v(-16.37, 38.99) * mm});
            skLineSegment(sketch, "E1191", {"start": v(-9.42, 32.95) * mm, "end": v(-11.76, 31.6) * mm});
            skLineSegment(sketch, "E1192", {"start": v(-14.5, 32.74) * mm, "end": v(-13.54, 33.29) * mm});
            skLineSegment(sketch, "E1193", {"start": v(-16.83, 35.78) * mm, "end": v(-15.18, 32.92) * mm});
            skLineSegment(sketch, "E1194", {"start": v(-15.7, 37.01) * mm, "end": v(-16.64, 36.46) * mm});
            skArc(sketch, "E1195", {"start": v(-15.7, 37.01) * mm, "mid": v(-15.5, 37.26) * mm, "end": v(-15.54, 37.56) * mm});
            skArc(sketch, "E1196", {"start": v(-13, 33.14) * mm, "mid": v(-13.24, 33.33) * mm, "end": v(-13.54, 33.29) * mm});
            skArc(sketch, "E1197", {"start": v(-15.18, 32.92) * mm, "mid": v(-14.87, 32.69) * mm, "end": v(-14.5, 32.74) * mm});
            skArc(sketch, "E1198", {"start": v(-16.64, 36.46) * mm, "mid": v(-16.88, 36.16) * mm, "end": v(-16.83, 35.78) * mm});
            skLineSegment(sketch, "E1199", {"start": v(-19.2, 35.68) * mm, "end": v(-16.45, 30.92) * mm});
            skLineSegment(sketch, "E1200", {"start": v(-17.14, 30.52) * mm, "end": v(-17.66, 30.22) * mm});
            skLineSegment(sketch, "E1201", {"start": v(-19.2, 35.68) * mm, "end": v(-18.76, 35.93) * mm});
            skLineSegment(sketch, "E1202", {"start": v(-21.92, 34.1) * mm, "end": v(-20.4, 34.98) * mm});
            skLineSegment(sketch, "E1203", {"start": v(-22.03, 34.05) * mm, "end": v(-21.92, 34.1) * mm});
            skLineSegment(sketch, "E1204", {"start": v(-19.89, 35.28) * mm, "end": v(-19.54, 35.48) * mm});
            skLineSegment(sketch, "E1205", {"start": v(-19.17, 29.35) * mm, "end": v(-19.3, 29.27) * mm});
            skLineSegment(sketch, "E1206", {"start": v(-17.66, 30.22) * mm, "end": v(-19.17, 29.35) * mm});
            skLineSegment(sketch, "E1207", {"start": v(-20.4, 34.98) * mm, "end": v(-19.89, 35.28) * mm});
            skLineSegment(sketch, "E1208", {"start": v(-19.54, 35.48) * mm, "end": v(-19.2, 35.68) * mm});
            skLineSegment(sketch, "E1209", {"start": v(-18.76, 35.93) * mm, "end": v(-17.38, 36.73) * mm});
            skLineSegment(sketch, "E1210", {"start": v(-16.88, 35.87) * mm, "end": v(-16.7, 35.56) * mm});
            skLineSegment(sketch, "E1211", {"start": v(-17.14, 30.52) * mm, "end": v(-16.8, 30.72) * mm});
            skLineSegment(sketch, "E1212", {"start": v(-17.38, 36.73) * mm, "end": v(-16.88, 35.87) * mm});
            skLineSegment(sketch, "E1213", {"start": v(-16.7, 35.56) * mm, "end": v(-16.63, 35.43) * mm});
            skLineSegment(sketch, "E1214", {"start": v(-16.8, 30.72) * mm, "end": v(-16.45, 30.92) * mm});
            skLineSegment(sketch, "E1215", {"start": v(-16.01, 31.17) * mm, "end": v(-14.63, 31.97) * mm});
            skLineSegment(sketch, "E1216", {"start": v(-15.13, 32.84) * mm, "end": v(-14.63, 31.97) * mm});
            skLineSegment(sketch, "E1217", {"start": v(-15.3, 33.14) * mm, "end": v(-15.13, 32.84) * mm});
            skLineSegment(sketch, "E1218", {"start": v(-16.45, 30.92) * mm, "end": v(-16.01, 31.17) * mm});
            skLineSegment(sketch, "E1219", {"start": v(-15.38, 33.27) * mm, "end": v(-15.3, 33.14) * mm});
            skLineSegment(sketch, "E1220", {"start": v(-16.63, 35.43) * mm, "end": v(-15.38, 33.27) * mm});
            skLineSegment(sketch, "E1221", {"start": v(-20.67, 37.43) * mm, "end": v(-19.54, 35.48) * mm});
            skLineSegment(sketch, "E1222", {"start": v(-20.78, 37.36) * mm, "end": v(-23.2, 35.97) * mm});
            skLineSegment(sketch, "E1223", {"start": v(-21.28, 36.5) * mm, "end": v(-22.8, 35.62) * mm});
            skLineSegment(sketch, "E1224", {"start": v(-21.28, 36.5) * mm, "end": v(-20.5, 35.16) * mm});
            skLineSegment(sketch, "E1225", {"start": v(-23.3, 35.7) * mm, "end": v(-23.3, 35.7) * mm});
            skLineSegment(sketch, "E1226", {"start": v(-23.07, 35.7) * mm, "end": v(-23.14, 35.82) * mm});
            skLineSegment(sketch, "E1227", {"start": v(-22.8, 35.62) * mm, "end": v(-22.47, 35.05) * mm});
            skLineSegment(sketch, "E1228", {"start": v(-23.1, 35.45) * mm, "end": v(-22.97, 35.52) * mm});
            skLineSegment(sketch, "E1229", {"start": v(-22.97, 35.52) * mm, "end": v(-22.7, 35.04) * mm});
            skLineSegment(sketch, "E1230", {"start": v(-23.07, 35.7) * mm, "end": v(-22.97, 35.52) * mm});
            skLineSegment(sketch, "E1231", {"start": v(-20.5, 35.16) * mm, "end": v(-22.02, 34.28) * mm});
            skLineSegment(sketch, "E1232", {"start": v(-22.08, 34.38) * mm, "end": v(-22.02, 34.28) * mm});
            skLineSegment(sketch, "E1233", {"start": v(-22.02, 34.28) * mm, "end": v(-22.07, 34.1) * mm});
            skLineSegment(sketch, "E1234", {"start": v(-19.07, 29.17) * mm, "end": v(-18.96, 28.98) * mm});
            skLineSegment(sketch, "E1235", {"start": v(-19.07, 29.17) * mm, "end": v(-19.28, 29.23) * mm});
            skLineSegment(sketch, "E1236", {"start": v(-18.6, 27.66) * mm, "end": v(-18.47, 27.73) * mm});
            skLineSegment(sketch, "E1237", {"start": v(-18.62, 27.64) * mm, "end": v(-18.6, 27.66) * mm});
            skLineSegment(sketch, "E1238", {"start": v(-18.47, 27.73) * mm, "end": v(-18.37, 27.56) * mm});
            skLineSegment(sketch, "E1239", {"start": v(-18.37, 27.56) * mm, "end": v(-18.27, 27.38) * mm});
            skLineSegment(sketch, "E1240", {"start": v(-18.7, 28.13) * mm, "end": v(-18.47, 27.73) * mm});
            skLineSegment(sketch, "E1241", {"start": v(-18.52, 27.38) * mm, "end": v(-18.3, 27.32) * mm});
            skLineSegment(sketch, "E1242", {"start": v(-18.23, 27.29) * mm, "end": v(-18.22, 27.3) * mm});
            skLineSegment(sketch, "E1243", {"start": v(-18.24, 27.3) * mm, "end": v(-18.22, 27.3) * mm});
            skLineSegment(sketch, "E1244", {"start": v(-18.22, 27.3) * mm, "end": v(-18.27, 27.38) * mm});
            skLineSegment(sketch, "E1245", {"start": v(-18.73, 28.57) * mm, "end": v(-18.3, 27.83) * mm});
            skLineSegment(sketch, "E1246", {"start": v(-19.07, 29.17) * mm, "end": v(-17.56, 30.05) * mm});
            skLineSegment(sketch, "E1247", {"start": v(-20.67, 37.43) * mm, "end": v(-20.78, 37.36) * mm});
            skLineSegment(sketch, "E1248", {"start": v(-18.3, 27.83) * mm, "end": v(-16.78, 28.7) * mm});
            skLineSegment(sketch, "E1249", {"start": v(-17.56, 30.05) * mm, "end": v(-16.78, 28.7) * mm});
            skLineSegment(sketch, "E1250", {"start": v(-16.8, 30.72) * mm, "end": v(-15.67, 28.77) * mm});
            skLineSegment(sketch, "E1251", {"start": v(-15.67, 28.77) * mm, "end": v(-15.78, 28.7) * mm});
            skLineSegment(sketch, "E1252", {"start": v(-18.22, 27.3) * mm, "end": v(-15.78, 28.7) * mm});
            skArc(sketch, "E1253", {"start": v(-17.14, 30.52) * mm, "mid": v(-17.17, 30.5) * mm, "end": v(-17.2, 30.48) * mm});
            skArc(sketch, "E1254", {"start": v(-17.2, 30.48) * mm, "mid": v(-17.23, 30.45) * mm, "end": v(-17.26, 30.42) * mm});
            skArc(sketch, "E1255", {"start": v(-17.26, 30.42) * mm, "mid": v(-17.3, 30.39) * mm, "end": v(-17.32, 30.35) * mm});
            skLineSegment(sketch, "E1256", {"start": v(-17.32, 30.35) * mm, "end": v(-17.36, 30.31) * mm});
            skArc(sketch, "E1257", {"start": v(-17.36, 30.31) * mm, "mid": v(-17.4, 30.25) * mm, "end": v(-17.46, 30.19) * mm});
            skArc(sketch, "E1258", {"start": v(-17.46, 30.19) * mm, "mid": v(-17.5, 30.12) * mm, "end": v(-17.56, 30.05) * mm});
            skArc(sketch, "E1259", {"start": v(-20.78, 37.36) * mm, "mid": v(-20.8, 37.36) * mm, "end": v(-20.8, 37.35) * mm});
            skLineSegment(sketch, "E1260", {"start": v(-20.8, 37.35) * mm, "end": v(-20.83, 37.33) * mm});
            skArc(sketch, "E1261", {"start": v(-20.83, 37.33) * mm, "mid": v(-20.86, 37.3) * mm, "end": v(-20.89, 37.26) * mm});
            skArc(sketch, "E1262", {"start": v(-20.89, 37.26) * mm, "mid": v(-20.92, 37.21) * mm, "end": v(-20.95, 37.16) * mm});
            skLineSegment(sketch, "E1263", {"start": v(-20.95, 37.16) * mm, "end": v(-20.98, 37.12) * mm});
            skArc(sketch, "E1264", {"start": v(-20.98, 37.12) * mm, "mid": v(-21, 37.07) * mm, "end": v(-21.04, 37.01) * mm});
            skLineSegment(sketch, "E1265", {"start": v(-21.04, 37.01) * mm, "end": v(-21.08, 36.92) * mm});
            skArc(sketch, "E1266", {"start": v(-21.08, 36.92) * mm, "mid": v(-21.13, 36.83) * mm, "end": v(-21.18, 36.73) * mm});
            skArc(sketch, "E1267", {"start": v(-21.18, 36.73) * mm, "mid": v(-21.23, 36.62) * mm, "end": v(-21.27, 36.52) * mm});
            skLineSegment(sketch, "E1268", {"start": v(-21.27, 36.52) * mm, "end": v(-21.28, 36.5) * mm});
            skLineSegment(sketch, "E1269", {"start": v(-21.28, 36.5) * mm, "end": v(-21.28, 36.5) * mm});
            skArc(sketch, "E1270", {"start": v(-22.8, 35.62) * mm, "mid": v(-22.84, 35.65) * mm, "end": v(-22.9, 35.67) * mm});
            skArc(sketch, "E1271", {"start": v(-22.9, 35.67) * mm, "mid": v(-22.93, 35.7) * mm, "end": v(-22.98, 35.72) * mm});
            skLineSegment(sketch, "E1272", {"start": v(-22.98, 35.72) * mm, "end": v(-23.02, 35.74) * mm});
            skArc(sketch, "E1273", {"start": v(-23.02, 35.74) * mm, "mid": v(-23.04, 35.76) * mm, "end": v(-23.07, 35.78) * mm});
            skArc(sketch, "E1274", {"start": v(-23.07, 35.78) * mm, "mid": v(-23.1, 35.8) * mm, "end": v(-23.12, 35.81) * mm});
            skLineSegment(sketch, "E1275", {"start": v(-23.12, 35.81) * mm, "end": v(-23.14, 35.83) * mm});
            skArc(sketch, "E1276", {"start": v(-23.1, 35.46) * mm, "mid": v(-23.11, 35.47) * mm, "end": v(-23.12, 35.49) * mm});
            skArc(sketch, "E1277", {"start": v(-23.12, 35.49) * mm, "mid": v(-23.13, 35.5) * mm, "end": v(-23.13, 35.5) * mm});
            skArc(sketch, "E1278", {"start": v(-23.13, 35.5) * mm, "mid": v(-23.14, 35.52) * mm, "end": v(-23.15, 35.52) * mm});
            skArc(sketch, "E1279", {"start": v(-23.15, 35.52) * mm, "mid": v(-23.15, 35.53) * mm, "end": v(-23.16, 35.54) * mm});
            skArc(sketch, "E1280", {"start": v(-23.16, 35.54) * mm, "mid": v(-23.16, 35.54) * mm, "end": v(-23.17, 35.55) * mm});
            skArc(sketch, "E1281", {"start": v(-23.17, 35.55) * mm, "mid": v(-23.17, 35.56) * mm, "end": v(-23.18, 35.56) * mm});
            skArc(sketch, "E1282", {"start": v(-23.18, 35.56) * mm, "mid": v(-23.18, 35.56) * mm, "end": v(-23.19, 35.57) * mm});
            skArc(sketch, "E1283", {"start": v(-23.19, 35.57) * mm, "mid": v(-23.2, 35.57) * mm, "end": v(-23.2, 35.57) * mm});
            skArc(sketch, "E1284", {"start": v(-18.27, 27.38) * mm, "mid": v(-18.28, 27.4) * mm, "end": v(-18.28, 27.41) * mm});
            skLineSegment(sketch, "E1285", {"start": v(-18.28, 27.41) * mm, "end": v(-18.29, 27.43) * mm});
            skArc(sketch, "E1286", {"start": v(-18.29, 27.43) * mm, "mid": v(-18.3, 27.46) * mm, "end": v(-18.3, 27.48) * mm});
            skArc(sketch, "E1287", {"start": v(-18.3, 27.48) * mm, "mid": v(-18.3, 27.51) * mm, "end": v(-18.3, 27.55) * mm});
            skLineSegment(sketch, "E1288", {"start": v(-18.3, 27.55) * mm, "end": v(-18.3, 27.58) * mm});
            skArc(sketch, "E1289", {"start": v(-18.3, 27.58) * mm, "mid": v(-18.3, 27.63) * mm, "end": v(-18.3, 27.68) * mm});
            skArc(sketch, "E1290", {"start": v(-18.3, 27.68) * mm, "mid": v(-18.3, 27.73) * mm, "end": v(-18.3, 27.78) * mm});
            skLineSegment(sketch, "E1291", {"start": v(-18.3, 27.78) * mm, "end": v(-18.3, 27.83) * mm});
            skArc(sketch, "E1292", {"start": v(-18.52, 27.38) * mm, "mid": v(-18.53, 27.39) * mm, "end": v(-18.53, 27.4) * mm});
            skArc(sketch, "E1293", {"start": v(-18.53, 27.4) * mm, "mid": v(-18.54, 27.41) * mm, "end": v(-18.54, 27.43) * mm});
            skArc(sketch, "E1294", {"start": v(-18.54, 27.43) * mm, "mid": v(-18.54, 27.44) * mm, "end": v(-18.54, 27.45) * mm});
            skArc(sketch, "E1295", {"start": v(-18.54, 27.45) * mm, "mid": v(-18.55, 27.47) * mm, "end": v(-18.55, 27.48) * mm});
            skArc(sketch, "E1296", {"start": v(-18.55, 27.48) * mm, "mid": v(-18.55, 27.5) * mm, "end": v(-18.55, 27.51) * mm});
            skArc(sketch, "E1297", {"start": v(-18.55, 27.51) * mm, "mid": v(-18.56, 27.53) * mm, "end": v(-18.56, 27.55) * mm});
            skArc(sketch, "E1298", {"start": v(-18.56, 27.55) * mm, "mid": v(-18.56, 27.57) * mm, "end": v(-18.57, 27.58) * mm});
            skArc(sketch, "E1299", {"start": v(-18.57, 27.58) * mm, "mid": v(-18.57, 27.6) * mm, "end": v(-18.58, 27.62) * mm});
            skArc(sketch, "E1300", {"start": v(-18.58, 27.62) * mm, "mid": v(-18.59, 27.64) * mm, "end": v(-18.6, 27.66) * mm});
            skArc(sketch, "E1301", {"start": v(-19.89, 35.28) * mm, "mid": v(-19.93, 35.26) * mm, "end": v(-19.97, 35.25) * mm});
            skArc(sketch, "E1302", {"start": v(-19.97, 35.25) * mm, "mid": v(-20.02, 35.23) * mm, "end": v(-20.06, 35.22) * mm});
            skArc(sketch, "E1303", {"start": v(-20.06, 35.22) * mm, "mid": v(-20.12, 35.2) * mm, "end": v(-20.18, 35.2) * mm});
            skLineSegment(sketch, "E1304", {"start": v(-20.18, 35.2) * mm, "end": v(-20.25, 35.19) * mm});
            skArc(sketch, "E1305", {"start": v(-20.25, 35.19) * mm, "mid": v(-20.34, 35.17) * mm, "end": v(-20.42, 35.17) * mm});
            skLineSegment(sketch, "E1306", {"start": v(-20.42, 35.17) * mm, "end": v(-20.5, 35.16) * mm});
            skArc(sketch, "E1307", {"start": v(-15.78, 28.7) * mm, "mid": v(-15.8, 28.7) * mm, "end": v(-15.8, 28.7) * mm});
            skLineSegment(sketch, "E1308", {"start": v(-15.8, 28.7) * mm, "end": v(-15.84, 28.68) * mm});
            skArc(sketch, "E1309", {"start": v(-15.84, 28.68) * mm, "mid": v(-15.88, 28.67) * mm, "end": v(-15.93, 28.67) * mm});
            skArc(sketch, "E1310", {"start": v(-15.93, 28.67) * mm, "mid": v(-15.98, 28.66) * mm, "end": v(-16.04, 28.66) * mm});
            skLineSegment(sketch, "E1311", {"start": v(-16.04, 28.66) * mm, "end": v(-16.1, 28.66) * mm});
            skArc(sketch, "E1312", {"start": v(-16.1, 28.66) * mm, "mid": v(-16.15, 28.66) * mm, "end": v(-16.21, 28.66) * mm});
            skLineSegment(sketch, "E1313", {"start": v(-16.21, 28.66) * mm, "end": v(-16.31, 28.67) * mm});
            skArc(sketch, "E1314", {"start": v(-16.31, 28.67) * mm, "mid": v(-16.42, 28.67) * mm, "end": v(-16.53, 28.68) * mm});
            skArc(sketch, "E1315", {"start": v(-16.53, 28.68) * mm, "mid": v(-16.65, 28.7) * mm, "end": v(-16.76, 28.7) * mm});
            skLineSegment(sketch, "E1316", {"start": v(-16.76, 28.7) * mm, "end": v(-16.77, 28.7) * mm});
            skLineSegment(sketch, "E1317", {"start": v(-16.77, 28.7) * mm, "end": v(-16.78, 28.7) * mm});
            skArc(sketch, "E1318", {"start": v(-29.68, 36.95) * mm, "mid": v(-45.06, 42.34) * mm, "end": v(-60.44, 36.95) * mm});
            skArc(sketch, "E1319", {"start": v(-20.41, 17.69) * mm, "mid": v(-22.21, 26.93) * mm, "end": v(-27.34, 34.82) * mm});
            skArc(sketch, "E1320", {"start": v(-69.71, 17.69) * mm, "mid": v(-45.06, -6.96) * mm, "end": v(-20.41, 17.69) * mm});
            skArc(sketch, "E1321", {"start": v(-62.79, 34.82) * mm, "mid": v(-67.92, 26.93) * mm, "end": v(-69.71, 17.69) * mm});
            skCircle(sketch, "E1322", {"center": v(-45.06, 17.69) * mm, "radius": 16.7 * mm});
            skLineSegment(sketch, "E1323", {"start": v(-47.56, -43.21) * mm, "end": v(-47.56, -40.41) * mm});
            skLineSegment(sketch, "E1324", {"start": v(-47.36, -40.21) * mm, "end": v(-42.76, -40.21) * mm});
            skLineSegment(sketch, "E1325", {"start": v(-42.56, -40.41) * mm, "end": v(-42.56, -43.21) * mm});
            skLineSegment(sketch, "E1326", {"start": v(-42.56, -43.21) * mm, "end": v(-43.31, -43.21) * mm});
            skLineSegment(sketch, "E1327", {"start": v(-47.56, -43.21) * mm, "end": v(-46.86, -46.81) * mm});
            skLineSegment(sketch, "E1328", {"start": v(-47.36, -40.21) * mm, "end": v(-47.56, -40.41) * mm});
            skLineSegment(sketch, "E1329", {"start": v(-42.56, -40.41) * mm, "end": v(-42.76, -40.21) * mm});
            skLineSegment(sketch, "E1330", {"start": v(-47.56, -40.41) * mm, "end": v(-44.67, -40.41) * mm});
            skLineSegment(sketch, "E1331", {"start": v(-43.26, -46.81) * mm, "end": v(-42.56, -43.21) * mm});
            skLineSegment(sketch, "E1332", {"start": v(-46.86, -46.81) * mm, "end": v(-43.26, -46.81) * mm});
            skLineSegment(sketch, "E1333", {"start": v(-44.67, -40.41) * mm, "end": v(-42.56, -40.41) * mm});
            skLineSegment(sketch, "E1334", {"start": v(-43.31, -43.21) * mm, "end": v(-47.56, -43.21) * mm});
            skLineSegment(sketch, "E1335", {"start": v(33.35, -40.41) * mm, "end": v(33.35, -43.21) * mm});
            skLineSegment(sketch, "E1336", {"start": v(28.55, -40.21) * mm, "end": v(33.15, -40.21) * mm});
            skLineSegment(sketch, "E1337", {"start": v(28.35, -43.21) * mm, "end": v(28.35, -40.41) * mm});
            skLineSegment(sketch, "E1338", {"start": v(29.1, -43.21) * mm, "end": v(28.35, -43.21) * mm});
            skLineSegment(sketch, "E1339", {"start": v(32.65, -46.81) * mm, "end": v(33.35, -43.21) * mm});
            skLineSegment(sketch, "E1340", {"start": v(33.35, -40.41) * mm, "end": v(33.15, -40.21) * mm});
            skLineSegment(sketch, "E1341", {"start": v(28.55, -40.21) * mm, "end": v(28.35, -40.41) * mm});
            skLineSegment(sketch, "E1342", {"start": v(30.46, -40.41) * mm, "end": v(33.35, -40.41) * mm});
            skLineSegment(sketch, "E1343", {"start": v(28.35, -43.21) * mm, "end": v(29.05, -46.81) * mm});
            skLineSegment(sketch, "E1344", {"start": v(29.05, -46.81) * mm, "end": v(32.65, -46.81) * mm});
            skLineSegment(sketch, "E1345", {"start": v(28.35, -40.41) * mm, "end": v(30.46, -40.41) * mm});
            skLineSegment(sketch, "E1346", {"start": v(33.35, -43.21) * mm, "end": v(29.1, -43.21) * mm});
            skArc(sketch, "E1347", {"start": v(-46.33, -46.81) * mm, "mid": v(-45.79, -47.33) * mm, "end": v(-45.06, -47.51) * mm});
            skArc(sketch, "E1348", {"start": v(-45.06, -47.51) * mm, "mid": v(-44.34, -47.33) * mm, "end": v(-43.8, -46.81) * mm});
            skArc(sketch, "E1349", {"start": v(30.85, -47.51) * mm, "mid": v(31.58, -47.33) * mm, "end": v(32.12, -46.81) * mm});
            skArc(sketch, "E1350", {"start": v(29.58, -46.81) * mm, "mid": v(30.13, -47.33) * mm, "end": v(30.85, -47.51) * mm});
            skLineSegment(sketch, "E1351", {"start": v(-47.46, -27.71) * mm, "end": v(-47.46, -40.01) * mm});
            skLineSegment(sketch, "E1352", {"start": v(-42.66, -27.71) * mm, "end": v(-42.66, -40.01) * mm});
            skLineSegment(sketch, "E1353", {"start": v(28.45, -40.01) * mm, "end": v(28.45, -36.72) * mm});
            skLineSegment(sketch, "E1354", {"start": v(33.25, -35.71) * mm, "end": v(33.25, -27.71) * mm});
            skLineSegment(sketch, "E1355", {"start": v(-47.26, -40.21) * mm, "end": v(-43.56, -40.21) * mm});
            skLineSegment(sketch, "E1356", {"start": v(-43.56, -40.21) * mm, "end": v(-42.86, -40.21) * mm});
            skLineSegment(sketch, "E1357", {"start": v(-47.26, -40.21) * mm, "end": v(-47.46, -40.01) * mm});
            skLineSegment(sketch, "E1358", {"start": v(-42.86, -40.21) * mm, "end": v(-42.66, -40.01) * mm});
            skLineSegment(sketch, "E1359", {"start": v(33.25, -40.01) * mm, "end": v(33.25, -35.98) * mm});
            skLineSegment(sketch, "E1360", {"start": v(32.35, -40.21) * mm, "end": v(33.05, -40.21) * mm});
            skLineSegment(sketch, "E1361", {"start": v(29.35, -40.21) * mm, "end": v(29.6, -40.21) * mm});
            skLineSegment(sketch, "E1362", {"start": v(28.65, -40.21) * mm, "end": v(29.35, -40.21) * mm});
            skLineSegment(sketch, "E1363", {"start": v(33.25, -40.01) * mm, "end": v(33.05, -40.21) * mm});
            skLineSegment(sketch, "E1364", {"start": v(28.45, -40.01) * mm, "end": v(28.65, -40.21) * mm});
            skLineSegment(sketch, "E1365", {"start": v(-47.46, -40.01) * mm, "end": v(-42.66, -40.01) * mm});
            skLineSegment(sketch, "E1366", {"start": v(33.25, -35.98) * mm, "end": v(33.25, -35.71) * mm});
            skLineSegment(sketch, "E1367", {"start": v(28.45, -36.72) * mm, "end": v(28.45, -27.71) * mm});
            skLineSegment(sketch, "E1368", {"start": v(32.1, -40.21) * mm, "end": v(32.35, -40.21) * mm});
            skLineSegment(sketch, "E1369", {"start": v(29.6, -40.21) * mm, "end": v(32.1, -40.21) * mm});
            skLineSegment(sketch, "E1370", {"start": v(34.85, 45.49) * mm, "end": v(34.85, 43.55) * mm});
            skLineSegment(sketch, "E1371", {"start": v(27.55, 45.49) * mm, "end": v(34.85, 45.49) * mm});
            skLineSegment(sketch, "E1372", {"start": v(26.85, 45.49) * mm, "end": v(27.55, 45.49) * mm});
            skLineSegment(sketch, "E1373", {"start": v(26.85, 43.55) * mm, "end": v(26.85, 45.49) * mm});
            skLineSegment(sketch, "E1374", {"start": v(-41.06, -10.53) * mm, "end": v(-41.06, -27.51) * mm});
            skLineSegment(sketch, "E1375", {"start": v(-49.06, -27.51) * mm, "end": v(-49.06, -10.28) * mm});
            skLineSegment(sketch, "E1376", {"start": v(-41.06, -27.51) * mm, "end": v(-41.26, -27.71) * mm});
            skLineSegment(sketch, "E1377", {"start": v(-49.06, -27.51) * mm, "end": v(-48.86, -27.71) * mm});
            skLineSegment(sketch, "E1378", {"start": v(-41.26, -27.71) * mm, "end": v(-48.86, -27.71) * mm});
            skLineSegment(sketch, "E1379", {"start": v(26.85, -27.51) * mm, "end": v(26.85, -8.17) * mm});
            skLineSegment(sketch, "E1380", {"start": v(34.85, -27.51) * mm, "end": v(34.65, -27.71) * mm});
            skLineSegment(sketch, "E1381", {"start": v(26.85, -27.51) * mm, "end": v(27.05, -27.71) * mm});
            skLineSegment(sketch, "E1382", {"start": v(34.65, -27.71) * mm, "end": v(27.05, -27.71) * mm});
            skLineSegment(sketch, "E1383", {"start": v(34.85, -8.17) * mm, "end": v(34.85, -27.51) * mm});
            skLineSegment(sketch, "E1384", {"start": v(35.95, 36.36) * mm, "end": v(35.95, 43.69) * mm});
            skLineSegment(sketch, "E1385", {"start": v(50.85, 27.27) * mm, "end": v(50.85, 8.1) * mm});
            skLineSegment(sketch, "E1386", {"start": v(35.95, 42.19) * mm, "end": v(35.95, 43.69) * mm});
            skLineSegment(sketch, "E1387", {"start": v(35.95, -8.31) * mm, "end": v(35.95, -7.56) * mm});
            skLineSegment(sketch, "E1388", {"start": v(35.95, -8.31) * mm, "end": v(35.95, 28.22) * mm});
            skLineSegment(sketch, "E1389", {"start": v(35.95, 43.69) * mm, "end": v(35.65, 43.69) * mm});
            skLineSegment(sketch, "E1390", {"start": v(-45.06, 67.5) * mm, "end": v(-45.06, -53) * mm});
            skLineSegment(sketch, "E1391", {"start": v(30.85, 66.92) * mm, "end": v(30.85, -1.2) * mm});
            skLineSegment(sketch, "E1392", {"start": v(10.82, 17.69) * mm, "end": v(60.46, 17.69) * mm});
            skLineSegment(sketch, "E1393", {"start": v(-80.8, 17.69) * mm, "end": v(-8.42, 17.69) * mm});
            skLineSegment(sketch, "E1394", {"start": v(26.05, 43.69) * mm, "end": v(24.8, 43.69) * mm});
            skLineSegment(sketch, "E1395", {"start": v(35.65, -8.31) * mm, "end": v(35.95, -8.31) * mm});
            skLineSegment(sketch, "E1396", {"start": v(24.8, -8.31) * mm, "end": v(26.05, -8.31) * mm});
            skLineSegment(sketch, "E1397", {"start": v(34.03, 26.75) * mm, "end": v(34.03, 25.17) * mm});
            skLineSegment(sketch, "E1398", {"start": v(34.03, 26.75) * mm, "end": v(34.03, 27.03) * mm});
            skLineSegment(sketch, "E1399", {"start": v(27.68, 26.75) * mm, "end": v(27.68, 27.03) * mm});
            skLineSegment(sketch, "E1400", {"start": v(27.68, 26.75) * mm, "end": v(27.68, 25.17) * mm});
            skLineSegment(sketch, "E1401", {"start": v(27.68, 26.75) * mm, "end": v(34.03, 26.75) * mm});
            skLineSegment(sketch, "E1402", {"start": v(34.03, 25.17) * mm, "end": v(35.95, 25.17) * mm});
            skLineSegment(sketch, "E1403", {"start": v(34.03, 27.03) * mm, "end": v(34.03, 27.8) * mm});
            skLineSegment(sketch, "E1404", {"start": v(25.75, 21.63) * mm, "end": v(35.95, 21.63) * mm});
            skLineSegment(sketch, "E1405", {"start": v(25.75, 25.17) * mm, "end": v(25.75, 21.63) * mm});
            skLineSegment(sketch, "E1406", {"start": v(27.68, 25.17) * mm, "end": v(25.75, 25.17) * mm});
            skLineSegment(sketch, "E1407", {"start": v(27.68, 27.03) * mm, "end": v(27.68, 27.8) * mm});
            skLineSegment(sketch, "E1408", {"start": v(30.85, -1.2) * mm, "end": v(30.85, -51.81) * mm});
            skLineSegment(sketch, "E1409", {"start": v(25.75, 27.6) * mm, "end": v(25.75, 25.17) * mm});
            skArc(sketch, "E1410", {"start": v(26.05, 43.69) * mm, "mid": v(26.07, 43.69) * mm, "end": v(26.08, 43.68) * mm});
            skLineSegment(sketch, "E1411", {"start": v(26.08, 43.68) * mm, "end": v(26.5, 43.61) * mm});
            skLineSegment(sketch, "E1412", {"start": v(26.5, 43.61) * mm, "end": v(26.9, 43.55) * mm});
            skArc(sketch, "E1413", {"start": v(26.9, 43.55) * mm, "mid": v(27.77, 43.43) * mm, "end": v(28.64, 43.34) * mm});
            skLineSegment(sketch, "E1414", {"start": v(28.64, 43.34) * mm, "end": v(29.75, 43.27) * mm});
            skLineSegment(sketch, "E1415", {"start": v(29.75, 43.27) * mm, "end": v(30.85, 43.24) * mm});
            skArc(sketch, "E1416", {"start": v(30.85, 43.24) * mm, "mid": v(31.96, 43.27) * mm, "end": v(33.07, 43.34) * mm});
            skLineSegment(sketch, "E1417", {"start": v(33.07, 43.34) * mm, "end": v(33.93, 43.43) * mm});
            skLineSegment(sketch, "E1418", {"start": v(33.93, 43.43) * mm, "end": v(34.8, 43.55) * mm});
            skArc(sketch, "E1419", {"start": v(34.8, 43.55) * mm, "mid": v(35.21, 43.61) * mm, "end": v(35.62, 43.68) * mm});
            skLineSegment(sketch, "E1420", {"start": v(35.62, 43.68) * mm, "end": v(35.64, 43.69) * mm});
            skLineSegment(sketch, "E1421", {"start": v(35.64, 43.69) * mm, "end": v(35.65, 43.69) * mm});
            skArc(sketch, "E1422", {"start": v(35.65, -8.31) * mm, "mid": v(35.64, -8.3) * mm, "end": v(35.62, -8.3) * mm});
            skLineSegment(sketch, "E1423", {"start": v(35.62, -8.3) * mm, "end": v(35.21, -8.23) * mm});
            skLineSegment(sketch, "E1424", {"start": v(35.21, -8.23) * mm, "end": v(34.8, -8.17) * mm});
            skArc(sketch, "E1425", {"start": v(34.8, -8.17) * mm, "mid": v(33.94, -8.05) * mm, "end": v(33.07, -7.96) * mm});
            skLineSegment(sketch, "E1426", {"start": v(33.07, -7.96) * mm, "end": v(31.96, -7.89) * mm});
            skLineSegment(sketch, "E1427", {"start": v(31.96, -7.89) * mm, "end": v(30.85, -7.86) * mm});
            skArc(sketch, "E1428", {"start": v(30.85, -7.86) * mm, "mid": v(29.74, -7.89) * mm, "end": v(28.64, -7.96) * mm});
            skLineSegment(sketch, "E1429", {"start": v(28.64, -7.96) * mm, "end": v(27.77, -8.05) * mm});
            skLineSegment(sketch, "E1430", {"start": v(27.77, -8.05) * mm, "end": v(26.9, -8.17) * mm});
            skArc(sketch, "E1431", {"start": v(26.9, -8.17) * mm, "mid": v(26.5, -8.23) * mm, "end": v(26.08, -8.3) * mm});
            skLineSegment(sketch, "E1432", {"start": v(26.08, -8.3) * mm, "end": v(26.07, -8.3) * mm});
            skLineSegment(sketch, "E1433", {"start": v(26.07, -8.3) * mm, "end": v(26.05, -8.31) * mm});
            skLineSegment(sketch, "E1434", {"start": v(-59.23, 37.06) * mm, "end": v(-59.29, 37.14) * mm});
            skLineSegment(sketch, "E1435", {"start": v(-59.17, 37.23) * mm, "end": v(-59.1, 37.15) * mm});
            skLineSegment(sketch, "E1436", {"start": v(-59.29, 37.14) * mm, "end": v(-59.17, 37.23) * mm});
            skLineSegment(sketch, "E1437", {"start": v(-59.1, 37.15) * mm, "end": v(-46.43, 20.95) * mm});
            skLineSegment(sketch, "E1438", {"start": v(-47.74, 20) * mm, "end": v(-59.23, 37.06) * mm});
            skArc(sketch, "E1439", {"start": v(-47.47, 18.35) * mm, "mid": v(-43.6, 15.67) * mm, "end": v(-44.95, 20.19) * mm});
            skArc(sketch, "E1440", {"start": v(-47.47, 18.35) * mm, "mid": v(-47.43, 19.2) * mm, "end": v(-47.74, 20) * mm});
            skArc(sketch, "E1441", {"start": v(-46.43, 20.95) * mm, "mid": v(-45.77, 20.4) * mm, "end": v(-44.95, 20.19) * mm});
            skCircle(sketch, "E1442", {"center": v(-45.06, 17.69) * mm, "radius": 2.15 * mm});
            skCircle(sketch, "E1443", {"center": v(-45.06, 17.69) * mm, "radius": 0.45 * mm});
            skLineSegment(sketch, "E1444", {"start": v(-44.6, 66.49) * mm, "end": v(-45.5, 66.49) * mm});
            skLineSegment(sketch, "E1445", {"start": v(-45.5, 66.49) * mm, "end": v(-49.05, 66.49) * mm});
            skLineSegment(sketch, "E1446", {"start": v(-41.08, 66.49) * mm, "end": v(-44.6, 66.49) * mm});
            skLineSegment(sketch, "E1447", {"start": v(-49.45, 66.09) * mm, "end": v(-40.68, 66.09) * mm});
            skLineSegment(sketch, "E1448", {"start": v(-40.68, 66.09) * mm, "end": v(-41.08, 66.49) * mm});
            skLineSegment(sketch, "E1449", {"start": v(-49.45, 66.09) * mm, "end": v(-49.05, 66.49) * mm});
            skLineSegment(sketch, "E1450", {"start": v(-49.64, 55.39) * mm, "end": v(-49.45, 66.09) * mm});
            skLineSegment(sketch, "E1451", {"start": v(-40.67, 66.09) * mm, "end": v(-40.49, 55.39) * mm});
            skLineSegment(sketch, "E1452", {"start": v(-40.49, 55.6) * mm, "end": v(-40.49, 55.4) * mm});
            skLineSegment(sketch, "E1453", {"start": v(-40.49, 55.39) * mm, "end": v(-45.06, 55.39) * mm});
            skLineSegment(sketch, "E1454", {"start": v(-49.64, 55.4) * mm, "end": v(-49.64, 55.6) * mm});
            skLineSegment(sketch, "E1455", {"start": v(-45.06, 55.39) * mm, "end": v(-49.64, 55.39) * mm});
            skLineSegment(sketch, "E1456", {"start": v(-40.03, 54.55) * mm, "end": v(-45.06, 54.55) * mm});
            skLineSegment(sketch, "E1457", {"start": v(-45.06, 54.55) * mm, "end": v(-50.1, 54.55) * mm});
            skLineSegment(sketch, "E1458", {"start": v(-50.46, 46.08) * mm, "end": v(-50.51, 46.08) * mm});
            skLineSegment(sketch, "E1459", {"start": v(-49.66, 45.59) * mm, "end": v(-50.44, 46.04) * mm});
            skLineSegment(sketch, "E1460", {"start": v(-47.54, 46.08) * mm, "end": v(-50.46, 46.08) * mm});
            skLineSegment(sketch, "E1461", {"start": v(-50.23, 54.31) * mm, "end": v(-50.51, 46.08) * mm});
            skLineSegment(sketch, "E1462", {"start": v(-39.61, 46.08) * mm, "end": v(-39.66, 46.08) * mm});
            skLineSegment(sketch, "E1463", {"start": v(-39.69, 46.04) * mm, "end": v(-40.16, 45.76) * mm});
            skLineSegment(sketch, "E1464", {"start": v(-39.66, 46.08) * mm, "end": v(-43.27, 46.08) * mm});
            skLineSegment(sketch, "E1465", {"start": v(-39.61, 46.08) * mm, "end": v(-39.9, 54.31) * mm});
            skLineSegment(sketch, "E1466", {"start": v(30.85, 54.55) * mm, "end": v(25.82, 54.55) * mm});
            skLineSegment(sketch, "E1467", {"start": v(35.89, 54.55) * mm, "end": v(30.85, 54.55) * mm});
            skLineSegment(sketch, "E1468", {"start": v(26.46, 66.09) * mm, "end": v(26.86, 66.49) * mm});
            skLineSegment(sketch, "E1469", {"start": v(35.24, 66.09) * mm, "end": v(34.84, 66.49) * mm});
            skLineSegment(sketch, "E1470", {"start": v(36.3, 46.08) * mm, "end": v(36.25, 46.08) * mm});
            skLineSegment(sketch, "E1471", {"start": v(36.23, 46.04) * mm, "end": v(35.45, 45.59) * mm});
            skLineSegment(sketch, "E1472", {"start": v(36.25, 46.08) * mm, "end": v(30.85, 46.08) * mm});
            skLineSegment(sketch, "E1473", {"start": v(25.45, 46.08) * mm, "end": v(25.4, 46.08) * mm});
            skLineSegment(sketch, "E1474", {"start": v(26.25, 45.59) * mm, "end": v(25.47, 46.04) * mm});
            skLineSegment(sketch, "E1475", {"start": v(30.85, 46.08) * mm, "end": v(25.45, 46.08) * mm});
            skLineSegment(sketch, "E1476", {"start": v(26.46, 66.09) * mm, "end": v(35.24, 66.09) * mm});
            skLineSegment(sketch, "E1477", {"start": v(35.24, 66.09) * mm, "end": v(35.43, 55.39) * mm});
            skLineSegment(sketch, "E1478", {"start": v(26.28, 55.39) * mm, "end": v(26.46, 66.09) * mm});
            skLineSegment(sketch, "E1479", {"start": v(25.69, 54.31) * mm, "end": v(25.4, 46.08) * mm});
            skLineSegment(sketch, "E1480", {"start": v(36.3, 46.08) * mm, "end": v(36.01, 54.31) * mm});
            skLineSegment(sketch, "E1481", {"start": v(30.85, 55.39) * mm, "end": v(26.28, 55.39) * mm});
            skLineSegment(sketch, "E1482", {"start": v(26.28, 55.4) * mm, "end": v(26.28, 55.6) * mm});
            skLineSegment(sketch, "E1483", {"start": v(35.43, 55.39) * mm, "end": v(30.85, 55.39) * mm});
            skLineSegment(sketch, "E1484", {"start": v(35.43, 55.6) * mm, "end": v(35.43, 55.4) * mm});
            skLineSegment(sketch, "E1485", {"start": v(34.84, 66.49) * mm, "end": v(31.3, 66.49) * mm});
            skLineSegment(sketch, "E1486", {"start": v(30.4, 66.49) * mm, "end": v(26.86, 66.49) * mm});
            skLineSegment(sketch, "E1487", {"start": v(31.3, 66.49) * mm, "end": v(30.4, 66.49) * mm});
            skLineSegment(sketch, "E1488", {"start": v(35.35, 45.59) * mm, "end": v(35.45, 45.59) * mm});
            skLineSegment(sketch, "E1489", {"start": v(35.35, 45.59) * mm, "end": v(35.35, 45.49) * mm});
            skLineSegment(sketch, "E1490", {"start": v(26.35, 45.49) * mm, "end": v(35.35, 45.49) * mm});
            skLineSegment(sketch, "E1491", {"start": v(35.35, 45.59) * mm, "end": v(30.85, 45.59) * mm});
            skLineSegment(sketch, "E1492", {"start": v(26.25, 45.59) * mm, "end": v(26.35, 45.59) * mm});
            skLineSegment(sketch, "E1493", {"start": v(26.35, 45.49) * mm, "end": v(26.35, 45.59) * mm});
            skLineSegment(sketch, "E1494", {"start": v(30.85, 45.59) * mm, "end": v(26.35, 45.59) * mm});
            skArc(sketch, "E1495", {"start": v(-40.49, 55.39) * mm, "mid": v(-40.37, 54.91) * mm, "end": v(-40.04, 54.55) * mm});
            skArc(sketch, "E1496", {"start": v(-50.1, 54.55) * mm, "mid": v(-49.76, 54.91) * mm, "end": v(-49.64, 55.39) * mm});
            skArc(sketch, "E1497", {"start": v(-50.46, 46.08) * mm, "mid": v(-50.46, 46.05) * mm, "end": v(-50.44, 46.04) * mm});
            skArc(sketch, "E1498", {"start": v(-39.69, 46.04) * mm, "mid": v(-39.67, 46.05) * mm, "end": v(-39.66, 46.08) * mm});
            skArc(sketch, "E1499", {"start": v(36.23, 46.04) * mm, "mid": v(36.25, 46.05) * mm, "end": v(36.25, 46.08) * mm});
            skArc(sketch, "E1500", {"start": v(25.45, 46.08) * mm, "mid": v(25.46, 46.05) * mm, "end": v(25.47, 46.04) * mm});
            skArc(sketch, "E1501", {"start": v(25.82, 54.55) * mm, "mid": v(26.16, 54.91) * mm, "end": v(26.28, 55.39) * mm});
            skArc(sketch, "E1502", {"start": v(35.43, 55.39) * mm, "mid": v(35.55, 54.91) * mm, "end": v(35.88, 54.55) * mm});
            skArc(sketch, "E1503", {"start": v(-39.9, 54.31) * mm, "mid": v(-39.94, 54.45) * mm, "end": v(-40.04, 54.55) * mm});
            skArc(sketch, "E1504", {"start": v(-50.1, 54.55) * mm, "mid": v(-50.19, 54.45) * mm, "end": v(-50.23, 54.31) * mm});
            skArc(sketch, "E1505", {"start": v(25.82, 54.55) * mm, "mid": v(25.73, 54.45) * mm, "end": v(25.69, 54.31) * mm});
            skArc(sketch, "E1506", {"start": v(36.01, 54.31) * mm, "mid": v(35.98, 54.45) * mm, "end": v(35.88, 54.55) * mm});
            skArc(sketch, "E1507", {"start": v(-54.03, 7.86) * mm, "mid": v(-45.07, 4.15) * mm, "end": v(-48.78, 13.11) * mm});
            skArc(sketch, "E1508", {"start": v(-48.78, 13.11) * mm, "mid": v(-52.5, 11.57) * mm, "end": v(-54.03, 7.86) * mm});
            skLineSegment(sketch, "E1509", {"start": v(42.42, 25.76) * mm, "end": v(50.92, 25.69) * mm});
            skLineSegment(sketch, "E1510", {"start": v(50.92, 9.69) * mm, "end": v(42.42, 9.62) * mm});
            skLineSegment(sketch, "E1511", {"start": v(74.1, 25.73) * mm, "end": v(79.1, 25.73) * mm});
            skLineSegment(sketch, "E1512", {"start": v(79.1, 25.73) * mm, "end": v(79.1, 9.65) * mm});
            skLineSegment(sketch, "E1513", {"start": v(79.1, 9.65) * mm, "end": v(74.1, 9.65) * mm});
            skLineSegment(sketch, "E1514", {"start": v(74.1, 9.65) * mm, "end": v(74.1, 25.73) * mm});
            skLineSegment(sketch, "E1515", {"start": v(80.8, 17.69) * mm, "end": v(72.22, 17.69) * mm});
            skArc(sketch, "E1516", {"start": v(50.92, 9.69) * mm, "mid": v(56.53, 12.05) * mm, "end": v(58.85, 17.69) * mm});
            skArc(sketch, "E1517", {"start": v(38.45, 29.76) * mm, "mid": v(39.61, 26.94) * mm, "end": v(42.42, 25.76) * mm});
            skArc(sketch, "E1518", {"start": v(58.85, 17.69) * mm, "mid": v(56.53, 23.32) * mm, "end": v(50.92, 25.69) * mm});
            skArc(sketch, "E1519", {"start": v(42.42, 9.62) * mm, "mid": v(39.61, 8.44) * mm, "end": v(38.45, 5.62) * mm});
            skCircle(sketch, "E1520", {"center": v(50.85, 17.69) * mm, "radius": 3.25 * mm});
            skLineSegment(sketch, "E1521", {"start": v(35.95, 36.36) * mm, "end": v(35.95, 42.79) * mm});
            skLineSegment(sketch, "E1522", {"start": v(38.45, 42.09) * mm, "end": v(38.45, -6.71) * mm});
            skLineSegment(sketch, "E1523", {"start": v(37.75, -7.41) * mm, "end": v(35.95, -7.41) * mm});
            skLineSegment(sketch, "E1524", {"start": v(35.95, -7.41) * mm, "end": v(35.95, 28.22) * mm});
            skLineSegment(sketch, "E1525", {"start": v(35.95, 42.79) * mm, "end": v(37.75, 42.79) * mm});
            skArc(sketch, "E1526", {"start": v(37.75, -7.41) * mm, "mid": v(38.25, -7.2) * mm, "end": v(38.45, -6.71) * mm});
            skArc(sketch, "E1527", {"start": v(38.45, 42.09) * mm, "mid": v(38.25, 42.58) * mm, "end": v(37.75, 42.79) * mm});
            skLineSegment(sketch, "E1528", {"start": v(-48.48, 6.04) * mm, "end": v(-49.3, 6.1) * mm});
            skLineSegment(sketch, "E1529", {"start": v(-48.3, 9.74) * mm, "end": v(-48.34, 12.54) * mm});
            skLineSegment(sketch, "E1530", {"start": v(-48.34, 12.54) * mm, "end": v(-48.62, 12.56) * mm});
            skLineSegment(sketch, "E1531", {"start": v(-48.62, 12.56) * mm, "end": v(-49.01, 9.79) * mm});
            skArc(sketch, "E1532", {"start": v(-47.88, 8.94) * mm, "mid": v(-47.9, 8.95) * mm, "end": v(-47.92, 8.97) * mm});
            skArc(sketch, "E1533", {"start": v(-49.5, 9.07) * mm, "mid": v(-50.17, 7.97) * mm, "end": v(-49.66, 6.78) * mm});
            skArc(sketch, "E1534", {"start": v(-48.87, 6.47) * mm, "mid": v(-48.43, 6.5) * mm, "end": v(-48.03, 6.68) * mm});
            skArc(sketch, "E1535", {"start": v(-48.03, 6.68) * mm, "mid": v(-47.38, 7.77) * mm, "end": v(-47.88, 8.94) * mm});
            skArc(sketch, "E1536", {"start": v(-49.66, 6.78) * mm, "mid": v(-49.3, 6.56) * mm, "end": v(-48.87, 6.47) * mm});
            skArc(sketch, "E1537", {"start": v(-47.92, 8.97) * mm, "mid": v(-48.7, 9.26) * mm, "end": v(-49.5, 9.07) * mm});
            skArc(sketch, "E1538", {"start": v(-48.03, 6.68) * mm, "mid": v(-48.32, 6.4) * mm, "end": v(-48.48, 6.04) * mm});
            skArc(sketch, "E1539", {"start": v(-49.3, 6.1) * mm, "mid": v(-49.41, 6.47) * mm, "end": v(-49.66, 6.78) * mm});
            skArc(sketch, "E1540", {"start": v(-48.3, 9.74) * mm, "mid": v(-48.2, 9.3) * mm, "end": v(-47.92, 8.97) * mm});
            skArc(sketch, "E1541", {"start": v(-49.5, 9.07) * mm, "mid": v(-49.17, 9.37) * mm, "end": v(-49.01, 9.79) * mm});
            skCircle(sketch, "E1542", {"center": v(-48.78, 7.86) * mm, "radius": 0.33 * mm});
            skLineSegment(sketch, "E1543", {"start": v(-22.95, -57.5) * mm, "end": v(-22.95, -67.5) * mm});
            skLineSegment(sketch, "E1544", {"start": v(-22.95, -67.5) * mm, "end": v(3.55, -67.5) * mm});
            skLineSegment(sketch, "E1545", {"start": v(3.55, -67.5) * mm, "end": v(3.55, -57.5) * mm});
            skLineSegment(sketch, "E1546", {"start": v(3.55, -57.5) * mm, "end": v(-22.95, -57.5) * mm});
            skLineSegment(sketch, "E1547", {"start": v(24.8, -8.31) * mm, "end": v(35.95, -8.31) * mm});
            skSolve(sketch);
        }
        {
            var Q0;
            {var subQ0=sQuery(id+"F0.wireOp",EDGE,"E1349");Q0=makeQuery(id+"F0.imprint","IMPRINT",FACE,{"disambiguationData":[TD([[makeQuery(id+"F0.imprint","IMPRINT",EDGE,{"derivedFrom":subQ0}),1.0]])]});}
            var Q1;
            {var subQ1=sQuery(id+"F0.wireOp",EDGE,"E1339");Q1=makeQuery(id+"F0.imprint","IMPRINT",FACE,{"disambiguationData":[TD([[makeQuery(id+"F0.imprint","IMPRINT",EDGE,{"derivedFrom":subQ1}),1.0]])]});}
            var Q2;
            {var subQ0=sQuery(id+"F0.wireOp",EDGE,"E1335");Q2=makeQuery(id+"F0.imprint","IMPRINT",FACE,{"disambiguationData":[TD([[makeQuery(id+"F0.imprint","IMPRINT",EDGE,{"derivedFrom":subQ0}),-1.0]])]});}
            var Q3;
            {var subQ1=sQuery(id+"F0.wireOp",EDGE,"E1340");Q3=makeQuery(id+"F0.imprint","IMPRINT",FACE,{"disambiguationData":[TD([[makeQuery(id+"F0.imprint","IMPRINT",EDGE,{"derivedFrom":subQ1}),1.0]])]});}
            var Q4;
            {var subQ6=sQuery(id+"F0.wireOp",EDGE,"E1354");Q4=makeQuery(id+"F0.imprint","IMPRINT",FACE,{"disambiguationData":[TD([[makeQuery(id+"F0.imprint","IMPRINT",EDGE,{"derivedFrom":subQ6}),1.0]])]});}
            var Q5;
            {var subQ1=sQuery(id+"F0.wireOp",EDGE,"E1380");Q5=makeQuery(id+"F0.imprint","IMPRINT",FACE,{"disambiguationData":[TD([[makeQuery(id+"F0.imprint","IMPRINT",EDGE,{"derivedFrom":subQ1}),-1.0]])]});}
            var Q6;
            {var subQ0=sQuery(id+"F0.wireOp",EDGE,"0QQQHErx-zCLW-jhBt-ZCbz-dooOFAbkqet6");var subQ1=sQuery(id+"F0.wireOp",EDGE,"E1383");var subQ2=makeQuery(id+"F0.imprint","INTERSECT",VERTEX,{"derivedFrom":[subQ1,subQ0]});Q6=makeQuery(id+"F0.imprint","IMPRINT",FACE,{"disambiguationData":[TD([[makeQuery(id+"F0.imprint","IMPRINT",EDGE,{"disambiguationData":[TD([[subQ2,-1.0]])],"derivedFrom":subQ1}),-1.0]])]});}
            var Q7;
            Q7=sQuery(id+"F0.wireOp",EDGE,"E1408");
            revolve(context, id + "F1", {"surfaceOperationType" : NewSurfaceOperationType.NEW, "entities" : qUnion([Q0, Q1, Q2, Q3, Q4, Q5, Q6]), "axis" : qUnion([Q7]), "revolveType" : RevolveType.FULL});
        }
        {
            var Q0;
            Q0=makeQuery(id+"F1.opRevolve","SWEPT_FACE",FACE,{"disambiguationData":[OSD([sQuery(id+"F0.wireOp",EDGE,"E1547")])]});
            extrude(context, id + "F2", {"entities" : qUnion([Q0]), "operationType" : NewBodyOperationType.ADD, "depth" : 5 * mm, "offsetDistance" : 25 * mm});
        }
        {
            var Q0;
            Q0=makeQuery(id+"F0.imprint","IMPRINT",FACE,{"disambiguationData":[TD([[makeQuery(id+"F0.imprint","IMPRINT",EDGE,{"derivedFrom":sQuery(id+"F0.wireOp",EDGE,"E171")}),1.0]])]});
            var Q1;
            Q1=makeQuery(id+"F0.imprint","IMPRINT",FACE,{"disambiguationData":[TD([[makeQuery(id+"F0.imprint","IMPRINT",EDGE,{"derivedFrom":sQuery(id+"F0.wireOp",EDGE,"E184")}),1.0]])]});
            var Q2;
            {var subQ1=sQuery(id+"F0.wireOp",EDGE,"E202");Q2=makeQuery(id+"F0.imprint","IMPRINT",FACE,{"disambiguationData":[TD([[makeQuery(id+"F0.imprint","IMPRINT",EDGE,{"derivedFrom":subQ1}),1.0]])]});}
            var Q3;
            {var subQ2=sQuery(id+"F0.wireOp",EDGE,"E206");Q3=makeQuery(id+"F0.imprint","IMPRINT",FACE,{"disambiguationData":[TD([[makeQuery(id+"F0.imprint","IMPRINT",EDGE,{"derivedFrom":subQ2}),1.0]])]});}
            var Q4;
            {var subQ0=sQuery(id+"F0.wireOp",EDGE,"E180");Q4=makeQuery(id+"F0.imprint","IMPRINT",FACE,{"disambiguationData":[TD([[makeQuery(id+"F0.imprint","IMPRINT",EDGE,{"derivedFrom":subQ0}),-1.0]])]});}
            var Q5;
            {var subQ5=sQuery(id+"F0.wireOp",EDGE,"E205");Q5=makeQuery(id+"F0.imprint","IMPRINT",FACE,{"disambiguationData":[TD([[makeQuery(id+"F0.imprint","IMPRINT",EDGE,{"derivedFrom":subQ5}),-1.0]])]});}
            var Q6;
            {var subQ4=sQuery(id+"F0.wireOp",EDGE,"E1429");Q6=makeQuery(id+"F0.imprint","IMPRINT",FACE,{"disambiguationData":[TD([[makeQuery(id+"F0.imprint","IMPRINT",EDGE,{"derivedFrom":subQ4}),-1.0]])]});}
            var Q7;
            {var subQ1=sQuery(id+"F0.wireOp",EDGE,"E1432");Q7=makeQuery(id+"F0.imprint","IMPRINT",FACE,{"disambiguationData":[TD([[makeQuery(id+"F0.imprint","IMPRINT",EDGE,{"derivedFrom":subQ1}),1.0]])]});}
            var Q8;
            {var subQ0=sQuery(id+"F0.wireOp",EDGE,"E1429");Q8=makeQuery(id+"F0.imprint","IMPRINT",FACE,{"disambiguationData":[TD([[makeQuery(id+"F0.imprint","IMPRINT",EDGE,{"derivedFrom":subQ0}),1.0]])]});}
            var Q9;
            {var subQ0=sQuery(id+"F0.wireOp",EDGE,"E1425");Q9=makeQuery(id+"F0.imprint","IMPRINT",FACE,{"disambiguationData":[TD([[makeQuery(id+"F0.imprint","IMPRINT",EDGE,{"derivedFrom":subQ0}),1.0]])]});}
            var Q10;
            {var subQ4=sQuery(id+"F0.wireOp",EDGE,"E1422");Q10=makeQuery(id+"F0.imprint","IMPRINT",FACE,{"disambiguationData":[TD([[makeQuery(id+"F0.imprint","IMPRINT",EDGE,{"derivedFrom":subQ4}),1.0]])]});}
            var Q11;
            {var subQ3=sQuery(id+"F0.wireOp",EDGE,"E1422");Q11=makeQuery(id+"F0.imprint","IMPRINT",FACE,{"disambiguationData":[TD([[makeQuery(id+"F0.imprint","IMPRINT",EDGE,{"derivedFrom":subQ3}),-1.0]])]});}
            var Q12;
            Q12=sQuery(id+"F0.wireOp",EDGE,"E1392");
            revolve(context, id + "F3", {"operationType" : NewBodyOperationType.ADD, "surfaceOperationType" : NewSurfaceOperationType.NEW, "entities" : qUnion([Q0, Q1, Q2, Q3, Q4, Q5, Q6, Q7, Q8, Q9, Q10, Q11]), "axis" : qUnion([Q12]), "revolveType" : RevolveType.FULL});
        }
        {
            var Q0;
            {var subQ0=sQuery(id+"F0.wireOp",EDGE,"E1417");Q0=makeQuery(id+"F0.imprint","IMPRINT",FACE,{"disambiguationData":[TD([[makeQuery(id+"F0.imprint","IMPRINT",EDGE,{"derivedFrom":subQ0}),1.0]])]});}
            var Q1;
            Q1=makeQuery(id+"F0.imprint","IMPRINT",FACE,{"disambiguationData":[TD([[makeQuery(id+"F0.imprint","IMPRINT",EDGE,{"derivedFrom":sQuery(id+"F0.wireOp",EDGE,"E1470")}),-1.0]])]});
            var Q2;
            {var subQ3=sQuery(id+"F0.wireOp",EDGE,"E1489");Q2=makeQuery(id+"F0.imprint","IMPRINT",FACE,{"disambiguationData":[TD([[makeQuery(id+"F0.imprint","IMPRINT",EDGE,{"derivedFrom":subQ3}),-1.0]])]});}
            var Q3;
            {var subQ4=sQuery(id+"F0.wireOp",EDGE,"E1471");Q3=makeQuery(id+"F0.imprint","IMPRINT",FACE,{"disambiguationData":[TD([[makeQuery(id+"F0.imprint","IMPRINT",EDGE,{"derivedFrom":subQ4}),-1.0]])]});}
            var Q4;
            {var subQ0=sQuery(id+"F0.wireOp",EDGE,"E1502");Q4=makeQuery(id+"F0.imprint","IMPRINT",FACE,{"disambiguationData":[TD([[makeQuery(id+"F0.imprint","IMPRINT",EDGE,{"derivedFrom":subQ0}),-1.0]])]});}
            var Q5;
            {var subQ1=sQuery(id+"F0.wireOp",EDGE,"E1469");Q5=makeQuery(id+"F0.imprint","IMPRINT",FACE,{"disambiguationData":[TD([[makeQuery(id+"F0.imprint","IMPRINT",EDGE,{"derivedFrom":subQ1}),1.0]])]});}
            var Q6;
            {var subQ6=sQuery(id+"F0.wireOp",EDGE,"E1481");Q6=makeQuery(id+"F0.imprint","IMPRINT",FACE,{"disambiguationData":[TD([[makeQuery(id+"F0.imprint","IMPRINT",EDGE,{"derivedFrom":subQ6}),-1.0]])]});}
            var Q7;
            Q7=sQuery(id+"F0.wireOp",EDGE,"E1391");
            revolve(context, id + "F4", {"operationType" : NewBodyOperationType.ADD, "surfaceOperationType" : NewSurfaceOperationType.NEW, "entities" : qUnion([Q0, Q1, Q2, Q3, Q4, Q5, Q6]), "axis" : qUnion([Q7]), "revolveType" : RevolveType.FULL});
        }
        {
            var Q0;
            {var subQ0=sQuery(id+"F0.wireOp",EDGE,"E1523");Q0=makeQuery(id+"F0.imprint","IMPRINT",FACE,{"disambiguationData":[TD([[makeQuery(id+"F0.imprint","IMPRINT",EDGE,{"derivedFrom":subQ0}),-1.0]])]});}
            var Q1;
            Q1=sQuery(id+"F0.wireOp",EDGE,"E1392");
            revolve(context, id + "F5", {"surfaceOperationType" : NewSurfaceOperationType.NEW, "entities" : qUnion([Q0]), "axis" : qUnion([Q1]), "revolveType" : RevolveType.FULL});
        }
        {
            var Q0;
            Q0=makeQuery(id+"F3.opRevolve","SWEPT_FACE",FACE,{"disambiguationData":[OSD([sQuery(id+"F0.wireOp",EDGE,"E1388"),sQuery(id+"F0.wireOp",EDGE,"E1524")])]});
            var sketch = newSketch(context, id + "F6", { "sketchPlane" : qUnion([Q0])});
            skCircle(sketch, "E1548", {"center": v(0, 17.69) * mm, "radius": 26.1 * mm});
            skLineSegment(sketch, "E1549", {"start": v(0, 17.69) * mm, "end": v(-25.8, 21.63) * mm, "construction": true});
            skLineSegment(sketch, "E1550", {"start": v(-25.8, 21.63) * mm, "end": v(0, 21.63) * mm, "construction": true});
            skLineSegment(sketch, "E1551", {"start": v(0, 17.69) * mm, "end": v(-25, 25.17) * mm, "construction": true});
            skLineSegment(sketch, "E1552", {"start": v(-25, 25.17) * mm, "end": v(0, 25.17) * mm, "construction": true});
            skLineSegment(sketch, "E1553", {"start": v(-25.8, 21.63) * mm, "end": v(-25.82, 26.82) * mm});
            skLineSegment(sketch, "E1554", {"start": v(-25.82, 26.82) * mm, "end": v(-26.58, 27.26) * mm});
            skLineSegment(sketch, "E1555", {"start": v(-26.58, 27.26) * mm, "end": v(-24.08, 31.59) * mm});
            skLineSegment(sketch, "E1556", {"start": v(-24.08, 31.59) * mm, "end": v(-22.6, 30.74) * mm, "construction": true});
            skLineSegment(sketch, "E1557.MirrorCS", {"start": v(-21.58, 35.92) * mm, "end": v(-24.08, 31.59) * mm});
            skLineSegment(sketch, "E1558.MirrorCS", {"start": v(-20.82, 35.48) * mm, "end": v(-21.58, 35.92) * mm, "construction": true});
            skLineSegment(sketch, "E1559", {"start": v(0, 17.69) * mm, "end": v(-49.62, 17.69) * mm, "construction": true});
            skLineSegment(sketch, "E1560", {"start": v(0, 17.69) * mm, "end": v(0, 51.13) * mm, "construction": true});
            skLineSegment(sketch, "E1561.MirrorCS", {"start": v(21.58, 35.92) * mm, "end": v(24.08, 31.59) * mm});
            skLineSegment(sketch, "E1562.MirrorCS", {"start": v(26.58, 27.26) * mm, "end": v(24.08, 31.59) * mm});
            skLineSegment(sketch, "E1563.MirrorCS", {"start": v(24.08, 31.59) * mm, "end": v(22.6, 30.74) * mm, "construction": true});
            skLineSegment(sketch, "E1564.MirrorCS", {"start": v(25.82, 26.82) * mm, "end": v(26.58, 27.26) * mm});
            skLineSegment(sketch, "E1565.MirrorCS", {"start": v(25.8, 21.63) * mm, "end": v(25.82, 26.82) * mm});
            skLineSegment(sketch, "E1566", {"start": v(21.58, 35.92) * mm, "end": v(19.6, 35.9) * mm});
            skLineSegment(sketch, "E1567", {"start": v(19.6, 35.9) * mm, "end": v(19.33, 36.36) * mm});
            skLineSegment(sketch, "E1568", {"start": v(19.33, 36.36) * mm, "end": v(18.26, 36.34) * mm});
            skLineSegment(sketch, "E1569.MirrorCS", {"start": v(-19.33, 36.36) * mm, "end": v(-18.26, 36.34) * mm});
            skLineSegment(sketch, "E1570.MirrorCS", {"start": v(-19.6, 35.9) * mm, "end": v(-19.33, 36.36) * mm});
            skLineSegment(sketch, "E1571.MirrorCS", {"start": v(-21.58, 35.92) * mm, "end": v(-19.6, 35.9) * mm});
            skSolve(sketch);
        }
        {
            var Q0;
            {var subQ0=sQuery(id+"F6.wireOp",EDGE,"E1553");Q0=makeQuery(id+"F6.imprint","IMPRINT",FACE,{"disambiguationData":[TD([[makeQuery(id+"F6.imprint","IMPRINT",EDGE,{"derivedFrom":subQ0}),-1.0]])]});}
            var Q1;
            Q1=makeQuery(id+"F6.imprint","IMPRINT",FACE,{"disambiguationData":[TD([[makeQuery(id+"F6.imprint","IMPRINT",EDGE,{"derivedFrom":sQuery(id+"F6.wireOp",EDGE,"E1561.MirrorCS")}),-1.0]])]});
            var Q2;
            Q2=makeQuery(id+"F6.imprint","IMPRINT",FACE,{"disambiguationData":[TD([[makeQuery(id+"F6.imprint","IMPRINT",EDGE,{"derivedFrom":makeQuery(id+"F3.opRevolve","SWEPT_EDGE",EDGE,{"disambiguationData":[OSD([sQuery(id+"F0.wireOp",EDGE,"E1388"),sQuery(id+"F0.wireOp",EDGE,"E1547")])]})}),1.0]])]});
            extrude(context, id + "F7", {"entities" : qUnion([Q0, Q1, Q2]), "operationType" : NewBodyOperationType.ADD, "oppositeDirection" : true, "depth" : 10.2 * mm, "offsetDistance" : 25 * mm});
        }
        {
            var Q0;
            Q0=makeQuery(id+"F5.opRevolve","SWEPT_FACE",FACE,{"disambiguationData":[OSD([sQuery(id+"F0.wireOp",EDGE,"E1522")])]});
            var sketch = newSketch(context, id + "F8", { "sketchPlane" : qUnion([Q0])});
            skLineSegment(sketch, "E1572.bottom", {"start": v(16.35, 34.04) * mm, "end": v(-16.35, 34.04) * mm, "construction": true});
            skLineSegment(sketch, "E1572.top", {"start": v(16.35, 1.34) * mm, "end": v(-16.35, 1.34) * mm, "construction": true});
            skLineSegment(sketch, "E1572.left", {"start": v(16.35, 34.04) * mm, "end": v(16.35, 1.34) * mm, "construction": true});
            skLineSegment(sketch, "E1572.right", {"start": v(-16.35, 34.04) * mm, "end": v(-16.35, 1.34) * mm, "construction": true});
            skPoint(sketch, "E1572.middle", {"position": v(0, 17.69) * mm});
            skCircle(sketch, "E1573", {"center": v(-16.35, 34.04) * mm, "radius": 1.4 * mm});
            skCircle(sketch, "E1574", {"center": v(-16.35, 34.04) * mm, "radius": 1.9 * mm});
            skLineSegment(sketch, "E1575", {"start": v(-17.7, 32.7) * mm, "end": v(-19.04, 34.04) * mm});
            skLineSegment(sketch, "E1576", {"start": v(-15, 35.38) * mm, "end": v(-16.35, 36.73) * mm});
            skLineSegment(sketch, "E1577", {"start": v(-17.7, 32.7) * mm, "end": v(-15, 35.38) * mm, "construction": true});
            skLineSegment(sketch, "E1578", {"start": v(-16.35, 34.04) * mm, "end": v(0, 17.69) * mm, "construction": true});
            skCircle(sketch, "E1579.1.0", {"center": v(-16.35, 1.34) * mm, "radius": 1.9 * mm});
            skLineSegment(sketch, "E1579.1.1", {"start": v(-17.7, 2.68) * mm, "end": v(-19.04, 1.33) * mm});
            skLineSegment(sketch, "E1579.1.2", {"start": v(-15, 0) * mm, "end": v(-16.35, -1.35) * mm});
            skCircle(sketch, "E1579.1.3", {"center": v(-16.35, 1.34) * mm, "radius": 1.4 * mm});
            skCircle(sketch, "E1579.2.0", {"center": v(16.35, 1.34) * mm, "radius": 1.9 * mm});
            skLineSegment(sketch, "E1579.2.1", {"start": v(15, 0) * mm, "end": v(16.35, -1.35) * mm});
            skLineSegment(sketch, "E1579.2.2", {"start": v(17.7, 2.68) * mm, "end": v(19.04, 1.33) * mm});
            skCircle(sketch, "E1579.2.3", {"center": v(16.35, 1.34) * mm, "radius": 1.4 * mm});
            skCircle(sketch, "E1580.1.3.0", {"center": v(16.35, 34.04) * mm, "radius": 1.9 * mm});
            skLineSegment(sketch, "E1580.2.3.0", {"start": v(17.7, 32.7) * mm, "end": v(19.04, 34.04) * mm});
            skLineSegment(sketch, "E1580.5.3.0", {"start": v(15, 35.38) * mm, "end": v(16.35, 36.73) * mm});
            skCircle(sketch, "E1580.8.3.0", {"center": v(16.35, 34.04) * mm, "radius": 1.4 * mm});
            skArc(sketch, "E1581", {"start": v(-16.35, 36.73) * mm, "mid": v(-17.75, 35.44) * mm, "end": v(-19.04, 34.04) * mm});
            skArc(sketch, "E1582.1.0", {"start": v(-19.04, 1.33) * mm, "mid": v(-17.75, -0.06) * mm, "end": v(-16.35, -1.35) * mm});
            skArc(sketch, "E1582.2.0", {"start": v(16.35, -1.35) * mm, "mid": v(17.75, -0.06) * mm, "end": v(19.04, 1.33) * mm});
            skArc(sketch, "E1583.3.3.0", {"start": v(19.04, 34.04) * mm, "mid": v(17.75, 35.44) * mm, "end": v(16.35, 36.73) * mm});
            skSolve(sketch);
        }
        {
            var Q0;
            {var subQ0=sQuery(id+"F8.wireOp",EDGE,"E1573");var subQ1=makeQuery(id+"F5.opRevolve","SWEPT_EDGE",EDGE,{"disambiguationData":[OSD([sQuery(id+"F0.wireOp",EDGE,"E1522"),sQuery(id+"F0.wireOp",EDGE,"E1526")])]});var subQ2=makeQuery(id+"F8.imprint","INTERSECT",VERTEX,{"disambiguationData":[OD(0.0)],"derivedFrom":[subQ1,subQ0]});Q0=makeQuery(id+"F8.imprint","IMPRINT",FACE,{"disambiguationData":[TD([[makeQuery(id+"F8.imprint","IMPRINT",EDGE,{"disambiguationData":[TD([[subQ2,1.0]])],"derivedFrom":subQ0}),1.0]])]});}
            var Q1;
            {var subQ0=sQuery(id+"F8.wireOp",EDGE,"E1580.8.3.0");var subQ1=makeQuery(id+"F5.opRevolve","SWEPT_EDGE",EDGE,{"disambiguationData":[OSD([sQuery(id+"F0.wireOp",EDGE,"E1522"),sQuery(id+"F0.wireOp",EDGE,"E1526")])]});var subQ2=makeQuery(id+"F8.imprint","INTERSECT",VERTEX,{"disambiguationData":[OD(0.0)],"derivedFrom":[subQ1,subQ0]});Q1=makeQuery(id+"F8.imprint","IMPRINT",FACE,{"disambiguationData":[TD([[makeQuery(id+"F8.imprint","IMPRINT",EDGE,{"disambiguationData":[TD([[subQ2,1.0]])],"derivedFrom":subQ0}),1.0]])]});}
            var Q2;
            {var subQ0=sQuery(id+"F8.wireOp",EDGE,"E1579.1.3");var subQ1=makeQuery(id+"F5.opRevolve","SWEPT_EDGE",EDGE,{"disambiguationData":[OSD([sQuery(id+"F0.wireOp",EDGE,"E1522"),sQuery(id+"F0.wireOp",EDGE,"E1526")])]});var subQ2=makeQuery(id+"F8.imprint","INTERSECT",VERTEX,{"disambiguationData":[OD(0.0)],"derivedFrom":[subQ1,subQ0]});Q2=makeQuery(id+"F8.imprint","IMPRINT",FACE,{"disambiguationData":[TD([[makeQuery(id+"F8.imprint","IMPRINT",EDGE,{"disambiguationData":[TD([[subQ2,1.0]])],"derivedFrom":subQ0}),1.0]])]});}
            var Q3;
            {var subQ0=sQuery(id+"F8.wireOp",EDGE,"E1579.1.3");var subQ1=makeQuery(id+"F5.opRevolve","SWEPT_EDGE",EDGE,{"disambiguationData":[OSD([sQuery(id+"F0.wireOp",EDGE,"E1522"),sQuery(id+"F0.wireOp",EDGE,"E1526")])]});var subQ2=makeQuery(id+"F8.imprint","INTERSECT",VERTEX,{"disambiguationData":[OD(0.0)],"derivedFrom":[subQ1,subQ0]});Q3=makeQuery(id+"F8.imprint","IMPRINT",FACE,{"disambiguationData":[TD([[makeQuery(id+"F8.imprint","IMPRINT",EDGE,{"disambiguationData":[TD([[subQ2,-1.0]])],"derivedFrom":subQ0}),1.0]])]});}
            var Q4;
            {var subQ0=sQuery(id+"F8.wireOp",EDGE,"E1579.2.3");var subQ1=makeQuery(id+"F5.opRevolve","SWEPT_EDGE",EDGE,{"disambiguationData":[OSD([sQuery(id+"F0.wireOp",EDGE,"E1522"),sQuery(id+"F0.wireOp",EDGE,"E1526")])]});var subQ2=makeQuery(id+"F8.imprint","INTERSECT",VERTEX,{"disambiguationData":[OD(0.0)],"derivedFrom":[subQ1,subQ0]});Q4=makeQuery(id+"F8.imprint","IMPRINT",FACE,{"disambiguationData":[TD([[makeQuery(id+"F8.imprint","IMPRINT",EDGE,{"disambiguationData":[TD([[subQ2,1.0]])],"derivedFrom":subQ0}),1.0]])]});}
            var Q5;
            {var subQ0=sQuery(id+"F8.wireOp",EDGE,"E1579.2.3");var subQ1=makeQuery(id+"F5.opRevolve","SWEPT_EDGE",EDGE,{"disambiguationData":[OSD([sQuery(id+"F0.wireOp",EDGE,"E1522"),sQuery(id+"F0.wireOp",EDGE,"E1526")])]});var subQ2=makeQuery(id+"F8.imprint","INTERSECT",VERTEX,{"disambiguationData":[OD(0.0)],"derivedFrom":[subQ1,subQ0]});Q5=makeQuery(id+"F8.imprint","IMPRINT",FACE,{"disambiguationData":[TD([[makeQuery(id+"F8.imprint","IMPRINT",EDGE,{"disambiguationData":[TD([[subQ2,-1.0]])],"derivedFrom":subQ0}),1.0]])]});}
            var Q6;
            {var subQ0=sQuery(id+"F8.wireOp",EDGE,"E1580.8.3.0");var subQ1=makeQuery(id+"F5.opRevolve","SWEPT_EDGE",EDGE,{"disambiguationData":[OSD([sQuery(id+"F0.wireOp",EDGE,"E1522"),sQuery(id+"F0.wireOp",EDGE,"E1526")])]});var subQ2=makeQuery(id+"F8.imprint","INTERSECT",VERTEX,{"disambiguationData":[OD(0.0)],"derivedFrom":[subQ1,subQ0]});Q6=makeQuery(id+"F8.imprint","IMPRINT",FACE,{"disambiguationData":[TD([[makeQuery(id+"F8.imprint","IMPRINT",EDGE,{"disambiguationData":[TD([[subQ2,-1.0]])],"derivedFrom":subQ0}),1.0]])]});}
            var Q7;
            {var subQ0=sQuery(id+"F8.wireOp",EDGE,"E1573");var subQ1=makeQuery(id+"F5.opRevolve","SWEPT_EDGE",EDGE,{"disambiguationData":[OSD([sQuery(id+"F0.wireOp",EDGE,"E1522"),sQuery(id+"F0.wireOp",EDGE,"E1526")])]});var subQ2=makeQuery(id+"F8.imprint","INTERSECT",VERTEX,{"disambiguationData":[OD(0.0)],"derivedFrom":[subQ1,subQ0]});Q7=makeQuery(id+"F8.imprint","IMPRINT",FACE,{"disambiguationData":[TD([[makeQuery(id+"F8.imprint","IMPRINT",EDGE,{"disambiguationData":[TD([[subQ2,-1.0]])],"derivedFrom":subQ0}),1.0]])]});}
            extrude(context, id + "F9", {"entities" : qUnion([Q0, Q1, Q2, Q3, Q4, Q5, Q6, Q7]), "operationType" : NewBodyOperationType.REMOVE, "oppositeDirection" : true, "depth" : 5.5 * mm, "offsetDistance" : 25 * mm});
        }
        {
            var Q0;
            {var subQ0=sQuery(id+"F8.wireOp",EDGE,"E1579.2.0");var subQ1=makeQuery(id+"F8.imprint","INTERSECT",VERTEX,{"derivedFrom":[subQ0,sQuery(id+"F8.wireOp",EDGE,"E1579.2.1")]});Q0=makeQuery(id+"F8.imprint","IMPRINT",FACE,{"disambiguationData":[TD([[makeQuery(id+"F8.imprint","IMPRINT",EDGE,{"disambiguationData":[TD([[subQ1,1.0]])],"derivedFrom":subQ0}),1.0]])]});}
            var Q1;
            {var subQ0=sQuery(id+"F8.wireOp",EDGE,"E1579.2.1");var subQ1=sQuery(id+"F8.wireOp",EDGE,"E1579.2.0");var subQ2=makeQuery(id+"F8.imprint","INTERSECT",VERTEX,{"derivedFrom":[subQ1,subQ0]});Q1=makeQuery(id+"F8.imprint","IMPRINT",FACE,{"disambiguationData":[TD([[makeQuery(id+"F8.imprint","IMPRINT",EDGE,{"disambiguationData":[TD([[subQ2,-1.0]])],"derivedFrom":subQ1}),-1.0]])]});}
            var Q2;
            {var subQ0=sQuery(id+"F8.wireOp",EDGE,"E1579.2.2");var subQ1=sQuery(id+"F8.wireOp",EDGE,"E1579.2.0");var subQ2=makeQuery(id+"F8.imprint","INTERSECT",VERTEX,{"derivedFrom":[subQ1,subQ0]});Q2=makeQuery(id+"F8.imprint","IMPRINT",FACE,{"disambiguationData":[TD([[makeQuery(id+"F8.imprint","IMPRINT",EDGE,{"disambiguationData":[TD([[subQ2,1.0]])],"derivedFrom":subQ1}),-1.0]])]});}
            var Q3;
            {var subQ0=sQuery(id+"F8.wireOp",EDGE,"E1579.2.0");var subQ1=makeQuery(id+"F5.opRevolve","SWEPT_EDGE",EDGE,{"disambiguationData":[OSD([sQuery(id+"F0.wireOp",EDGE,"E1522"),sQuery(id+"F0.wireOp",EDGE,"E1526")])]});var subQ2=makeQuery(id+"F8.imprint","INTERSECT",VERTEX,{"disambiguationData":[OD(0.0)],"derivedFrom":[subQ1,subQ0]});Q3=makeQuery(id+"F8.imprint","IMPRINT",FACE,{"disambiguationData":[TD([[makeQuery(id+"F8.imprint","IMPRINT",EDGE,{"disambiguationData":[TD([[subQ2,-1.0]])],"derivedFrom":subQ0}),1.0]])]});}
            var Q4;
            {var subQ0=sQuery(id+"F8.wireOp",EDGE,"E1582.2.0");Q4=makeQuery(id+"F8.imprint","IMPRINT",FACE,{"disambiguationData":[TD([[makeQuery(id+"F8.imprint","IMPRINT",EDGE,{"derivedFrom":subQ0}),1.0]])]});}
            var Q5;
            {var subQ0=sQuery(id+"F8.wireOp",EDGE,"E1583.3.3.0");Q5=makeQuery(id+"F8.imprint","IMPRINT",FACE,{"disambiguationData":[TD([[makeQuery(id+"F8.imprint","IMPRINT",EDGE,{"derivedFrom":subQ0}),1.0]])]});}
            var Q6;
            {var subQ4=sQuery(id+"F8.wireOp",EDGE,"E1580.1.3.0");var subQ5=makeQuery(id+"F8.imprint","INTERSECT",VERTEX,{"derivedFrom":[subQ4,sQuery(id+"F8.wireOp",EDGE,"E1580.2.3.0")]});Q6=makeQuery(id+"F8.imprint","IMPRINT",FACE,{"disambiguationData":[TD([[makeQuery(id+"F8.imprint","IMPRINT",EDGE,{"disambiguationData":[TD([[subQ5,1.0]])],"derivedFrom":subQ4}),1.0]])]});}
            var Q7;
            {var subQ0=sQuery(id+"F8.wireOp",EDGE,"E1580.1.3.0");var subQ1=makeQuery(id+"F5.opRevolve","SWEPT_EDGE",EDGE,{"disambiguationData":[OSD([sQuery(id+"F0.wireOp",EDGE,"E1522"),sQuery(id+"F0.wireOp",EDGE,"E1526")])]});var subQ2=makeQuery(id+"F8.imprint","INTERSECT",VERTEX,{"disambiguationData":[OD(0.0)],"derivedFrom":[subQ1,subQ0]});Q7=makeQuery(id+"F8.imprint","IMPRINT",FACE,{"disambiguationData":[TD([[makeQuery(id+"F8.imprint","IMPRINT",EDGE,{"disambiguationData":[TD([[subQ2,-1.0]])],"derivedFrom":subQ0}),1.0]])]});}
            var Q8;
            {var subQ0=sQuery(id+"F8.wireOp",EDGE,"E1580.2.3.0");var subQ1=sQuery(id+"F8.wireOp",EDGE,"E1580.1.3.0");var subQ2=makeQuery(id+"F8.imprint","INTERSECT",VERTEX,{"derivedFrom":[subQ1,subQ0]});Q8=makeQuery(id+"F8.imprint","IMPRINT",FACE,{"disambiguationData":[TD([[makeQuery(id+"F8.imprint","IMPRINT",EDGE,{"disambiguationData":[TD([[subQ2,-1.0]])],"derivedFrom":subQ1}),-1.0]])]});}
            var Q9;
            {var subQ0=sQuery(id+"F8.wireOp",EDGE,"E1580.5.3.0");var subQ1=sQuery(id+"F8.wireOp",EDGE,"E1580.1.3.0");var subQ2=makeQuery(id+"F8.imprint","INTERSECT",VERTEX,{"derivedFrom":[subQ1,subQ0]});Q9=makeQuery(id+"F8.imprint","IMPRINT",FACE,{"disambiguationData":[TD([[makeQuery(id+"F8.imprint","IMPRINT",EDGE,{"disambiguationData":[TD([[subQ2,1.0]])],"derivedFrom":subQ1}),-1.0]])]});}
            var Q10;
            {var subQ0=sQuery(id+"F8.wireOp",EDGE,"E1581");Q10=makeQuery(id+"F8.imprint","IMPRINT",FACE,{"disambiguationData":[TD([[makeQuery(id+"F8.imprint","IMPRINT",EDGE,{"derivedFrom":subQ0}),1.0]])]});}
            var Q11;
            {var subQ0=sQuery(id+"F8.wireOp",EDGE,"E1573");var subQ1=makeQuery(id+"F5.opRevolve","SWEPT_EDGE",EDGE,{"disambiguationData":[OSD([sQuery(id+"F0.wireOp",EDGE,"E1522"),sQuery(id+"F0.wireOp",EDGE,"E1526")])]});var subQ2=makeQuery(id+"F8.imprint","INTERSECT",VERTEX,{"disambiguationData":[OD(0.0)],"derivedFrom":[subQ1,subQ0]});Q11=makeQuery(id+"F8.imprint","IMPRINT",FACE,{"disambiguationData":[TD([[makeQuery(id+"F8.imprint","IMPRINT",EDGE,{"disambiguationData":[TD([[subQ2,-1.0]])],"derivedFrom":subQ0}),-1.0]])]});}
            var Q12;
            {var subQ0=sQuery(id+"F8.wireOp",EDGE,"E1576");var subQ1=sQuery(id+"F8.wireOp",EDGE,"E1574");var subQ2=makeQuery(id+"F8.imprint","INTERSECT",VERTEX,{"derivedFrom":[subQ1,subQ0]});Q12=makeQuery(id+"F8.imprint","IMPRINT",FACE,{"disambiguationData":[TD([[makeQuery(id+"F8.imprint","IMPRINT",EDGE,{"disambiguationData":[TD([[subQ2,-1.0]])],"derivedFrom":subQ1}),-1.0]])]});}
            var Q13;
            {var subQ0=sQuery(id+"F8.wireOp",EDGE,"E1574");var subQ1=makeQuery(id+"F8.imprint","INTERSECT",VERTEX,{"derivedFrom":[subQ0,sQuery(id+"F8.wireOp",EDGE,"E1575")]});Q13=makeQuery(id+"F8.imprint","IMPRINT",FACE,{"disambiguationData":[TD([[makeQuery(id+"F8.imprint","IMPRINT",EDGE,{"disambiguationData":[TD([[subQ1,-1.0]])],"derivedFrom":subQ0}),1.0]])]});}
            var Q14;
            {var subQ0=sQuery(id+"F8.wireOp",EDGE,"E1575");var subQ1=sQuery(id+"F8.wireOp",EDGE,"E1574");var subQ2=makeQuery(id+"F8.imprint","INTERSECT",VERTEX,{"derivedFrom":[subQ1,subQ0]});Q14=makeQuery(id+"F8.imprint","IMPRINT",FACE,{"disambiguationData":[TD([[makeQuery(id+"F8.imprint","IMPRINT",EDGE,{"disambiguationData":[TD([[subQ2,1.0]])],"derivedFrom":subQ1}),-1.0]])]});}
            var Q15;
            {var subQ0=sQuery(id+"F8.wireOp",EDGE,"E1582.1.0");Q15=makeQuery(id+"F8.imprint","IMPRINT",FACE,{"disambiguationData":[TD([[makeQuery(id+"F8.imprint","IMPRINT",EDGE,{"derivedFrom":subQ0}),1.0]])]});}
            var Q16;
            {var subQ0=sQuery(id+"F8.wireOp",EDGE,"E1579.1.1");var subQ1=sQuery(id+"F8.wireOp",EDGE,"E1579.1.0");var subQ2=makeQuery(id+"F8.imprint","INTERSECT",VERTEX,{"derivedFrom":[subQ1,subQ0]});Q16=makeQuery(id+"F8.imprint","IMPRINT",FACE,{"disambiguationData":[TD([[makeQuery(id+"F8.imprint","IMPRINT",EDGE,{"disambiguationData":[TD([[subQ2,-1.0]])],"derivedFrom":subQ1}),-1.0]])]});}
            var Q17;
            {var subQ4=sQuery(id+"F8.wireOp",EDGE,"E1579.1.0");var subQ5=makeQuery(id+"F8.imprint","INTERSECT",VERTEX,{"derivedFrom":[subQ4,sQuery(id+"F8.wireOp",EDGE,"E1579.1.1")]});Q17=makeQuery(id+"F8.imprint","IMPRINT",FACE,{"disambiguationData":[TD([[makeQuery(id+"F8.imprint","IMPRINT",EDGE,{"disambiguationData":[TD([[subQ5,1.0]])],"derivedFrom":subQ4}),1.0]])]});}
            var Q18;
            {var subQ0=sQuery(id+"F8.wireOp",EDGE,"E1579.1.0");var subQ1=makeQuery(id+"F5.opRevolve","SWEPT_EDGE",EDGE,{"disambiguationData":[OSD([sQuery(id+"F0.wireOp",EDGE,"E1522"),sQuery(id+"F0.wireOp",EDGE,"E1526")])]});var subQ2=makeQuery(id+"F8.imprint","INTERSECT",VERTEX,{"disambiguationData":[OD(0.0)],"derivedFrom":[subQ1,subQ0]});Q18=makeQuery(id+"F8.imprint","IMPRINT",FACE,{"disambiguationData":[TD([[makeQuery(id+"F8.imprint","IMPRINT",EDGE,{"disambiguationData":[TD([[subQ2,-1.0]])],"derivedFrom":subQ0}),1.0]])]});}
            var Q19;
            {var subQ0=sQuery(id+"F8.wireOp",EDGE,"E1579.1.2");var subQ1=sQuery(id+"F8.wireOp",EDGE,"E1579.1.0");var subQ2=makeQuery(id+"F8.imprint","INTERSECT",VERTEX,{"derivedFrom":[subQ1,subQ0]});Q19=makeQuery(id+"F8.imprint","IMPRINT",FACE,{"disambiguationData":[TD([[makeQuery(id+"F8.imprint","IMPRINT",EDGE,{"disambiguationData":[TD([[subQ2,1.0]])],"derivedFrom":subQ1}),-1.0]])]});}
            extrude(context, id + "F10", {"entities" : qUnion([Q0, Q1, Q2, Q3, Q4, Q5, Q6, Q7, Q8, Q9, Q10, Q11, Q12, Q13, Q14, Q15, Q16, Q17, Q18, Q19]), "operationType" : NewBodyOperationType.REMOVE, "oppositeDirection" : true, "depth" : 1.2 * mm, "offsetDistance" : 25 * mm});
        }
    });
